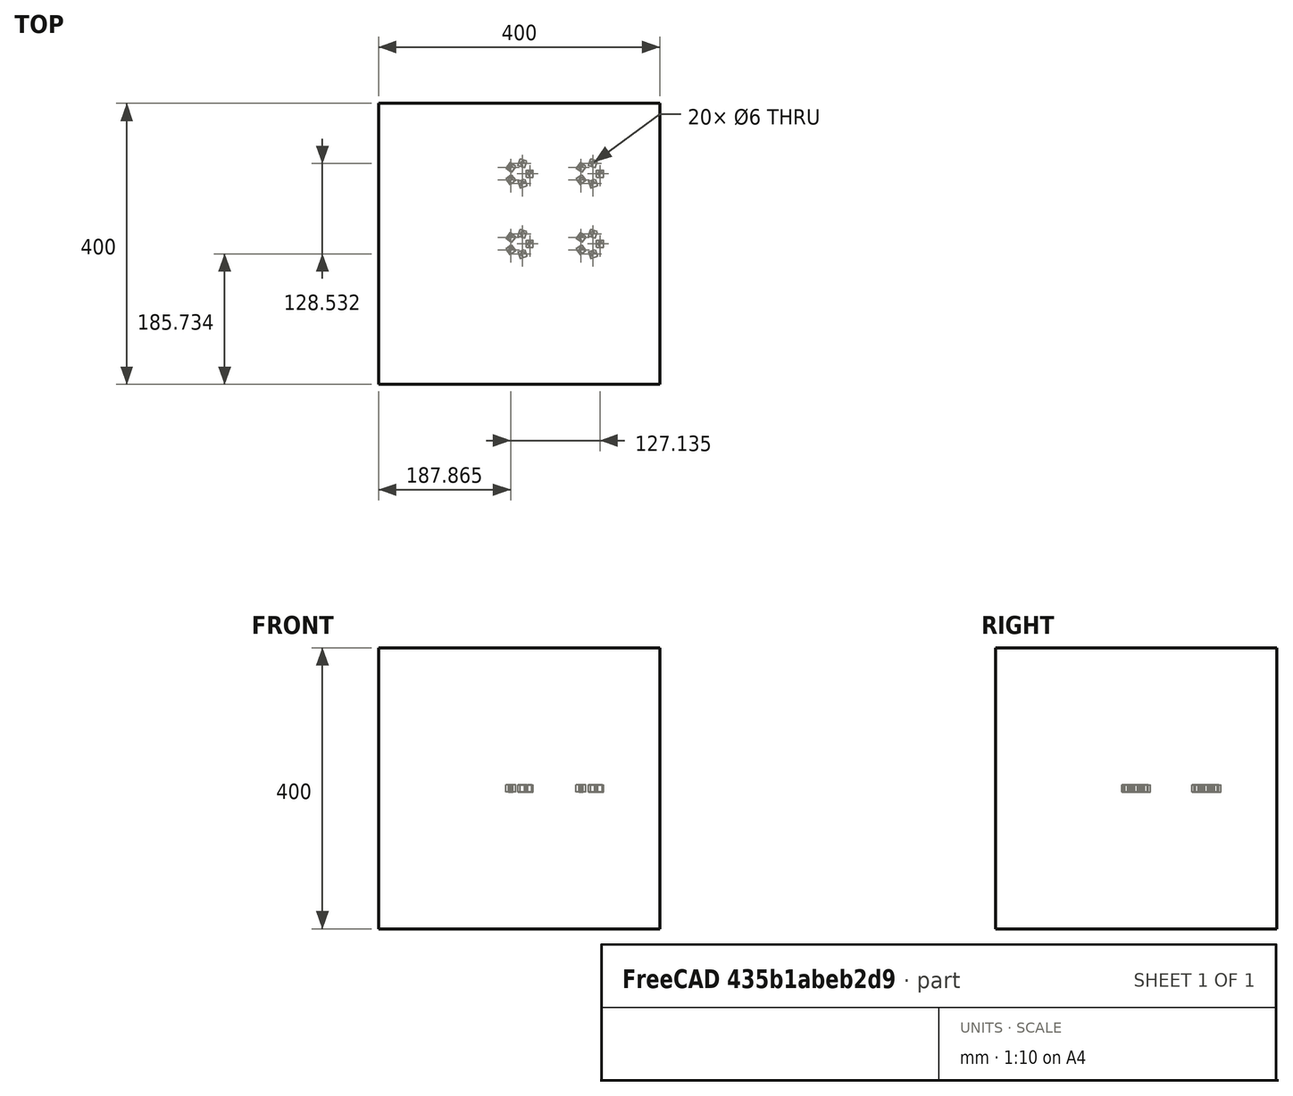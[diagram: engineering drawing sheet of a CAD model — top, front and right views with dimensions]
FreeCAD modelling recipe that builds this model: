
FCSTD DOCUMENT  (FreeCAD 1.0R39109 (Git))
Label: arrayTest-2
License: All rights reserved
LicenseURL: http://en.wikipedia.org/wiki/All_rights_reserved
objects: App::DocumentObjectGroupPython×1248, Part::FeaturePython×5, App::Part×2, Part::Cut×1
note: 6 computed .brp shape members not serialized (recipe doc carries the construction recipe); baked Part::Feature solids carry a one-line shape summary decoded from their .brp

FEATURE [App::DocumentObjectGroupPython] HALFPI  # scripted group (container) (typed FeaturePython)
  name = HALFPI
  value = pi/2.
FEATURE [App::DocumentObjectGroupPython] PI  # scripted group (container) (typed FeaturePython)
  name = PI
  value = 1.*pi
FEATURE [App::DocumentObjectGroupPython] TWOPI  # scripted group (container) (typed FeaturePython)
  name = TWOPI
  value = 2.*pi
FEATURE [App::DocumentObjectGroupPython] Constants  # scripted group (container) (typed FeaturePython)
  Group = -> [HALFPI,PI,TWOPI]
FEATURE [App::DocumentObjectGroupPython] Variables  # scripted group (container) (typed FeaturePython)
FEATURE [App::DocumentObjectGroupPython] Quantities  # scripted group (container) (typed FeaturePython)
FEATURE [App::DocumentObjectGroupPython] Isotopes  # scripted group (container) (typed FeaturePython)
FEATURE [App::DocumentObjectGroupPython] Elements  # scripted group (container) (typed FeaturePython)
FEATURE [App::DocumentObjectGroupPython] G4Isotopes  # scripted group (container) (typed FeaturePython)
FEATURE [App::DocumentObjectGroupPython] H_element  # scripted group (container) (typed FeaturePython)
  Z = 1
  atom_value = 1.008
  formula = H
  name = H_element
FEATURE [App::DocumentObjectGroupPython] He_element  # scripted group (container) (typed FeaturePython)
  Z = 2
  atom_value = 4.0026
  formula = He
  name = He_element
FEATURE [App::DocumentObjectGroupPython] Li_element  # scripted group (container) (typed FeaturePython)
  Z = 3
  atom_value = 6.94
  formula = Li
  name = Li_element
FEATURE [App::DocumentObjectGroupPython] Be_element  # scripted group (container) (typed FeaturePython)
  Z = 4
  atom_value = 9.01218
  formula = Be
  name = Be_element
FEATURE [App::DocumentObjectGroupPython] B_element  # scripted group (container) (typed FeaturePython)
  Z = 5
  atom_value = 10.81
  formula = B
  name = B_element
FEATURE [App::DocumentObjectGroupPython] C_element  # scripted group (container) (typed FeaturePython)
  Z = 6
  atom_value = 12.011
  formula = C
  name = C_element
FEATURE [App::DocumentObjectGroupPython] N_element  # scripted group (container) (typed FeaturePython)
  Z = 7
  atom_value = 14.007
  formula = N
  name = N_element
FEATURE [App::DocumentObjectGroupPython] O_element  # scripted group (container) (typed FeaturePython)
  Z = 8
  atom_value = 15.999
  formula = O
  name = O_element
FEATURE [App::DocumentObjectGroupPython] F_element  # scripted group (container) (typed FeaturePython)
  Z = 9
  atom_value = 18.9984
  formula = F
  name = F_element
FEATURE [App::DocumentObjectGroupPython] Ne_element  # scripted group (container) (typed FeaturePython)
  Z = 10
  atom_value = 20.1797
  formula = Ne
  name = Ne_element
FEATURE [App::DocumentObjectGroupPython] Na_element  # scripted group (container) (typed FeaturePython)
  Z = 11
  atom_value = 22.9898
  formula = Na
  name = Na_element
FEATURE [App::DocumentObjectGroupPython] Mg_element  # scripted group (container) (typed FeaturePython)
  Z = 12
  atom_value = 24.305
  formula = Mg
  name = Mg_element
FEATURE [App::DocumentObjectGroupPython] Al_element  # scripted group (container) (typed FeaturePython)
  Z = 13
  atom_value = 26.9815
  formula = Al
  name = Al_element
FEATURE [App::DocumentObjectGroupPython] Si_element  # scripted group (container) (typed FeaturePython)
  Z = 14
  atom_value = 28.085
  formula = Si
  name = Si_element
FEATURE [App::DocumentObjectGroupPython] P_element  # scripted group (container) (typed FeaturePython)
  Z = 15
  atom_value = 30.9738
  formula = P
  name = P_element
FEATURE [App::DocumentObjectGroupPython] S_element  # scripted group (container) (typed FeaturePython)
  Z = 16
  atom_value = 32.06
  formula = S
  name = S_element
FEATURE [App::DocumentObjectGroupPython] Cl_element  # scripted group (container) (typed FeaturePython)
  Z = 17
  atom_value = 35.45
  formula = Cl
  name = Cl_element
FEATURE [App::DocumentObjectGroupPython] Ar_element  # scripted group (container) (typed FeaturePython)
  Z = 18
  atom_value = 39.95
  formula = Ar
  name = Ar_element
FEATURE [App::DocumentObjectGroupPython] K_element  # scripted group (container) (typed FeaturePython)
  Z = 19
  atom_value = 39.0983
  formula = K
  name = K_element
FEATURE [App::DocumentObjectGroupPython] Ca_element  # scripted group (container) (typed FeaturePython)
  Z = 20
  atom_value = 40.078
  formula = Ca
  name = Ca_element
FEATURE [App::DocumentObjectGroupPython] Sc_element  # scripted group (container) (typed FeaturePython)
  Z = 21
  atom_value = 44.9559
  formula = Sc
  name = Sc_element
FEATURE [App::DocumentObjectGroupPython] Ti_element  # scripted group (container) (typed FeaturePython)
  Z = 22
  atom_value = 47.867
  formula = Ti
  name = Ti_element
FEATURE [App::DocumentObjectGroupPython] V_element  # scripted group (container) (typed FeaturePython)
  Z = 23
  atom_value = 50.9415
  formula = V
  name = V_element
FEATURE [App::DocumentObjectGroupPython] Cr_element  # scripted group (container) (typed FeaturePython)
  Z = 24
  atom_value = 51.9961
  formula = Cr
  name = Cr_element
FEATURE [App::DocumentObjectGroupPython] Mn_element  # scripted group (container) (typed FeaturePython)
  Z = 25
  atom_value = 54.938
  formula = Mn
  name = Mn_element
FEATURE [App::DocumentObjectGroupPython] Fe_element  # scripted group (container) (typed FeaturePython)
  Z = 26
  atom_value = 55.845
  formula = Fe
  name = Fe_element
FEATURE [App::DocumentObjectGroupPython] Co_element  # scripted group (container) (typed FeaturePython)
  Z = 27
  atom_value = 58.9332
  formula = Co
  name = Co_element
FEATURE [App::DocumentObjectGroupPython] Ni_element  # scripted group (container) (typed FeaturePython)
  Z = 28
  atom_value = 58.6934
  formula = Ni
  name = Ni_element
FEATURE [App::DocumentObjectGroupPython] Cu_element  # scripted group (container) (typed FeaturePython)
  Z = 29
  atom_value = 63.546
  formula = Cu
  name = Cu_element
FEATURE [App::DocumentObjectGroupPython] Zn_element  # scripted group (container) (typed FeaturePython)
  Z = 30
  atom_value = 65.38
  formula = Zn
  name = Zn_element
FEATURE [App::DocumentObjectGroupPython] Ga_element  # scripted group (container) (typed FeaturePython)
  Z = 31
  atom_value = 69.723
  formula = Ga
  name = Ga_element
FEATURE [App::DocumentObjectGroupPython] Ge_element  # scripted group (container) (typed FeaturePython)
  Z = 32
  atom_value = 72.63
  formula = Ge
  name = Ge_element
FEATURE [App::DocumentObjectGroupPython] As_element  # scripted group (container) (typed FeaturePython)
  Z = 33
  atom_value = 74.9216
  formula = As
  name = As_element
FEATURE [App::DocumentObjectGroupPython] Se_element  # scripted group (container) (typed FeaturePython)
  Z = 34
  atom_value = 78.971
  formula = Se
  name = Se_element
FEATURE [App::DocumentObjectGroupPython] Br_element  # scripted group (container) (typed FeaturePython)
  Z = 35
  atom_value = 79.904
  formula = Br
  name = Br_element
FEATURE [App::DocumentObjectGroupPython] Kr_element  # scripted group (container) (typed FeaturePython)
  Z = 36
  atom_value = 83.798
  formula = Kr
  name = Kr_element
FEATURE [App::DocumentObjectGroupPython] Rb_element  # scripted group (container) (typed FeaturePython)
  Z = 37
  atom_value = 85.4678
  formula = Rb
  name = Rb_element
FEATURE [App::DocumentObjectGroupPython] Sr_element  # scripted group (container) (typed FeaturePython)
  Z = 38
  atom_value = 87.62
  formula = Sr
  name = Sr_element
FEATURE [App::DocumentObjectGroupPython] Y_element  # scripted group (container) (typed FeaturePython)
  Z = 39
  atom_value = 88.9058
  formula = Y
  name = Y_element
FEATURE [App::DocumentObjectGroupPython] Zr_element  # scripted group (container) (typed FeaturePython)
  Z = 40
  atom_value = 91.224
  formula = Zr
  name = Zr_element
FEATURE [App::DocumentObjectGroupPython] Nb_element  # scripted group (container) (typed FeaturePython)
  Z = 41
  atom_value = 92.9064
  formula = Nb
  name = Nb_element
FEATURE [App::DocumentObjectGroupPython] Mo_element  # scripted group (container) (typed FeaturePython)
  Z = 42
  atom_value = 95.95
  formula = Mo
  name = Mo_element
FEATURE [App::DocumentObjectGroupPython] Tc_element  # scripted group (container) (typed FeaturePython)
  Z = 43
  atom_value = 97
  formula = Tc
  name = Tc_element
FEATURE [App::DocumentObjectGroupPython] Ru_element  # scripted group (container) (typed FeaturePython)
  Z = 44
  atom_value = 101.07
  formula = Ru
  name = Ru_element
FEATURE [App::DocumentObjectGroupPython] Rh_element  # scripted group (container) (typed FeaturePython)
  Z = 45
  atom_value = 102.905
  formula = Rh
  name = Rh_element
FEATURE [App::DocumentObjectGroupPython] Pd_element  # scripted group (container) (typed FeaturePython)
  Z = 46
  atom_value = 106.42
  formula = Pd
  name = Pd_element
FEATURE [App::DocumentObjectGroupPython] Ag_element  # scripted group (container) (typed FeaturePython)
  Z = 47
  atom_value = 107.868
  formula = Ag
  name = Ag_element
FEATURE [App::DocumentObjectGroupPython] Cd_element  # scripted group (container) (typed FeaturePython)
  Z = 48
  atom_value = 112.414
  formula = Cd
  name = Cd_element
FEATURE [App::DocumentObjectGroupPython] In_element  # scripted group (container) (typed FeaturePython)
  Z = 49
  atom_value = 114.818
  formula = In
  name = In_element
FEATURE [App::DocumentObjectGroupPython] Sn_element  # scripted group (container) (typed FeaturePython)
  Z = 50
  atom_value = 118.71
  formula = Sn
  name = Sn_element
FEATURE [App::DocumentObjectGroupPython] Sb_element  # scripted group (container) (typed FeaturePython)
  Z = 51
  atom_value = 121.76
  formula = Sb
  name = Sb_element
FEATURE [App::DocumentObjectGroupPython] Te_element  # scripted group (container) (typed FeaturePython)
  Z = 52
  atom_value = 127.6
  formula = Te
  name = Te_element
FEATURE [App::DocumentObjectGroupPython] I_element  # scripted group (container) (typed FeaturePython)
  Z = 53
  atom_value = 126.904
  formula = I
  name = I_element
FEATURE [App::DocumentObjectGroupPython] Xe_element  # scripted group (container) (typed FeaturePython)
  Z = 54
  atom_value = 131.293
  formula = Xe
  name = Xe_element
FEATURE [App::DocumentObjectGroupPython] Cs_element  # scripted group (container) (typed FeaturePython)
  Z = 55
  atom_value = 132.905
  formula = Cs
  name = Cs_element
FEATURE [App::DocumentObjectGroupPython] Ba_element  # scripted group (container) (typed FeaturePython)
  Z = 56
  atom_value = 137.327
  formula = Ba
  name = Ba_element
FEATURE [App::DocumentObjectGroupPython] La_element  # scripted group (container) (typed FeaturePython)
  Z = 57
  atom_value = 138.905
  formula = La
  name = La_element
FEATURE [App::DocumentObjectGroupPython] Ce_element  # scripted group (container) (typed FeaturePython)
  Z = 58
  atom_value = 140.116
  formula = Ce
  name = Ce_element
FEATURE [App::DocumentObjectGroupPython] Pr_element  # scripted group (container) (typed FeaturePython)
  Z = 59
  atom_value = 140.908
  formula = Pr
  name = Pr_element
FEATURE [App::DocumentObjectGroupPython] Nd_element  # scripted group (container) (typed FeaturePython)
  Z = 60
  atom_value = 144.242
  formula = Nd
  name = Nd_element
FEATURE [App::DocumentObjectGroupPython] Pm_element  # scripted group (container) (typed FeaturePython)
  Z = 61
  atom_value = 145
  formula = Pm
  name = Pm_element
FEATURE [App::DocumentObjectGroupPython] Sm_element  # scripted group (container) (typed FeaturePython)
  Z = 62
  atom_value = 150.36
  formula = Sm
  name = Sm_element
FEATURE [App::DocumentObjectGroupPython] Eu_element  # scripted group (container) (typed FeaturePython)
  Z = 63
  atom_value = 151.964
  formula = Eu
  name = Eu_element
FEATURE [App::DocumentObjectGroupPython] Gd_element  # scripted group (container) (typed FeaturePython)
  Z = 64
  atom_value = 157.25
  formula = Gd
  name = Gd_element
FEATURE [App::DocumentObjectGroupPython] Tb_element  # scripted group (container) (typed FeaturePython)
  Z = 65
  atom_value = 158.925
  formula = Tb
  name = Tb_element
FEATURE [App::DocumentObjectGroupPython] Dy_element  # scripted group (container) (typed FeaturePython)
  Z = 66
  atom_value = 162.5
  formula = Dy
  name = Dy_element
FEATURE [App::DocumentObjectGroupPython] Ho_element  # scripted group (container) (typed FeaturePython)
  Z = 67
  atom_value = 164.93
  formula = Ho
  name = Ho_element
FEATURE [App::DocumentObjectGroupPython] Er_element  # scripted group (container) (typed FeaturePython)
  Z = 68
  atom_value = 167.259
  formula = Er
  name = Er_element
FEATURE [App::DocumentObjectGroupPython] Tm_element  # scripted group (container) (typed FeaturePython)
  Z = 69
  atom_value = 168.934
  formula = Tm
  name = Tm_element
FEATURE [App::DocumentObjectGroupPython] Yb_element  # scripted group (container) (typed FeaturePython)
  Z = 70
  atom_value = 173.045
  formula = Yb
  name = Yb_element
FEATURE [App::DocumentObjectGroupPython] Lu_element  # scripted group (container) (typed FeaturePython)
  Z = 71
  atom_value = 174.967
  formula = Lu
  name = Lu_element
FEATURE [App::DocumentObjectGroupPython] Hf_element  # scripted group (container) (typed FeaturePython)
  Z = 72
  atom_value = 178.49
  formula = Hf
  name = Hf_element
FEATURE [App::DocumentObjectGroupPython] Ta_element  # scripted group (container) (typed FeaturePython)
  Z = 73
  atom_value = 180.948
  formula = Ta
  name = Ta_element
FEATURE [App::DocumentObjectGroupPython] W_element  # scripted group (container) (typed FeaturePython)
  Z = 74
  atom_value = 183.84
  formula = W
  name = W_element
FEATURE [App::DocumentObjectGroupPython] Re_element  # scripted group (container) (typed FeaturePython)
  Z = 75
  atom_value = 186.207
  formula = Re
  name = Re_element
FEATURE [App::DocumentObjectGroupPython] Os_element  # scripted group (container) (typed FeaturePython)
  Z = 76
  atom_value = 190.23
  formula = Os
  name = Os_element
FEATURE [App::DocumentObjectGroupPython] Ir_element  # scripted group (container) (typed FeaturePython)
  Z = 77
  atom_value = 192.217
  formula = Ir
  name = Ir_element
FEATURE [App::DocumentObjectGroupPython] Pt_element  # scripted group (container) (typed FeaturePython)
  Z = 78
  atom_value = 195.084
  formula = Pt
  name = Pt_element
FEATURE [App::DocumentObjectGroupPython] Au_element  # scripted group (container) (typed FeaturePython)
  Z = 79
  atom_value = 196.967
  formula = Au
  name = Au_element
FEATURE [App::DocumentObjectGroupPython] Hg_element  # scripted group (container) (typed FeaturePython)
  Z = 80
  atom_value = 200.592
  formula = Hg
  name = Hg_element
FEATURE [App::DocumentObjectGroupPython] Tl_element  # scripted group (container) (typed FeaturePython)
  Z = 81
  atom_value = 204.38
  formula = Tl
  name = Tl_element
FEATURE [App::DocumentObjectGroupPython] Pb_element  # scripted group (container) (typed FeaturePython)
  Z = 82
  atom_value = 207.2
  formula = Pb
  name = Pb_element
FEATURE [App::DocumentObjectGroupPython] Bi_element  # scripted group (container) (typed FeaturePython)
  Z = 83
  atom_value = 208.98
  formula = Bi
  name = Bi_element
FEATURE [App::DocumentObjectGroupPython] Po_element  # scripted group (container) (typed FeaturePython)
  Z = 84
  atom_value = 209
  formula = Po
  name = Po_element
FEATURE [App::DocumentObjectGroupPython] At_element  # scripted group (container) (typed FeaturePython)
  Z = 85
  atom_value = 210
  formula = At
  name = At_element
FEATURE [App::DocumentObjectGroupPython] Rn_element  # scripted group (container) (typed FeaturePython)
  Z = 86
  atom_value = 222
  formula = Rn
  name = Rn_element
FEATURE [App::DocumentObjectGroupPython] Fr_element  # scripted group (container) (typed FeaturePython)
  Z = 87
  atom_value = 223
  formula = Fr
  name = Fr_element
FEATURE [App::DocumentObjectGroupPython] Ra_element  # scripted group (container) (typed FeaturePython)
  Z = 88
  atom_value = 226
  formula = Ra
  name = Ra_element
FEATURE [App::DocumentObjectGroupPython] Ac_element  # scripted group (container) (typed FeaturePython)
  Z = 89
  atom_value = 227
  formula = Ac
  name = Ac_element
FEATURE [App::DocumentObjectGroupPython] Th_element  # scripted group (container) (typed FeaturePython)
  Z = 90
  atom_value = 232.038
  formula = Th
  name = Th_element
FEATURE [App::DocumentObjectGroupPython] Pa_element  # scripted group (container) (typed FeaturePython)
  Z = 91
  atom_value = 231.036
  formula = Pa
  name = Pa_element
FEATURE [App::DocumentObjectGroupPython] U_element  # scripted group (container) (typed FeaturePython)
  Z = 92
  atom_value = 238.029
  formula = U
  name = U_element
FEATURE [App::DocumentObjectGroupPython] Np_element  # scripted group (container) (typed FeaturePython)
  Z = 93
  atom_value = 237
  formula = Np
  name = Np_element
FEATURE [App::DocumentObjectGroupPython] Pu_element  # scripted group (container) (typed FeaturePython)
  Z = 94
  atom_value = 244
  formula = Pu
  name = Pu_element
FEATURE [App::DocumentObjectGroupPython] Am_element  # scripted group (container) (typed FeaturePython)
  Z = 95
  atom_value = 243
  formula = Am
  name = Am_element
FEATURE [App::DocumentObjectGroupPython] Cm_element  # scripted group (container) (typed FeaturePython)
  Z = 96
  atom_value = 247
  formula = Cm
  name = Cm_element
FEATURE [App::DocumentObjectGroupPython] Bk_element  # scripted group (container) (typed FeaturePython)
  Z = 97
  atom_value = 247
  formula = Bk
  name = Bk_element
FEATURE [App::DocumentObjectGroupPython] Cf_element  # scripted group (container) (typed FeaturePython)
  Z = 98
  atom_value = 251
  formula = Cf
  name = Cf_element
FEATURE [App::DocumentObjectGroupPython] G4Elements  # scripted group (container) (typed FeaturePython)
  Group = -> [H_element,He_element,Li_element,Be_element,B_element,C_element,N_element,O_element,F_element,Ne_element,Na_element,Mg_element,Al_element,Si_element,P_element,S_element,Cl_element,Ar_element,K_element,Ca_element,Sc_element,Ti_element,V_element,Cr_element,Mn_element,Fe_element,Co_element,Ni_element,Cu_element,Zn_element,Ga_element,Ge_element,As_element,Se_element,Br_element,Kr_element,Rb_element,+61 more]
FEATURE [App::DocumentObjectGroupPython] H_element001  label="H_element : 0.101"  # scripted group (container) (typed FeaturePython)
  n = 0.101327
FEATURE [App::DocumentObjectGroupPython] C_element001  label="C_element : 0.775"  # scripted group (container) (typed FeaturePython)
  n = 0.7755
FEATURE [App::DocumentObjectGroupPython] N_element001  label="N_element : 0.035"  # scripted group (container) (typed FeaturePython)
  n = 0.035057
FEATURE [App::DocumentObjectGroupPython] O_element001  label="O_element : 0.052"  # scripted group (container) (typed FeaturePython)
  n = 0.0523159
FEATURE [App::DocumentObjectGroupPython] F_element001  label="F_element : 0.017"  # scripted group (container) (typed FeaturePython)
  n = 0.017422
FEATURE [App::DocumentObjectGroupPython] Ca_element001  label="Ca_element : 0.018"  # scripted group (container) (typed FeaturePython)
  n = 0.018378
FEATURE [App::DocumentObjectGroupPython] G4_A_150_TISSUE  label="G4_A-150_TISSUE"  # scripted group (container) (typed FeaturePython)
  Dunit = g/cm3
  Dvalue = 1.127
  Group = -> [H_element001,C_element001,N_element001,O_element001,F_element001,Ca_element001]
  conduct = 2
  density = 1
  expand = 3
  formula = G4_A-150_TISSUE
  name = G4_A-150_TISSUE
  specific = 4
FEATURE [App::DocumentObjectGroupPython] C_element002  label="C_element : 3"  # scripted group (container) (typed FeaturePython)
  n = 3
  ref = C_element
FEATURE [App::DocumentObjectGroupPython] H_element002  label="H_element : 6"  # scripted group (container) (typed FeaturePython)
  n = 6
  ref = H_element
FEATURE [App::DocumentObjectGroupPython] O_element002  label="O_element : 1"  # scripted group (container) (typed FeaturePython)
  n = 1
  ref = O_element
FEATURE [App::DocumentObjectGroupPython] G4_ACETONE  # scripted group (container) (typed FeaturePython)
  Dunit = g/cm3
  Dvalue = 0.7899
  Group = -> [C_element002,H_element002,O_element002]
  conduct = 2
  density = 1
  expand = 3
  formula = G4_ACETONE
  name = G4_ACETONE
  specific = 4
FEATURE [App::DocumentObjectGroupPython] C_element003  label="C_element : 2"  # scripted group (container) (typed FeaturePython)
  n = 2
  ref = C_element
FEATURE [App::DocumentObjectGroupPython] H_element003  label="H_element : 2"  # scripted group (container) (typed FeaturePython)
  n = 2
  ref = H_element
FEATURE [App::DocumentObjectGroupPython] G4_ACETYLENE  # scripted group (container) (typed FeaturePython)
  Dunit = g/cm3
  Dvalue = 0.0010967
  Group = -> [C_element003,H_element003]
  conduct = 2
  density = 1
  expand = 3
  formula = G4_ACETYLENE
  name = G4_ACETYLENE
  specific = 4
FEATURE [App::DocumentObjectGroupPython] C_element004  label="C_element : 5"  # scripted group (container) (typed FeaturePython)
  n = 5
  ref = C_element
FEATURE [App::DocumentObjectGroupPython] H_element004  label="H_element : 5"  # scripted group (container) (typed FeaturePython)
  n = 5
  ref = H_element
FEATURE [App::DocumentObjectGroupPython] N_element002  label="N_element : 5"  # scripted group (container) (typed FeaturePython)
  n = 5
  ref = N_element
FEATURE [App::DocumentObjectGroupPython] G4_ADENINE  # scripted group (container) (typed FeaturePython)
  Dunit = g/cm3
  Dvalue = 1.6
  Group = -> [C_element004,H_element004,N_element002]
  conduct = 2
  density = 1
  expand = 3
  formula = G4_ADENINE
  name = G4_ADENINE
  specific = 4
FEATURE [App::DocumentObjectGroupPython] H_element005  label="H_element : 0.114"  # scripted group (container) (typed FeaturePython)
  n = 0.114
FEATURE [App::DocumentObjectGroupPython] C_element005  label="C_element : 0.598"  # scripted group (container) (typed FeaturePython)
  n = 0.598
FEATURE [App::DocumentObjectGroupPython] N_element003  label="N_element : 0.007"  # scripted group (container) (typed FeaturePython)
  n = 0.007
FEATURE [App::DocumentObjectGroupPython] O_element003  label="O_element : 0.278"  # scripted group (container) (typed FeaturePython)
  n = 0.278
FEATURE [App::DocumentObjectGroupPython] Na_element001  label="Na_element : 0.001"  # scripted group (container) (typed FeaturePython)
  n = 0.001
FEATURE [App::DocumentObjectGroupPython] S_element001  label="S_element : 0.001"  # scripted group (container) (typed FeaturePython)
  n = 0.001
FEATURE [App::DocumentObjectGroupPython] Cl_element001  label="Cl_element : 0.001"  # scripted group (container) (typed FeaturePython)
  n = 0.001
FEATURE [App::DocumentObjectGroupPython] G4_ADIPOSE_TISSUE_ICRP  # scripted group (container) (typed FeaturePython)
  Dunit = g/cm3
  Dvalue = 0.95
  Group = -> [H_element005,C_element005,N_element003,O_element003,Na_element001,S_element001,Cl_element001]
  conduct = 2
  density = 1
  expand = 3
  formula = G4_ADIPOSE_TISSUE_ICRP
  name = G4_ADIPOSE_TISSUE_ICRP
  specific = 4
FEATURE [App::DocumentObjectGroupPython] C_element006  label="C_element : 0.000"  # scripted group (container) (typed FeaturePython)
  n = 0.000124
FEATURE [App::DocumentObjectGroupPython] N_element004  label="N_element : 0.755"  # scripted group (container) (typed FeaturePython)
  n = 0.755268
FEATURE [App::DocumentObjectGroupPython] O_element004  label="O_element : 0.232"  # scripted group (container) (typed FeaturePython)
  n = 0.231781
FEATURE [App::DocumentObjectGroupPython] Ar_element001  label="Ar_element : 0.013"  # scripted group (container) (typed FeaturePython)
  n = 0.012827
FEATURE [App::DocumentObjectGroupPython] G4_AIR  # scripted group (container) (typed FeaturePython)
  Dunit = g/cm3
  Dvalue = 0.00120479
  Group = -> [C_element006,N_element004,O_element004,Ar_element001]
  conduct = 2
  density = 1
  expand = 3
  formula = G4_AIR
  name = G4_AIR
  specific = 4
FEATURE [App::DocumentObjectGroupPython] C_element007  label="C_element : 006"  # scripted group (container) (typed FeaturePython)
  n = 3
  ref = C_element
FEATURE [App::DocumentObjectGroupPython] H_element006  label="H_element : 7"  # scripted group (container) (typed FeaturePython)
  n = 7
  ref = H_element
FEATURE [App::DocumentObjectGroupPython] N_element005  label="N_element : 1"  # scripted group (container) (typed FeaturePython)
  n = 1
  ref = N_element
FEATURE [App::DocumentObjectGroupPython] O_element005  label="O_element : 2"  # scripted group (container) (typed FeaturePython)
  n = 2
  ref = O_element
FEATURE [App::DocumentObjectGroupPython] G4_ALANINE  # scripted group (container) (typed FeaturePython)
  Dunit = g/cm3
  Dvalue = 1.42
  Group = -> [C_element007,H_element006,N_element005,O_element005]
  conduct = 2
  density = 1
  expand = 3
  formula = G4_ALANINE
  name = G4_ALANINE
  specific = 4
FEATURE [App::DocumentObjectGroupPython] Al_element001  label="Al_element : 2"  # scripted group (container) (typed FeaturePython)
  n = 2
  ref = Al_element
FEATURE [App::DocumentObjectGroupPython] O_element006  label="O_element : 3"  # scripted group (container) (typed FeaturePython)
  n = 3
  ref = O_element
FEATURE [App::DocumentObjectGroupPython] G4_ALUMINUM_OXIDE  # scripted group (container) (typed FeaturePython)
  Dunit = g/cm3
  Dvalue = 3.97
  Group = -> [Al_element001,O_element006]
  conduct = 2
  density = 1
  expand = 3
  formula = G4_ALUMINUM_OXIDE
  name = G4_ALUMINUM_OXIDE
  specific = 4
FEATURE [App::DocumentObjectGroupPython] H_element007  label="H_element : 0.106"  # scripted group (container) (typed FeaturePython)
  n = 0.10593
FEATURE [App::DocumentObjectGroupPython] C_element008  label="C_element : 0.789"  # scripted group (container) (typed FeaturePython)
  n = 0.788974
FEATURE [App::DocumentObjectGroupPython] O_element007  label="O_element : 0.105"  # scripted group (container) (typed FeaturePython)
  n = 0.105096
FEATURE [App::DocumentObjectGroupPython] G4_AMBER  # scripted group (container) (typed FeaturePython)
  Dunit = g/cm3
  Dvalue = 1.1
  Group = -> [H_element007,C_element008,O_element007]
  conduct = 2
  density = 1
  expand = 3
  formula = G4_AMBER
  name = G4_AMBER
  specific = 4
FEATURE [App::DocumentObjectGroupPython] N_element006  label="N_element : 006"  # scripted group (container) (typed FeaturePython)
  n = 1
  ref = N_element
FEATURE [App::DocumentObjectGroupPython] H_element008  label="H_element : 3"  # scripted group (container) (typed FeaturePython)
  n = 3
  ref = H_element
FEATURE [App::DocumentObjectGroupPython] G4_AMMONIA  # scripted group (container) (typed FeaturePython)
  Dunit = g/cm3
  Dvalue = 0.000826019
  Group = -> [N_element006,H_element008]
  conduct = 2
  density = 1
  expand = 3
  formula = G4_AMMONIA
  name = G4_AMMONIA
  specific = 4
FEATURE [App::DocumentObjectGroupPython] C_element009  label="C_element : 6"  # scripted group (container) (typed FeaturePython)
  n = 6
  ref = C_element
FEATURE [App::DocumentObjectGroupPython] H_element009  label="H_element : 008"  # scripted group (container) (typed FeaturePython)
  n = 7
  ref = H_element
FEATURE [App::DocumentObjectGroupPython] N_element007  label="N_element : 007"  # scripted group (container) (typed FeaturePython)
  n = 1
  ref = N_element
FEATURE [App::DocumentObjectGroupPython] G4_ANILINE  # scripted group (container) (typed FeaturePython)
  Dunit = g/cm3
  Dvalue = 1.0235
  Group = -> [C_element009,H_element009,N_element007]
  conduct = 2
  density = 1
  expand = 3
  formula = G4_ANILINE
  name = G4_ANILINE
  specific = 4
FEATURE [App::DocumentObjectGroupPython] C_element010  label="C_element : 14"  # scripted group (container) (typed FeaturePython)
  n = 14
  ref = C_element
FEATURE [App::DocumentObjectGroupPython] H_element010  label="H_element : 10"  # scripted group (container) (typed FeaturePython)
  n = 10
  ref = H_element
FEATURE [App::DocumentObjectGroupPython] G4_ANTHRACENE  # scripted group (container) (typed FeaturePython)
  Dunit = g/cm3
  Dvalue = 1.283
  Group = -> [C_element010,H_element010]
  conduct = 2
  density = 1
  expand = 3
  formula = G4_ANTHRACENE
  name = G4_ANTHRACENE
  specific = 4
FEATURE [App::DocumentObjectGroupPython] H_element011  label="H_element : 0.065"  # scripted group (container) (typed FeaturePython)
  n = 0.0654709
FEATURE [App::DocumentObjectGroupPython] C_element011  label="C_element : 0.537"  # scripted group (container) (typed FeaturePython)
  n = 0.536944
FEATURE [App::DocumentObjectGroupPython] N_element008  label="N_element : 0.021"  # scripted group (container) (typed FeaturePython)
  n = 0.0215
FEATURE [App::DocumentObjectGroupPython] O_element008  label="O_element : 0.032"  # scripted group (container) (typed FeaturePython)
  n = 0.032085
FEATURE [App::DocumentObjectGroupPython] F_element002  label="F_element : 0.167"  # scripted group (container) (typed FeaturePython)
  n = 0.167411
FEATURE [App::DocumentObjectGroupPython] Ca_element002  label="Ca_element : 0.177"  # scripted group (container) (typed FeaturePython)
  n = 0.176589
FEATURE [App::DocumentObjectGroupPython] G4_B_100_BONE  label="G4_B-100_BONE"  # scripted group (container) (typed FeaturePython)
  Dunit = g/cm3
  Dvalue = 1.45
  Group = -> [H_element011,C_element011,N_element008,O_element008,F_element002,Ca_element002]
  conduct = 2
  density = 1
  expand = 3
  formula = G4_B-100_BONE
  name = G4_B-100_BONE
  specific = 4
FEATURE [App::DocumentObjectGroupPython] H_element012  label="H_element : 0.057"  # scripted group (container) (typed FeaturePython)
  n = 0.057441
FEATURE [App::DocumentObjectGroupPython] C_element012  label="C_element : 0.790"  # scripted group (container) (typed FeaturePython)
  n = 0.774591
FEATURE [App::DocumentObjectGroupPython] O_element009  label="O_element : 0.168"  # scripted group (container) (typed FeaturePython)
  n = 0.167968
FEATURE [App::DocumentObjectGroupPython] G4_BAKELITE  # scripted group (container) (typed FeaturePython)
  Dunit = g/cm3
  Dvalue = 1.25
  Group = -> [H_element012,C_element012,O_element009]
  conduct = 2
  density = 1
  expand = 3
  formula = G4_BAKELITE
  name = G4_BAKELITE
  specific = 4
FEATURE [App::DocumentObjectGroupPython] Ba_element001  label="Ba_element : 1"  # scripted group (container) (typed FeaturePython)
  n = 1
  ref = Ba_element
FEATURE [App::DocumentObjectGroupPython] F_element003  label="F_element : 2"  # scripted group (container) (typed FeaturePython)
  n = 2
  ref = F_element
FEATURE [App::DocumentObjectGroupPython] G4_BARIUM_FLUORIDE  # scripted group (container) (typed FeaturePython)
  Dunit = g/cm3
  Dvalue = 4.89
  Group = -> [Ba_element001,F_element003]
  conduct = 2
  density = 1
  expand = 3
  formula = G4_BARIUM_FLUORIDE
  name = G4_BARIUM_FLUORIDE
  specific = 4
FEATURE [App::DocumentObjectGroupPython] Ba_element002  label="Ba_element : 002"  # scripted group (container) (typed FeaturePython)
  n = 1
  ref = Ba_element
FEATURE [App::DocumentObjectGroupPython] S_element002  label="S_element : 1"  # scripted group (container) (typed FeaturePython)
  n = 1
  ref = S_element
FEATURE [App::DocumentObjectGroupPython] O_element010  label="O_element : 4"  # scripted group (container) (typed FeaturePython)
  n = 4
  ref = O_element
FEATURE [App::DocumentObjectGroupPython] G4_BARIUM_SULFATE  # scripted group (container) (typed FeaturePython)
  Dunit = g/cm3
  Dvalue = 4.5
  Group = -> [Ba_element002,S_element002,O_element010]
  conduct = 2
  density = 1
  expand = 3
  formula = G4_BARIUM_SULFATE
  name = G4_BARIUM_SULFATE
  specific = 4
FEATURE [App::DocumentObjectGroupPython] C_element013  label="C_element : 007"  # scripted group (container) (typed FeaturePython)
  n = 6
  ref = C_element
FEATURE [App::DocumentObjectGroupPython] H_element013  label="H_element : 009"  # scripted group (container) (typed FeaturePython)
  n = 6
  ref = H_element
FEATURE [App::DocumentObjectGroupPython] G4_BENZENE  # scripted group (container) (typed FeaturePython)
  Dunit = g/cm3
  Dvalue = 0.87865
  Group = -> [C_element013,H_element013]
  conduct = 2
  density = 1
  expand = 3
  formula = G4_BENZENE
  name = G4_BENZENE
  specific = 4
FEATURE [App::DocumentObjectGroupPython] Be_element001  label="Be_element : 1"  # scripted group (container) (typed FeaturePython)
  n = 1
  ref = Be_element
FEATURE [App::DocumentObjectGroupPython] O_element011  label="O_element : 005"  # scripted group (container) (typed FeaturePython)
  n = 1
  ref = O_element
FEATURE [App::DocumentObjectGroupPython] G4_BERYLLIUM_OXIDE  # scripted group (container) (typed FeaturePython)
  Dunit = g/cm3
  Dvalue = 3.01
  Group = -> [Be_element001,O_element011]
  conduct = 2
  density = 1
  expand = 3
  formula = G4_BERYLLIUM_OXIDE
  name = G4_BERYLLIUM_OXIDE
  specific = 4
FEATURE [App::DocumentObjectGroupPython] Bi_element001  label="Bi_element : 4"  # scripted group (container) (typed FeaturePython)
  n = 4
  ref = Bi_element
FEATURE [App::DocumentObjectGroupPython] Ge_element001  label="Ge_element : 3"  # scripted group (container) (typed FeaturePython)
  n = 3
  ref = Ge_element
FEATURE [App::DocumentObjectGroupPython] O_element012  label="O_element : 12"  # scripted group (container) (typed FeaturePython)
  n = 12
  ref = O_element
FEATURE [App::DocumentObjectGroupPython] G4_BGO  # scripted group (container) (typed FeaturePython)
  Dunit = g/cm3
  Dvalue = 7.13
  Group = -> [Bi_element001,Ge_element001,O_element012]
  conduct = 2
  density = 1
  expand = 3
  formula = G4_BGO
  name = G4_BGO
  specific = 4
FEATURE [App::DocumentObjectGroupPython] H_element014  label="H_element : 0.102"  # scripted group (container) (typed FeaturePython)
  n = 0.102
FEATURE [App::DocumentObjectGroupPython] C_element014  label="C_element : 0.110"  # scripted group (container) (typed FeaturePython)
  n = 0.11
FEATURE [App::DocumentObjectGroupPython] N_element009  label="N_element : 0.033"  # scripted group (container) (typed FeaturePython)
  n = 0.033
FEATURE [App::DocumentObjectGroupPython] O_element013  label="O_element : 0.745"  # scripted group (container) (typed FeaturePython)
  n = 0.745
FEATURE [App::DocumentObjectGroupPython] Na_element002  label="Na_element : 0.002"  # scripted group (container) (typed FeaturePython)
  n = 0.001
FEATURE [App::DocumentObjectGroupPython] P_element001  label="P_element : 0.001"  # scripted group (container) (typed FeaturePython)
  n = 0.001
FEATURE [App::DocumentObjectGroupPython] S_element003  label="S_element : 0.002"  # scripted group (container) (typed FeaturePython)
  n = 0.002
FEATURE [App::DocumentObjectGroupPython] Cl_element002  label="Cl_element : 0.003"  # scripted group (container) (typed FeaturePython)
  n = 0.003
FEATURE [App::DocumentObjectGroupPython] K_element001  label="K_element : 0.002"  # scripted group (container) (typed FeaturePython)
  n = 0.002
FEATURE [App::DocumentObjectGroupPython] Fe_element001  label="Fe_element : 0.001"  # scripted group (container) (typed FeaturePython)
  n = 0.001
FEATURE [App::DocumentObjectGroupPython] G4_BLOOD_ICRP  # scripted group (container) (typed FeaturePython)
  Dunit = g/cm3
  Dvalue = 1.06
  Group = -> [H_element014,C_element014,N_element009,O_element013,Na_element002,P_element001,S_element003,Cl_element002,K_element001,Fe_element001]
  conduct = 2
  density = 1
  expand = 3
  formula = G4_BLOOD_ICRP
  name = G4_BLOOD_ICRP
  specific = 4
FEATURE [App::DocumentObjectGroupPython] H_element015  label="H_element : 0.064"  # scripted group (container) (typed FeaturePython)
  n = 0.064
FEATURE [App::DocumentObjectGroupPython] C_element015  label="C_element : 0.278"  # scripted group (container) (typed FeaturePython)
  n = 0.278
FEATURE [App::DocumentObjectGroupPython] N_element010  label="N_element : 0.027"  # scripted group (container) (typed FeaturePython)
  n = 0.027
FEATURE [App::DocumentObjectGroupPython] O_element014  label="O_element : 0.410"  # scripted group (container) (typed FeaturePython)
  n = 0.41
FEATURE [App::DocumentObjectGroupPython] Mg_element001  label="Mg_element : 0.002"  # scripted group (container) (typed FeaturePython)
  n = 0.002
FEATURE [App::DocumentObjectGroupPython] P_element002  label="P_element : 0.070"  # scripted group (container) (typed FeaturePython)
  n = 0.07
FEATURE [App::DocumentObjectGroupPython] S_element004  label="S_element : 0.003"  # scripted group (container) (typed FeaturePython)
  n = 0.002
FEATURE [App::DocumentObjectGroupPython] Ca_element003  label="Ca_element : 0.147"  # scripted group (container) (typed FeaturePython)
  n = 0.147
FEATURE [App::DocumentObjectGroupPython] G4_BONE_COMPACT_ICRU  # scripted group (container) (typed FeaturePython)
  Dunit = g/cm3
  Dvalue = 1.85
  Group = -> [H_element015,C_element015,N_element010,O_element014,Mg_element001,P_element002,S_element004,Ca_element003]
  conduct = 2
  density = 1
  expand = 3
  formula = G4_BONE_COMPACT_ICRU
  name = G4_BONE_COMPACT_ICRU
  specific = 4
FEATURE [App::DocumentObjectGroupPython] H_element016  label="H_element : 0.034"  # scripted group (container) (typed FeaturePython)
  n = 0.034
FEATURE [App::DocumentObjectGroupPython] C_element016  label="C_element : 0.155"  # scripted group (container) (typed FeaturePython)
  n = 0.155
FEATURE [App::DocumentObjectGroupPython] N_element011  label="N_element : 0.042"  # scripted group (container) (typed FeaturePython)
  n = 0.042
FEATURE [App::DocumentObjectGroupPython] O_element015  label="O_element : 0.435"  # scripted group (container) (typed FeaturePython)
  n = 0.435
FEATURE [App::DocumentObjectGroupPython] Na_element003  label="Na_element : 0.003"  # scripted group (container) (typed FeaturePython)
  n = 0.001
FEATURE [App::DocumentObjectGroupPython] Mg_element002  label="Mg_element : 0.003"  # scripted group (container) (typed FeaturePython)
  n = 0.002
FEATURE [App::DocumentObjectGroupPython] P_element003  label="P_element : 0.103"  # scripted group (container) (typed FeaturePython)
  n = 0.103
FEATURE [App::DocumentObjectGroupPython] S_element005  label="S_element : 0.004"  # scripted group (container) (typed FeaturePython)
  n = 0.003
FEATURE [App::DocumentObjectGroupPython] Ca_element004  label="Ca_element : 0.225"  # scripted group (container) (typed FeaturePython)
  n = 0.225
FEATURE [App::DocumentObjectGroupPython] G4_BONE_CORTICAL_ICRP  # scripted group (container) (typed FeaturePython)
  Dunit = g/cm3
  Dvalue = 1.92
  Group = -> [H_element016,C_element016,N_element011,O_element015,Na_element003,Mg_element002,P_element003,S_element005,Ca_element004]
  conduct = 2
  density = 1
  expand = 3
  formula = G4_BONE_CORTICAL_ICRP
  name = G4_BONE_CORTICAL_ICRP
  specific = 4
FEATURE [App::DocumentObjectGroupPython] B_element001  label="B_element : 4"  # scripted group (container) (typed FeaturePython)
  n = 4
  ref = B_element
FEATURE [App::DocumentObjectGroupPython] C_element017  label="C_element : 1"  # scripted group (container) (typed FeaturePython)
  n = 1
  ref = C_element
FEATURE [App::DocumentObjectGroupPython] G4_BORON_CARBIDE  # scripted group (container) (typed FeaturePython)
  Dunit = g/cm3
  Dvalue = 2.52
  Group = -> [B_element001,C_element017]
  conduct = 2
  density = 1
  expand = 3
  formula = G4_BORON_CARBIDE
  name = G4_BORON_CARBIDE
  specific = 4
FEATURE [App::DocumentObjectGroupPython] B_element002  label="B_element : 2"  # scripted group (container) (typed FeaturePython)
  n = 2
  ref = B_element
FEATURE [App::DocumentObjectGroupPython] O_element016  label="O_element : 006"  # scripted group (container) (typed FeaturePython)
  n = 3
  ref = O_element
FEATURE [App::DocumentObjectGroupPython] G4_BORON_OXIDE  # scripted group (container) (typed FeaturePython)
  Dunit = g/cm3
  Dvalue = 1.812
  Group = -> [B_element002,O_element016]
  conduct = 2
  density = 1
  expand = 3
  formula = G4_BORON_OXIDE
  name = G4_BORON_OXIDE
  specific = 4
FEATURE [App::DocumentObjectGroupPython] H_element017  label="H_element : 0.107"  # scripted group (container) (typed FeaturePython)
  n = 0.107
FEATURE [App::DocumentObjectGroupPython] C_element018  label="C_element : 0.145"  # scripted group (container) (typed FeaturePython)
  n = 0.145
FEATURE [App::DocumentObjectGroupPython] N_element012  label="N_element : 0.022"  # scripted group (container) (typed FeaturePython)
  n = 0.022
FEATURE [App::DocumentObjectGroupPython] O_element017  label="O_element : 0.712"  # scripted group (container) (typed FeaturePython)
  n = 0.712
FEATURE [App::DocumentObjectGroupPython] Na_element004  label="Na_element : 0.004"  # scripted group (container) (typed FeaturePython)
  n = 0.002
FEATURE [App::DocumentObjectGroupPython] P_element004  label="P_element : 0.004"  # scripted group (container) (typed FeaturePython)
  n = 0.004
FEATURE [App::DocumentObjectGroupPython] S_element006  label="S_element : 0.005"  # scripted group (container) (typed FeaturePython)
  n = 0.002
FEATURE [App::DocumentObjectGroupPython] Cl_element003  label="Cl_element : 0.004"  # scripted group (container) (typed FeaturePython)
  n = 0.003
FEATURE [App::DocumentObjectGroupPython] K_element002  label="K_element : 0.003"  # scripted group (container) (typed FeaturePython)
  n = 0.003
FEATURE [App::DocumentObjectGroupPython] G4_BRAIN_ICRP  # scripted group (container) (typed FeaturePython)
  Dunit = g/cm3
  Dvalue = 1.04
  Group = -> [H_element017,C_element018,N_element012,O_element017,Na_element004,P_element004,S_element006,Cl_element003,K_element002]
  conduct = 2
  density = 1
  expand = 3
  formula = G4_BRAIN_ICRP
  name = G4_BRAIN_ICRP
  specific = 4
FEATURE [App::DocumentObjectGroupPython] C_element019  label="C_element : 4"  # scripted group (container) (typed FeaturePython)
  n = 4
  ref = C_element
FEATURE [App::DocumentObjectGroupPython] H_element018  label="H_element : 010"  # scripted group (container) (typed FeaturePython)
  n = 10
  ref = H_element
FEATURE [App::DocumentObjectGroupPython] G4_BUTANE  # scripted group (container) (typed FeaturePython)
  Dunit = g/cm3
  Dvalue = 0.00249343
  Group = -> [C_element019,H_element018]
  conduct = 2
  density = 1
  expand = 3
  formula = G4_BUTANE
  name = G4_BUTANE
  specific = 4
FEATURE [App::DocumentObjectGroupPython] C_element020  label="C_element : 008"  # scripted group (container) (typed FeaturePython)
  n = 4
  ref = C_element
FEATURE [App::DocumentObjectGroupPython] H_element019  label="H_element : 011"  # scripted group (container) (typed FeaturePython)
  n = 10
  ref = H_element
FEATURE [App::DocumentObjectGroupPython] O_element018  label="O_element : 007"  # scripted group (container) (typed FeaturePython)
  n = 1
  ref = O_element
FEATURE [App::DocumentObjectGroupPython] G4_N_BUTYL_ALCOHOL  label="G4_N-BUTYL_ALCOHOL"  # scripted group (container) (typed FeaturePython)
  Dunit = g/cm3
  Dvalue = 0.8098
  Group = -> [C_element020,H_element019,O_element018]
  conduct = 2
  density = 1
  expand = 3
  formula = G4_N-BUTYL_ALCOHOL
  name = G4_N-BUTYL_ALCOHOL
  specific = 4
FEATURE [App::DocumentObjectGroupPython] H_element020  label="H_element : 0.025"  # scripted group (container) (typed FeaturePython)
  n = 0.02468
FEATURE [App::DocumentObjectGroupPython] C_element021  label="C_element : 0.502"  # scripted group (container) (typed FeaturePython)
  n = 0.501611
FEATURE [App::DocumentObjectGroupPython] O_element019  label="O_element : 0.005"  # scripted group (container) (typed FeaturePython)
  n = 0.004527
FEATURE [App::DocumentObjectGroupPython] F_element004  label="F_element : 0.465"  # scripted group (container) (typed FeaturePython)
  n = 0.465209
FEATURE [App::DocumentObjectGroupPython] Si_element001  label="Si_element : 0.004"  # scripted group (container) (typed FeaturePython)
  n = 0.003973
FEATURE [App::DocumentObjectGroupPython] G4_C_552  label="G4_C-552"  # scripted group (container) (typed FeaturePython)
  Dunit = g/cm3
  Dvalue = 1.76
  Group = -> [H_element020,C_element021,O_element019,F_element004,Si_element001]
  conduct = 2
  density = 1
  expand = 3
  formula = G4_C-552
  name = G4_C-552
  specific = 4
FEATURE [App::DocumentObjectGroupPython] Cd_element001  label="Cd_element : 1"  # scripted group (container) (typed FeaturePython)
  n = 1
  ref = Cd_element
FEATURE [App::DocumentObjectGroupPython] Te_element001  label="Te_element : 1"  # scripted group (container) (typed FeaturePython)
  n = 1
  ref = Te_element
FEATURE [App::DocumentObjectGroupPython] G4_CADMIUM_TELLURIDE  # scripted group (container) (typed FeaturePython)
  Dunit = g/cm3
  Dvalue = 6.2
  Group = -> [Cd_element001,Te_element001]
  conduct = 2
  density = 1
  expand = 3
  formula = G4_CADMIUM_TELLURIDE
  name = G4_CADMIUM_TELLURIDE
  specific = 4
FEATURE [App::DocumentObjectGroupPython] Cd_element002  label="Cd_element : 002"  # scripted group (container) (typed FeaturePython)
  n = 1
  ref = Cd_element
FEATURE [App::DocumentObjectGroupPython] W_element001  label="W_element : 1"  # scripted group (container) (typed FeaturePython)
  n = 1
  ref = W_element
FEATURE [App::DocumentObjectGroupPython] O_element020  label="O_element : 008"  # scripted group (container) (typed FeaturePython)
  n = 4
  ref = O_element
FEATURE [App::DocumentObjectGroupPython] G4_CADMIUM_TUNGSTATE  # scripted group (container) (typed FeaturePython)
  Dunit = g/cm3
  Dvalue = 7.9
  Group = -> [Cd_element002,W_element001,O_element020]
  conduct = 2
  density = 1
  expand = 3
  formula = G4_CADMIUM_TUNGSTATE
  name = G4_CADMIUM_TUNGSTATE
  specific = 4
FEATURE [App::DocumentObjectGroupPython] Ca_element005  label="Ca_element : 1"  # scripted group (container) (typed FeaturePython)
  n = 1
  ref = Ca_element
FEATURE [App::DocumentObjectGroupPython] C_element022  label="C_element : 009"  # scripted group (container) (typed FeaturePython)
  n = 1
  ref = C_element
FEATURE [App::DocumentObjectGroupPython] O_element021  label="O_element : 009"  # scripted group (container) (typed FeaturePython)
  n = 3
  ref = O_element
FEATURE [App::DocumentObjectGroupPython] G4_CALCIUM_CARBONATE  # scripted group (container) (typed FeaturePython)
  Dunit = g/cm3
  Dvalue = 2.8
  Group = -> [Ca_element005,C_element022,O_element021]
  conduct = 2
  density = 1
  expand = 3
  formula = G4_CALCIUM_CARBONATE
  name = G4_CALCIUM_CARBONATE
  specific = 4
FEATURE [App::DocumentObjectGroupPython] Ca_element006  label="Ca_element : 002"  # scripted group (container) (typed FeaturePython)
  n = 1
  ref = Ca_element
FEATURE [App::DocumentObjectGroupPython] F_element005  label="F_element : 003"  # scripted group (container) (typed FeaturePython)
  n = 2
  ref = F_element
FEATURE [App::DocumentObjectGroupPython] G4_CALCIUM_FLUORIDE  # scripted group (container) (typed FeaturePython)
  Dunit = g/cm3
  Dvalue = 3.18
  Group = -> [Ca_element006,F_element005]
  conduct = 2
  density = 1
  expand = 3
  formula = G4_CALCIUM_FLUORIDE
  name = G4_CALCIUM_FLUORIDE
  specific = 4
FEATURE [App::DocumentObjectGroupPython] Ca_element007  label="Ca_element : 003"  # scripted group (container) (typed FeaturePython)
  n = 1
  ref = Ca_element
FEATURE [App::DocumentObjectGroupPython] O_element022  label="O_element : 010"  # scripted group (container) (typed FeaturePython)
  n = 1
  ref = O_element
FEATURE [App::DocumentObjectGroupPython] G4_CALCIUM_OXIDE  # scripted group (container) (typed FeaturePython)
  Dunit = g/cm3
  Dvalue = 3.3
  Group = -> [Ca_element007,O_element022]
  conduct = 2
  density = 1
  expand = 3
  formula = G4_CALCIUM_OXIDE
  name = G4_CALCIUM_OXIDE
  specific = 4
FEATURE [App::DocumentObjectGroupPython] Ca_element008  label="Ca_element : 004"  # scripted group (container) (typed FeaturePython)
  n = 1
  ref = Ca_element
FEATURE [App::DocumentObjectGroupPython] S_element007  label="S_element : 002"  # scripted group (container) (typed FeaturePython)
  n = 1
  ref = S_element
FEATURE [App::DocumentObjectGroupPython] O_element023  label="O_element : 011"  # scripted group (container) (typed FeaturePython)
  n = 4
  ref = O_element
FEATURE [App::DocumentObjectGroupPython] G4_CALCIUM_SULFATE  # scripted group (container) (typed FeaturePython)
  Dunit = g/cm3
  Dvalue = 2.96
  Group = -> [Ca_element008,S_element007,O_element023]
  conduct = 2
  density = 1
  expand = 3
  formula = G4_CALCIUM_SULFATE
  name = G4_CALCIUM_SULFATE
  specific = 4
FEATURE [App::DocumentObjectGroupPython] Ca_element009  label="Ca_element : 005"  # scripted group (container) (typed FeaturePython)
  n = 1
  ref = Ca_element
FEATURE [App::DocumentObjectGroupPython] W_element002  label="W_element : 002"  # scripted group (container) (typed FeaturePython)
  n = 1
  ref = W_element
FEATURE [App::DocumentObjectGroupPython] O_element024  label="O_element : 012"  # scripted group (container) (typed FeaturePython)
  n = 4
  ref = O_element
FEATURE [App::DocumentObjectGroupPython] G4_CALCIUM_TUNGSTATE  # scripted group (container) (typed FeaturePython)
  Dunit = g/cm3
  Dvalue = 6.062
  Group = -> [Ca_element009,W_element002,O_element024]
  conduct = 2
  density = 1
  expand = 3
  formula = G4_CALCIUM_TUNGSTATE
  name = G4_CALCIUM_TUNGSTATE
  specific = 4
FEATURE [App::DocumentObjectGroupPython] C_element023  label="C_element : 010"  # scripted group (container) (typed FeaturePython)
  n = 1
  ref = C_element
FEATURE [App::DocumentObjectGroupPython] O_element025  label="O_element : 013"  # scripted group (container) (typed FeaturePython)
  n = 2
  ref = O_element
FEATURE [App::DocumentObjectGroupPython] G4_CARBON_DIOXIDE  # scripted group (container) (typed FeaturePython)
  Dunit = g/cm3
  Dvalue = 0.00184212
  Group = -> [C_element023,O_element025]
  conduct = 2
  density = 1
  expand = 3
  formula = G4_CARBON_DIOXIDE
  name = G4_CARBON_DIOXIDE
  specific = 4
FEATURE [App::DocumentObjectGroupPython] C_element024  label="C_element : 011"  # scripted group (container) (typed FeaturePython)
  n = 1
  ref = C_element
FEATURE [App::DocumentObjectGroupPython] Cl_element004  label="Cl_element : 4"  # scripted group (container) (typed FeaturePython)
  n = 4
  ref = Cl_element
FEATURE [App::DocumentObjectGroupPython] G4_CARBON_TETRACHLORIDE  # scripted group (container) (typed FeaturePython)
  Dunit = g/cm3
  Dvalue = 1.594
  Group = -> [C_element024,Cl_element004]
  conduct = 2
  density = 1
  expand = 3
  formula = G4_CARBON_TETRACHLORIDE
  name = G4_CARBON_TETRACHLORIDE
  specific = 4
FEATURE [App::DocumentObjectGroupPython] C_element025  label="C_element : 012"  # scripted group (container) (typed FeaturePython)
  n = 6
  ref = C_element
FEATURE [App::DocumentObjectGroupPython] H_element021  label="H_element : 012"  # scripted group (container) (typed FeaturePython)
  n = 10
  ref = H_element
FEATURE [App::DocumentObjectGroupPython] O_element026  label="O_element : 5"  # scripted group (container) (typed FeaturePython)
  n = 5
  ref = O_element
FEATURE [App::DocumentObjectGroupPython] G4_CELLULOSE_CELLOPHANE  # scripted group (container) (typed FeaturePython)
  Dunit = g/cm3
  Dvalue = 1.42
  Group = -> [C_element025,H_element021,O_element026]
  conduct = 2
  density = 1
  expand = 3
  formula = G4_CELLULOSE_CELLOPHANE
  name = G4_CELLULOSE_CELLOPHANE
  specific = 4
FEATURE [App::DocumentObjectGroupPython] H_element022  label="H_element : 0.067"  # scripted group (container) (typed FeaturePython)
  n = 0.067125
FEATURE [App::DocumentObjectGroupPython] C_element026  label="C_element : 0.545"  # scripted group (container) (typed FeaturePython)
  n = 0.545403
FEATURE [App::DocumentObjectGroupPython] O_element027  label="O_element : 0.387"  # scripted group (container) (typed FeaturePython)
  n = 0.387472
FEATURE [App::DocumentObjectGroupPython] G4_CELLULOSE_BUTYRATE  # scripted group (container) (typed FeaturePython)
  Dunit = g/cm3
  Dvalue = 1.2
  Group = -> [H_element022,C_element026,O_element027]
  conduct = 2
  density = 1
  expand = 3
  formula = G4_CELLULOSE_BUTYRATE
  name = G4_CELLULOSE_BUTYRATE
  specific = 4
FEATURE [App::DocumentObjectGroupPython] H_element023  label="H_element : 0.029"  # scripted group (container) (typed FeaturePython)
  n = 0.029216
FEATURE [App::DocumentObjectGroupPython] C_element027  label="C_element : 0.271"  # scripted group (container) (typed FeaturePython)
  n = 0.271296
FEATURE [App::DocumentObjectGroupPython] N_element013  label="N_element : 0.121"  # scripted group (container) (typed FeaturePython)
  n = 0.121276
FEATURE [App::DocumentObjectGroupPython] O_element028  label="O_element : 0.578"  # scripted group (container) (typed FeaturePython)
  n = 0.578212
FEATURE [App::DocumentObjectGroupPython] G4_CELLULOSE_NITRATE  # scripted group (container) (typed FeaturePython)
  Dunit = g/cm3
  Dvalue = 1.49
  Group = -> [H_element023,C_element027,N_element013,O_element028]
  conduct = 2
  density = 1
  expand = 3
  formula = G4_CELLULOSE_NITRATE
  name = G4_CELLULOSE_NITRATE
  specific = 4
FEATURE [App::DocumentObjectGroupPython] H_element024  label="H_element : 0.108"  # scripted group (container) (typed FeaturePython)
  n = 0.107596
FEATURE [App::DocumentObjectGroupPython] N_element014  label="N_element : 0.001"  # scripted group (container) (typed FeaturePython)
  n = 0.0008
FEATURE [App::DocumentObjectGroupPython] O_element029  label="O_element : 0.875"  # scripted group (container) (typed FeaturePython)
  n = 0.874976
FEATURE [App::DocumentObjectGroupPython] S_element008  label="S_element : 0.015"  # scripted group (container) (typed FeaturePython)
  n = 0.014627
FEATURE [App::DocumentObjectGroupPython] Ce_element001  label="Ce_element : 0.002"  # scripted group (container) (typed FeaturePython)
  n = 0.002001
FEATURE [App::DocumentObjectGroupPython] G4_CERIC_SULFATE  # scripted group (container) (typed FeaturePython)
  Dunit = g/cm3
  Dvalue = 1.03
  Group = -> [H_element024,N_element014,O_element029,S_element008,Ce_element001]
  conduct = 2
  density = 1
  expand = 3
  formula = G4_CERIC_SULFATE
  name = G4_CERIC_SULFATE
  specific = 4
FEATURE [App::DocumentObjectGroupPython] Cs_element001  label="Cs_element : 1"  # scripted group (container) (typed FeaturePython)
  n = 1
  ref = Cs_element
FEATURE [App::DocumentObjectGroupPython] F_element006  label="F_element : 1"  # scripted group (container) (typed FeaturePython)
  n = 1
  ref = F_element
FEATURE [App::DocumentObjectGroupPython] G4_CESIUM_FLUORIDE  # scripted group (container) (typed FeaturePython)
  Dunit = g/cm3
  Dvalue = 4.115
  Group = -> [Cs_element001,F_element006]
  conduct = 2
  density = 1
  expand = 3
  formula = G4_CESIUM_FLUORIDE
  name = G4_CESIUM_FLUORIDE
  specific = 4
FEATURE [App::DocumentObjectGroupPython] Cs_element002  label="Cs_element : 002"  # scripted group (container) (typed FeaturePython)
  n = 1
  ref = Cs_element
FEATURE [App::DocumentObjectGroupPython] I_element001  label="I_element : 1"  # scripted group (container) (typed FeaturePython)
  n = 1
  ref = I_element
FEATURE [App::DocumentObjectGroupPython] G4_CESIUM_IODIDE  # scripted group (container) (typed FeaturePython)
  Dunit = g/cm3
  Dvalue = 4.51
  Group = -> [Cs_element002,I_element001]
  conduct = 2
  density = 1
  expand = 3
  formula = G4_CESIUM_IODIDE
  name = G4_CESIUM_IODIDE
  specific = 4
FEATURE [App::DocumentObjectGroupPython] C_element028  label="C_element : 013"  # scripted group (container) (typed FeaturePython)
  n = 6
  ref = C_element
FEATURE [App::DocumentObjectGroupPython] H_element025  label="H_element : 013"  # scripted group (container) (typed FeaturePython)
  n = 5
  ref = H_element
FEATURE [App::DocumentObjectGroupPython] Cl_element005  label="Cl_element : 1"  # scripted group (container) (typed FeaturePython)
  n = 1
  ref = Cl_element
FEATURE [App::DocumentObjectGroupPython] G4_CHLOROBENZENE  # scripted group (container) (typed FeaturePython)
  Dunit = g/cm3
  Dvalue = 1.1058
  Group = -> [C_element028,H_element025,Cl_element005]
  conduct = 2
  density = 1
  expand = 3
  formula = G4_CHLOROBENZENE
  name = G4_CHLOROBENZENE
  specific = 4
FEATURE [App::DocumentObjectGroupPython] C_element029  label="C_element : 014"  # scripted group (container) (typed FeaturePython)
  n = 1
  ref = C_element
FEATURE [App::DocumentObjectGroupPython] H_element026  label="H_element : 1"  # scripted group (container) (typed FeaturePython)
  n = 1
  ref = H_element
FEATURE [App::DocumentObjectGroupPython] Cl_element006  label="Cl_element : 3"  # scripted group (container) (typed FeaturePython)
  n = 3
  ref = Cl_element
FEATURE [App::DocumentObjectGroupPython] G4_CHLOROFORM  # scripted group (container) (typed FeaturePython)
  Dunit = g/cm3
  Dvalue = 1.4832
  Group = -> [C_element029,H_element026,Cl_element006]
  conduct = 2
  density = 1
  expand = 3
  formula = G4_CHLOROFORM
  name = G4_CHLOROFORM
  specific = 4
FEATURE [App::DocumentObjectGroupPython] H_element027  label="H_element : 0.010"  # scripted group (container) (typed FeaturePython)
  n = 0.01
FEATURE [App::DocumentObjectGroupPython] C_element030  label="C_element : 0.001"  # scripted group (container) (typed FeaturePython)
  n = 0.001
FEATURE [App::DocumentObjectGroupPython] O_element030  label="O_element : 0.529"  # scripted group (container) (typed FeaturePython)
  n = 0.529107
FEATURE [App::DocumentObjectGroupPython] Na_element005  label="Na_element : 0.016"  # scripted group (container) (typed FeaturePython)
  n = 0.016
FEATURE [App::DocumentObjectGroupPython] Mg_element003  label="Mg_element : 0.004"  # scripted group (container) (typed FeaturePython)
  n = 0.002
FEATURE [App::DocumentObjectGroupPython] Al_element002  label="Al_element : 0.034"  # scripted group (container) (typed FeaturePython)
  n = 0.033872
FEATURE [App::DocumentObjectGroupPython] Si_element002  label="Si_element : 0.337"  # scripted group (container) (typed FeaturePython)
  n = 0.337021
FEATURE [App::DocumentObjectGroupPython] K_element003  label="K_element : 0.013"  # scripted group (container) (typed FeaturePython)
  n = 0.013
FEATURE [App::DocumentObjectGroupPython] Ca_element010  label="Ca_element : 0.044"  # scripted group (container) (typed FeaturePython)
  n = 0.044
FEATURE [App::DocumentObjectGroupPython] Fe_element002  label="Fe_element : 0.014"  # scripted group (container) (typed FeaturePython)
  n = 0.014
FEATURE [App::DocumentObjectGroupPython] G4_CONCRETE  # scripted group (container) (typed FeaturePython)
  Dunit = g/cm3
  Dvalue = 2.3
  Group = -> [H_element027,C_element030,O_element030,Na_element005,Mg_element003,Al_element002,Si_element002,K_element003,Ca_element010,Fe_element002]
  conduct = 2
  density = 1
  expand = 3
  formula = G4_CONCRETE
  name = G4_CONCRETE
  specific = 4
FEATURE [App::DocumentObjectGroupPython] C_element031  label="C_element : 015"  # scripted group (container) (typed FeaturePython)
  n = 6
  ref = C_element
FEATURE [App::DocumentObjectGroupPython] H_element028  label="H_element : 12"  # scripted group (container) (typed FeaturePython)
  n = 12
  ref = H_element
FEATURE [App::DocumentObjectGroupPython] G4_CYCLOHEXANE  # scripted group (container) (typed FeaturePython)
  Dunit = g/cm3
  Dvalue = 0.779
  Group = -> [C_element031,H_element028]
  conduct = 2
  density = 1
  expand = 3
  formula = G4_CYCLOHEXANE
  name = G4_CYCLOHEXANE
  specific = 4
FEATURE [App::DocumentObjectGroupPython] C_element032  label="C_element : 016"  # scripted group (container) (typed FeaturePython)
  n = 6
  ref = C_element
FEATURE [App::DocumentObjectGroupPython] H_element029  label="H_element : 4"  # scripted group (container) (typed FeaturePython)
  n = 4
  ref = H_element
FEATURE [App::DocumentObjectGroupPython] Cl_element007  label="Cl_element : 2"  # scripted group (container) (typed FeaturePython)
  n = 2
  ref = Cl_element
FEATURE [App::DocumentObjectGroupPython] G4_1_2_DICHLOROBENZENE  label="G4_1.2-DICHLOROBENZENE"  # scripted group (container) (typed FeaturePython)
  Dunit = g/cm3
  Dvalue = 1.3048
  Group = -> [C_element032,H_element029,Cl_element007]
  conduct = 2
  density = 1
  expand = 3
  formula = G4_1.2-DICHLOROBENZENE
  name = G4_1.2-DICHLOROBENZENE
  specific = 4
FEATURE [App::DocumentObjectGroupPython] C_element033  label="C_element : 017"  # scripted group (container) (typed FeaturePython)
  n = 4
  ref = C_element
FEATURE [App::DocumentObjectGroupPython] H_element030  label="H_element : 8"  # scripted group (container) (typed FeaturePython)
  n = 8
  ref = H_element
FEATURE [App::DocumentObjectGroupPython] O_element031  label="O_element : 014"  # scripted group (container) (typed FeaturePython)
  n = 1
  ref = O_element
FEATURE [App::DocumentObjectGroupPython] Cl_element008  label="Cl_element : 005"  # scripted group (container) (typed FeaturePython)
  n = 2
  ref = Cl_element
FEATURE [App::DocumentObjectGroupPython] G4_DICHLORODIETHYL_ETHER  # scripted group (container) (typed FeaturePython)
  Dunit = g/cm3
  Dvalue = 1.2199
  Group = -> [C_element033,H_element030,O_element031,Cl_element008]
  conduct = 2
  density = 1
  expand = 3
  formula = G4_DICHLORODIETHYL_ETHER
  name = G4_DICHLORODIETHYL_ETHER
  specific = 4
FEATURE [App::DocumentObjectGroupPython] C_element034  label="C_element : 018"  # scripted group (container) (typed FeaturePython)
  n = 2
  ref = C_element
FEATURE [App::DocumentObjectGroupPython] H_element031  label="H_element : 014"  # scripted group (container) (typed FeaturePython)
  n = 4
  ref = H_element
FEATURE [App::DocumentObjectGroupPython] Cl_element009  label="Cl_element : 006"  # scripted group (container) (typed FeaturePython)
  n = 2
  ref = Cl_element
FEATURE [App::DocumentObjectGroupPython] G4_1_2_DICHLOROETHANE  label="G4_1.2-DICHLOROETHANE"  # scripted group (container) (typed FeaturePython)
  Dunit = g/cm3
  Dvalue = 1.2351
  Group = -> [C_element034,H_element031,Cl_element009]
  conduct = 2
  density = 1
  expand = 3
  formula = G4_1.2-DICHLOROETHANE
  name = G4_1.2-DICHLOROETHANE
  specific = 4
FEATURE [App::DocumentObjectGroupPython] C_element035  label="C_element : 019"  # scripted group (container) (typed FeaturePython)
  n = 4
  ref = C_element
FEATURE [App::DocumentObjectGroupPython] H_element032  label="H_element : 015"  # scripted group (container) (typed FeaturePython)
  n = 10
  ref = H_element
FEATURE [App::DocumentObjectGroupPython] O_element032  label="O_element : 015"  # scripted group (container) (typed FeaturePython)
  n = 1
  ref = O_element
FEATURE [App::DocumentObjectGroupPython] G4_DIETHYL_ETHER  # scripted group (container) (typed FeaturePython)
  Dunit = g/cm3
  Dvalue = 0.71378
  Group = -> [C_element035,H_element032,O_element032]
  conduct = 2
  density = 1
  expand = 3
  formula = G4_DIETHYL_ETHER
  name = G4_DIETHYL_ETHER
  specific = 4
FEATURE [App::DocumentObjectGroupPython] C_element036  label="C_element : 020"  # scripted group (container) (typed FeaturePython)
  n = 3
  ref = C_element
FEATURE [App::DocumentObjectGroupPython] H_element033  label="H_element : 016"  # scripted group (container) (typed FeaturePython)
  n = 7
  ref = H_element
FEATURE [App::DocumentObjectGroupPython] N_element015  label="N_element : 008"  # scripted group (container) (typed FeaturePython)
  n = 1
  ref = N_element
FEATURE [App::DocumentObjectGroupPython] O_element033  label="O_element : 016"  # scripted group (container) (typed FeaturePython)
  n = 1
  ref = O_element
FEATURE [App::DocumentObjectGroupPython] G4_N_N_DIMETHYL_FORMAMIDE  label="G4_N.N-DIMETHYL_FORMAMIDE"  # scripted group (container) (typed FeaturePython)
  Dunit = g/cm3
  Dvalue = 0.9487
  Group = -> [C_element036,H_element033,N_element015,O_element033]
  conduct = 2
  density = 1
  expand = 3
  formula = G4_N.N-DIMETHYL_FORMAMIDE
  name = G4_N.N-DIMETHYL_FORMAMIDE
  specific = 4
FEATURE [App::DocumentObjectGroupPython] C_element037  label="C_element : 021"  # scripted group (container) (typed FeaturePython)
  n = 2
  ref = C_element
FEATURE [App::DocumentObjectGroupPython] H_element034  label="H_element : 017"  # scripted group (container) (typed FeaturePython)
  n = 6
  ref = H_element
FEATURE [App::DocumentObjectGroupPython] O_element034  label="O_element : 017"  # scripted group (container) (typed FeaturePython)
  n = 1
  ref = O_element
FEATURE [App::DocumentObjectGroupPython] S_element009  label="S_element : 003"  # scripted group (container) (typed FeaturePython)
  n = 1
  ref = S_element
FEATURE [App::DocumentObjectGroupPython] G4_DIMETHYL_SULFOXIDE  # scripted group (container) (typed FeaturePython)
  Dunit = g/cm3
  Dvalue = 1.1014
  Group = -> [C_element037,H_element034,O_element034,S_element009]
  conduct = 2
  density = 1
  expand = 3
  formula = G4_DIMETHYL_SULFOXIDE
  name = G4_DIMETHYL_SULFOXIDE
  specific = 4
FEATURE [App::DocumentObjectGroupPython] C_element038  label="C_element : 022"  # scripted group (container) (typed FeaturePython)
  n = 2
  ref = C_element
FEATURE [App::DocumentObjectGroupPython] H_element035  label="H_element : 018"  # scripted group (container) (typed FeaturePython)
  n = 6
  ref = H_element
FEATURE [App::DocumentObjectGroupPython] G4_ETHANE  # scripted group (container) (typed FeaturePython)
  Dunit = g/cm3
  Dvalue = 0.00125324
  Group = -> [C_element038,H_element035]
  conduct = 2
  density = 1
  expand = 3
  formula = G4_ETHANE
  name = G4_ETHANE
  specific = 4
FEATURE [App::DocumentObjectGroupPython] C_element039  label="C_element : 023"  # scripted group (container) (typed FeaturePython)
  n = 2
  ref = C_element
FEATURE [App::DocumentObjectGroupPython] H_element036  label="H_element : 019"  # scripted group (container) (typed FeaturePython)
  n = 6
  ref = H_element
FEATURE [App::DocumentObjectGroupPython] O_element035  label="O_element : 018"  # scripted group (container) (typed FeaturePython)
  n = 1
  ref = O_element
FEATURE [App::DocumentObjectGroupPython] G4_ETHYL_ALCOHOL  # scripted group (container) (typed FeaturePython)
  Dunit = g/cm3
  Dvalue = 0.7893
  Group = -> [C_element039,H_element036,O_element035]
  conduct = 2
  density = 1
  expand = 3
  formula = G4_ETHYL_ALCOHOL
  name = G4_ETHYL_ALCOHOL
  specific = 4
FEATURE [App::DocumentObjectGroupPython] H_element037  label="H_element : 0.090"  # scripted group (container) (typed FeaturePython)
  n = 0.090027
FEATURE [App::DocumentObjectGroupPython] C_element040  label="C_element : 0.585"  # scripted group (container) (typed FeaturePython)
  n = 0.585182
FEATURE [App::DocumentObjectGroupPython] O_element036  label="O_element : 0.325"  # scripted group (container) (typed FeaturePython)
  n = 0.324791
FEATURE [App::DocumentObjectGroupPython] G4_ETHYL_CELLULOSE  # scripted group (container) (typed FeaturePython)
  Dunit = g/cm3
  Dvalue = 1.13
  Group = -> [H_element037,C_element040,O_element036]
  conduct = 2
  density = 1
  expand = 3
  formula = G4_ETHYL_CELLULOSE
  name = G4_ETHYL_CELLULOSE
  specific = 4
FEATURE [App::DocumentObjectGroupPython] C_element041  label="C_element : 024"  # scripted group (container) (typed FeaturePython)
  n = 2
  ref = C_element
FEATURE [App::DocumentObjectGroupPython] H_element038  label="H_element : 020"  # scripted group (container) (typed FeaturePython)
  n = 4
  ref = H_element
FEATURE [App::DocumentObjectGroupPython] G4_ETHYLENE  # scripted group (container) (typed FeaturePython)
  Dunit = g/cm3
  Dvalue = 0.00117497
  Group = -> [C_element041,H_element038]
  conduct = 2
  density = 1
  expand = 3
  formula = G4_ETHYLENE
  name = G4_ETHYLENE
  specific = 4
FEATURE [App::DocumentObjectGroupPython] H_element039  label="H_element : 0.096"  # scripted group (container) (typed FeaturePython)
  n = 0.096
FEATURE [App::DocumentObjectGroupPython] C_element042  label="C_element : 0.195"  # scripted group (container) (typed FeaturePython)
  n = 0.195
FEATURE [App::DocumentObjectGroupPython] N_element016  label="N_element : 0.057"  # scripted group (container) (typed FeaturePython)
  n = 0.057
FEATURE [App::DocumentObjectGroupPython] O_element037  label="O_element : 0.646"  # scripted group (container) (typed FeaturePython)
  n = 0.646
FEATURE [App::DocumentObjectGroupPython] Na_element006  label="Na_element : 0.017"  # scripted group (container) (typed FeaturePython)
  n = 0.001
FEATURE [App::DocumentObjectGroupPython] P_element005  label="P_element : 0.104"  # scripted group (container) (typed FeaturePython)
  n = 0.001
FEATURE [App::DocumentObjectGroupPython] S_element010  label="S_element : 0.016"  # scripted group (container) (typed FeaturePython)
  n = 0.003
FEATURE [App::DocumentObjectGroupPython] Cl_element010  label="Cl_element : 0.005"  # scripted group (container) (typed FeaturePython)
  n = 0.001
FEATURE [App::DocumentObjectGroupPython] G4_EYE_LENS_ICRP  # scripted group (container) (typed FeaturePython)
  Dunit = g/cm3
  Dvalue = 1.07
  Group = -> [H_element039,C_element042,N_element016,O_element037,Na_element006,P_element005,S_element010,Cl_element010]
  conduct = 2
  density = 1
  expand = 3
  formula = G4_EYE_LENS_ICRP
  name = G4_EYE_LENS_ICRP
  specific = 4
FEATURE [App::DocumentObjectGroupPython] Fe_element003  label="Fe_element : 2"  # scripted group (container) (typed FeaturePython)
  n = 2
  ref = Fe_element
FEATURE [App::DocumentObjectGroupPython] O_element038  label="O_element : 019"  # scripted group (container) (typed FeaturePython)
  n = 3
  ref = O_element
FEATURE [App::DocumentObjectGroupPython] G4_FERRIC_OXIDE  # scripted group (container) (typed FeaturePython)
  Dunit = g/cm3
  Dvalue = 5.2
  Group = -> [Fe_element003,O_element038]
  conduct = 2
  density = 1
  expand = 3
  formula = G4_FERRIC_OXIDE
  name = G4_FERRIC_OXIDE
  specific = 4
FEATURE [App::DocumentObjectGroupPython] Fe_element004  label="Fe_element : 1"  # scripted group (container) (typed FeaturePython)
  n = 1
  ref = Fe_element
FEATURE [App::DocumentObjectGroupPython] B_element003  label="B_element : 1"  # scripted group (container) (typed FeaturePython)
  n = 1
  ref = B_element
FEATURE [App::DocumentObjectGroupPython] G4_FERROBORIDE  # scripted group (container) (typed FeaturePython)
  Dunit = g/cm3
  Dvalue = 7.15
  Group = -> [Fe_element004,B_element003]
  conduct = 2
  density = 1
  expand = 3
  formula = G4_FERROBORIDE
  name = G4_FERROBORIDE
  specific = 4
FEATURE [App::DocumentObjectGroupPython] Fe_element005  label="Fe_element : 003"  # scripted group (container) (typed FeaturePython)
  n = 1
  ref = Fe_element
FEATURE [App::DocumentObjectGroupPython] O_element039  label="O_element : 020"  # scripted group (container) (typed FeaturePython)
  n = 1
  ref = O_element
FEATURE [App::DocumentObjectGroupPython] G4_FERROUS_OXIDE  # scripted group (container) (typed FeaturePython)
  Dunit = g/cm3
  Dvalue = 5.7
  Group = -> [Fe_element005,O_element039]
  conduct = 2
  density = 1
  expand = 3
  formula = G4_FERROUS_OXIDE
  name = G4_FERROUS_OXIDE
  specific = 4
FEATURE [App::DocumentObjectGroupPython] H_element040  label="H_element : 0.115"  # scripted group (container) (typed FeaturePython)
  n = 0.108259
FEATURE [App::DocumentObjectGroupPython] N_element017  label="N_element : 0.000"  # scripted group (container) (typed FeaturePython)
  n = 2.7e-05
FEATURE [App::DocumentObjectGroupPython] O_element040  label="O_element : 0.879"  # scripted group (container) (typed FeaturePython)
  n = 0.878636
FEATURE [App::DocumentObjectGroupPython] Na_element007  label="Na_element : 0.000"  # scripted group (container) (typed FeaturePython)
  n = 2.2e-05
FEATURE [App::DocumentObjectGroupPython] S_element011  label="S_element : 0.013"  # scripted group (container) (typed FeaturePython)
  n = 0.012968
FEATURE [App::DocumentObjectGroupPython] Cl_element011  label="Cl_element : 0.000"  # scripted group (container) (typed FeaturePython)
  n = 3.4e-05
FEATURE [App::DocumentObjectGroupPython] Fe_element006  label="Fe_element : 0.000"  # scripted group (container) (typed FeaturePython)
  n = 5.4e-05
FEATURE [App::DocumentObjectGroupPython] G4_FERROUS_SULFATE  # scripted group (container) (typed FeaturePython)
  Dunit = g/cm3
  Dvalue = 1.024
  Group = -> [H_element040,N_element017,O_element040,Na_element007,S_element011,Cl_element011,Fe_element006]
  conduct = 2
  density = 1
  expand = 3
  formula = G4_FERROUS_SULFATE
  name = G4_FERROUS_SULFATE
  specific = 4
FEATURE [App::DocumentObjectGroupPython] C_element043  label="C_element : 0.099"  # scripted group (container) (typed FeaturePython)
  n = 0.099335
FEATURE [App::DocumentObjectGroupPython] F_element007  label="F_element : 0.314"  # scripted group (container) (typed FeaturePython)
  n = 0.314247
FEATURE [App::DocumentObjectGroupPython] Cl_element012  label="Cl_element : 0.586"  # scripted group (container) (typed FeaturePython)
  n = 0.586418
FEATURE [App::DocumentObjectGroupPython] G4_FREON_12  label="G4_FREON-12"  # scripted group (container) (typed FeaturePython)
  Dunit = g/cm3
  Dvalue = 1.12
  Group = -> [C_element043,F_element007,Cl_element012]
  conduct = 2
  density = 1
  expand = 3
  formula = G4_FREON-12
  name = G4_FREON-12
  specific = 4
FEATURE [App::DocumentObjectGroupPython] C_element044  label="C_element : 0.057"  # scripted group (container) (typed FeaturePython)
  n = 0.057245
FEATURE [App::DocumentObjectGroupPython] F_element008  label="F_element : 0.181"  # scripted group (container) (typed FeaturePython)
  n = 0.181096
FEATURE [App::DocumentObjectGroupPython] Br_element001  label="Br_element : 0.762"  # scripted group (container) (typed FeaturePython)
  n = 0.761659
FEATURE [App::DocumentObjectGroupPython] G4_FREON_12B2  label="G4_FREON-12B2"  # scripted group (container) (typed FeaturePython)
  Dunit = g/cm3
  Dvalue = 1.8
  Group = -> [C_element044,F_element008,Br_element001]
  conduct = 2
  density = 1
  expand = 3
  formula = G4_FREON-12B2
  name = G4_FREON-12B2
  specific = 4
FEATURE [App::DocumentObjectGroupPython] C_element045  label="C_element : 0.115"  # scripted group (container) (typed FeaturePython)
  n = 0.114983
FEATURE [App::DocumentObjectGroupPython] F_element009  label="F_element : 0.546"  # scripted group (container) (typed FeaturePython)
  n = 0.545621
FEATURE [App::DocumentObjectGroupPython] Cl_element013  label="Cl_element : 0.339"  # scripted group (container) (typed FeaturePython)
  n = 0.339396
FEATURE [App::DocumentObjectGroupPython] G4_FREON_13  label="G4_FREON-13"  # scripted group (container) (typed FeaturePython)
  Dunit = g/cm3
  Dvalue = 0.95
  Group = -> [C_element045,F_element009,Cl_element013]
  conduct = 2
  density = 1
  expand = 3
  formula = G4_FREON-13
  name = G4_FREON-13
  specific = 4
FEATURE [App::DocumentObjectGroupPython] C_element046  label="C_element : 025"  # scripted group (container) (typed FeaturePython)
  n = 1
  ref = C_element
FEATURE [App::DocumentObjectGroupPython] F_element010  label="F_element : 3"  # scripted group (container) (typed FeaturePython)
  n = 3
  ref = F_element
FEATURE [App::DocumentObjectGroupPython] Br_element002  label="Br_element : 1"  # scripted group (container) (typed FeaturePython)
  n = 1
  ref = Br_element
FEATURE [App::DocumentObjectGroupPython] G4_FREON_13B1  label="G4_FREON-13B1"  # scripted group (container) (typed FeaturePython)
  Dunit = g/cm3
  Dvalue = 1.5
  Group = -> [C_element046,F_element010,Br_element002]
  conduct = 2
  density = 1
  expand = 3
  formula = G4_FREON-13B1
  name = G4_FREON-13B1
  specific = 4
FEATURE [App::DocumentObjectGroupPython] C_element047  label="C_element : 0.061"  # scripted group (container) (typed FeaturePython)
  n = 0.061309
FEATURE [App::DocumentObjectGroupPython] F_element011  label="F_element : 0.291"  # scripted group (container) (typed FeaturePython)
  n = 0.290924
FEATURE [App::DocumentObjectGroupPython] I_element002  label="I_element : 0.648"  # scripted group (container) (typed FeaturePython)
  n = 0.647767
FEATURE [App::DocumentObjectGroupPython] G4_FREON_13I1  label="G4_FREON-13I1"  # scripted group (container) (typed FeaturePython)
  Dunit = g/cm3
  Dvalue = 1.8
  Group = -> [C_element047,F_element011,I_element002]
  conduct = 2
  density = 1
  expand = 3
  formula = G4_FREON-13I1
  name = G4_FREON-13I1
  specific = 4
FEATURE [App::DocumentObjectGroupPython] Gd_element001  label="Gd_element : 2"  # scripted group (container) (typed FeaturePython)
  n = 2
  ref = Gd_element
FEATURE [App::DocumentObjectGroupPython] O_element041  label="O_element : 021"  # scripted group (container) (typed FeaturePython)
  n = 2
  ref = O_element
FEATURE [App::DocumentObjectGroupPython] S_element012  label="S_element : 004"  # scripted group (container) (typed FeaturePython)
  n = 1
  ref = S_element
FEATURE [App::DocumentObjectGroupPython] G4_GADOLINIUM_OXYSULFIDE  # scripted group (container) (typed FeaturePython)
  Dunit = g/cm3
  Dvalue = 7.44
  Group = -> [Gd_element001,O_element041,S_element012]
  conduct = 2
  density = 1
  expand = 3
  formula = G4_GADOLINIUM_OXYSULFIDE
  name = G4_GADOLINIUM_OXYSULFIDE
  specific = 4
FEATURE [App::DocumentObjectGroupPython] Ga_element001  label="Ga_element : 1"  # scripted group (container) (typed FeaturePython)
  n = 1
  ref = Ga_element
FEATURE [App::DocumentObjectGroupPython] As_element001  label="As_element : 1"  # scripted group (container) (typed FeaturePython)
  n = 1
  ref = As_element
FEATURE [App::DocumentObjectGroupPython] G4_GALLIUM_ARSENIDE  # scripted group (container) (typed FeaturePython)
  Dunit = g/cm3
  Dvalue = 5.31
  Group = -> [Ga_element001,As_element001]
  conduct = 2
  density = 1
  expand = 3
  formula = G4_GALLIUM_ARSENIDE
  name = G4_GALLIUM_ARSENIDE
  specific = 4
FEATURE [App::DocumentObjectGroupPython] H_element041  label="H_element : 0.081"  # scripted group (container) (typed FeaturePython)
  n = 0.08118
FEATURE [App::DocumentObjectGroupPython] C_element048  label="C_element : 0.416"  # scripted group (container) (typed FeaturePython)
  n = 0.41606
FEATURE [App::DocumentObjectGroupPython] N_element018  label="N_element : 0.111"  # scripted group (container) (typed FeaturePython)
  n = 0.11124
FEATURE [App::DocumentObjectGroupPython] O_element042  label="O_element : 0.381"  # scripted group (container) (typed FeaturePython)
  n = 0.38064
FEATURE [App::DocumentObjectGroupPython] S_element013  label="S_element : 0.011"  # scripted group (container) (typed FeaturePython)
  n = 0.01088
FEATURE [App::DocumentObjectGroupPython] G4_GEL_PHOTO_EMULSION  # scripted group (container) (typed FeaturePython)
  Dunit = g/cm3
  Dvalue = 1.2914
  Group = -> [H_element041,C_element048,N_element018,O_element042,S_element013]
  conduct = 2
  density = 1
  expand = 3
  formula = G4_GEL_PHOTO_EMULSION
  name = G4_GEL_PHOTO_EMULSION
  specific = 4
FEATURE [App::DocumentObjectGroupPython] B_element004  label="B_element : 0.040"  # scripted group (container) (typed FeaturePython)
  n = 0.0400639
FEATURE [App::DocumentObjectGroupPython] O_element043  label="O_element : 0.540"  # scripted group (container) (typed FeaturePython)
  n = 0.539561
FEATURE [App::DocumentObjectGroupPython] Na_element008  label="Na_element : 0.028"  # scripted group (container) (typed FeaturePython)
  n = 0.0281909
FEATURE [App::DocumentObjectGroupPython] Al_element003  label="Al_element : 0.012"  # scripted group (container) (typed FeaturePython)
  n = 0.011644
FEATURE [App::DocumentObjectGroupPython] Si_element003  label="Si_element : 0.377"  # scripted group (container) (typed FeaturePython)
  n = 0.377219
FEATURE [App::DocumentObjectGroupPython] K_element004  label="K_element : 0.014"  # scripted group (container) (typed FeaturePython)
  n = 0.00332099
FEATURE [App::DocumentObjectGroupPython] G4_Pyrex_Glass  # scripted group (container) (typed FeaturePython)
  Dunit = g/cm3
  Dvalue = 2.23
  Group = -> [B_element004,O_element043,Na_element008,Al_element003,Si_element003,K_element004]
  conduct = 2
  density = 1
  expand = 3
  formula = G4_Pyrex_Glass
  name = G4_Pyrex_Glass
  specific = 4
FEATURE [App::DocumentObjectGroupPython] O_element044  label="O_element : 0.156"  # scripted group (container) (typed FeaturePython)
  n = 0.156453
FEATURE [App::DocumentObjectGroupPython] Si_element004  label="Si_element : 0.081"  # scripted group (container) (typed FeaturePython)
  n = 0.080866
FEATURE [App::DocumentObjectGroupPython] Ti_element001  label="Ti_element : 0.008"  # scripted group (container) (typed FeaturePython)
  n = 0.008092
FEATURE [App::DocumentObjectGroupPython] As_element002  label="As_element : 0.003"  # scripted group (container) (typed FeaturePython)
  n = 0.002651
FEATURE [App::DocumentObjectGroupPython] Pb_element001  label="Pb_element : 0.752"  # scripted group (container) (typed FeaturePython)
  n = 0.751938
FEATURE [App::DocumentObjectGroupPython] G4_GLASS_LEAD  # scripted group (container) (typed FeaturePython)
  Dunit = g/cm3
  Dvalue = 6.22
  Group = -> [O_element044,Si_element004,Ti_element001,As_element002,Pb_element001]
  conduct = 2
  density = 1
  expand = 3
  formula = G4_GLASS_LEAD
  name = G4_GLASS_LEAD
  specific = 4
FEATURE [App::DocumentObjectGroupPython] O_element045  label="O_element : 0.460"  # scripted group (container) (typed FeaturePython)
  n = 0.4598
FEATURE [App::DocumentObjectGroupPython] Na_element009  label="Na_element : 0.096"  # scripted group (container) (typed FeaturePython)
  n = 0.0964411
FEATURE [App::DocumentObjectGroupPython] Si_element005  label="Si_element : 0.378"  # scripted group (container) (typed FeaturePython)
  n = 0.336553
FEATURE [App::DocumentObjectGroupPython] Ca_element011  label="Ca_element : 0.107"  # scripted group (container) (typed FeaturePython)
  n = 0.107205
FEATURE [App::DocumentObjectGroupPython] G4_GLASS_PLATE  # scripted group (container) (typed FeaturePython)
  Dunit = g/cm3
  Dvalue = 2.4
  Group = -> [O_element045,Na_element009,Si_element005,Ca_element011]
  conduct = 2
  density = 1
  expand = 3
  formula = G4_GLASS_PLATE
  name = G4_GLASS_PLATE
  specific = 4
FEATURE [App::DocumentObjectGroupPython] C_element049  label="C_element : 026"  # scripted group (container) (typed FeaturePython)
  n = 5
  ref = C_element
FEATURE [App::DocumentObjectGroupPython] H_element042  label="H_element : 021"  # scripted group (container) (typed FeaturePython)
  n = 10
  ref = H_element
FEATURE [App::DocumentObjectGroupPython] N_element019  label="N_element : 2"  # scripted group (container) (typed FeaturePython)
  n = 2
  ref = N_element
FEATURE [App::DocumentObjectGroupPython] O_element046  label="O_element : 022"  # scripted group (container) (typed FeaturePython)
  n = 3
  ref = O_element
FEATURE [App::DocumentObjectGroupPython] G4_GLUTAMINE  # scripted group (container) (typed FeaturePython)
  Dunit = g/cm3
  Dvalue = 1.46
  Group = -> [C_element049,H_element042,N_element019,O_element046]
  conduct = 2
  density = 1
  expand = 3
  formula = G4_GLUTAMINE
  name = G4_GLUTAMINE
  specific = 4
FEATURE [App::DocumentObjectGroupPython] C_element050  label="C_element : 027"  # scripted group (container) (typed FeaturePython)
  n = 3
  ref = C_element
FEATURE [App::DocumentObjectGroupPython] H_element043  label="H_element : 022"  # scripted group (container) (typed FeaturePython)
  n = 8
  ref = H_element
FEATURE [App::DocumentObjectGroupPython] O_element047  label="O_element : 023"  # scripted group (container) (typed FeaturePython)
  n = 3
  ref = O_element
FEATURE [App::DocumentObjectGroupPython] G4_GLYCEROL  # scripted group (container) (typed FeaturePython)
  Dunit = g/cm3
  Dvalue = 1.2613
  Group = -> [C_element050,H_element043,O_element047]
  conduct = 2
  density = 1
  expand = 3
  formula = G4_GLYCEROL
  name = G4_GLYCEROL
  specific = 4
FEATURE [App::DocumentObjectGroupPython] C_element051  label="C_element : 028"  # scripted group (container) (typed FeaturePython)
  n = 5
  ref = C_element
FEATURE [App::DocumentObjectGroupPython] H_element044  label="H_element : 023"  # scripted group (container) (typed FeaturePython)
  n = 5
  ref = H_element
FEATURE [App::DocumentObjectGroupPython] N_element020  label="N_element : 009"  # scripted group (container) (typed FeaturePython)
  n = 5
  ref = N_element
FEATURE [App::DocumentObjectGroupPython] O_element048  label="O_element : 024"  # scripted group (container) (typed FeaturePython)
  n = 1
  ref = O_element
FEATURE [App::DocumentObjectGroupPython] G4_GUANINE  # scripted group (container) (typed FeaturePython)
  Dunit = g/cm3
  Dvalue = 2.2
  Group = -> [C_element051,H_element044,N_element020,O_element048]
  conduct = 2
  density = 1
  expand = 3
  formula = G4_GUANINE
  name = G4_GUANINE
  specific = 4
FEATURE [App::DocumentObjectGroupPython] Ca_element012  label="Ca_element : 006"  # scripted group (container) (typed FeaturePython)
  n = 1
  ref = Ca_element
FEATURE [App::DocumentObjectGroupPython] S_element014  label="S_element : 005"  # scripted group (container) (typed FeaturePython)
  n = 1
  ref = S_element
FEATURE [App::DocumentObjectGroupPython] O_element049  label="O_element : 6"  # scripted group (container) (typed FeaturePython)
  n = 6
  ref = O_element
FEATURE [App::DocumentObjectGroupPython] H_element045  label="H_element : 024"  # scripted group (container) (typed FeaturePython)
  n = 4
  ref = H_element
FEATURE [App::DocumentObjectGroupPython] G4_GYPSUM  # scripted group (container) (typed FeaturePython)
  Dunit = g/cm3
  Dvalue = 2.32
  Group = -> [Ca_element012,S_element014,O_element049,H_element045]
  conduct = 2
  density = 1
  expand = 3
  formula = G4_GYPSUM
  name = G4_GYPSUM
  specific = 4
FEATURE [App::DocumentObjectGroupPython] C_element052  label="C_element : 7"  # scripted group (container) (typed FeaturePython)
  n = 7
  ref = C_element
FEATURE [App::DocumentObjectGroupPython] H_element046  label="H_element : 16"  # scripted group (container) (typed FeaturePython)
  n = 16
  ref = H_element
FEATURE [App::DocumentObjectGroupPython] G4_N_HEPTANE  label="G4_N-HEPTANE"  # scripted group (container) (typed FeaturePython)
  Dunit = g/cm3
  Dvalue = 0.68376
  Group = -> [C_element052,H_element046]
  conduct = 2
  density = 1
  expand = 3
  formula = G4_N-HEPTANE
  name = G4_N-HEPTANE
  specific = 4
FEATURE [App::DocumentObjectGroupPython] C_element053  label="C_element : 029"  # scripted group (container) (typed FeaturePython)
  n = 6
  ref = C_element
FEATURE [App::DocumentObjectGroupPython] H_element047  label="H_element : 14"  # scripted group (container) (typed FeaturePython)
  n = 14
  ref = H_element
FEATURE [App::DocumentObjectGroupPython] G4_N_HEXANE  label="G4_N-HEXANE"  # scripted group (container) (typed FeaturePython)
  Dunit = g/cm3
  Dvalue = 0.6603
  Group = -> [C_element053,H_element047]
  conduct = 2
  density = 1
  expand = 3
  formula = G4_N-HEXANE
  name = G4_N-HEXANE
  specific = 4
FEATURE [App::DocumentObjectGroupPython] C_element054  label="C_element : 22"  # scripted group (container) (typed FeaturePython)
  n = 22
  ref = C_element
FEATURE [App::DocumentObjectGroupPython] H_element048  label="H_element : 025"  # scripted group (container) (typed FeaturePython)
  n = 10
  ref = H_element
FEATURE [App::DocumentObjectGroupPython] N_element021  label="N_element : 010"  # scripted group (container) (typed FeaturePython)
  n = 2
  ref = N_element
FEATURE [App::DocumentObjectGroupPython] O_element050  label="O_element : 025"  # scripted group (container) (typed FeaturePython)
  n = 5
  ref = O_element
FEATURE [App::DocumentObjectGroupPython] G4_KAPTON  # scripted group (container) (typed FeaturePython)
  Dunit = g/cm3
  Dvalue = 1.42
  Group = -> [C_element054,H_element048,N_element021,O_element050]
  conduct = 2
  density = 1
  expand = 3
  formula = G4_KAPTON
  name = G4_KAPTON
  specific = 4
FEATURE [App::DocumentObjectGroupPython] La_element001  label="La_element : 1"  # scripted group (container) (typed FeaturePython)
  n = 1
  ref = La_element
FEATURE [App::DocumentObjectGroupPython] Br_element003  label="Br_element : 002"  # scripted group (container) (typed FeaturePython)
  n = 1
  ref = Br_element
FEATURE [App::DocumentObjectGroupPython] O_element051  label="O_element : 026"  # scripted group (container) (typed FeaturePython)
  n = 1
  ref = O_element
FEATURE [App::DocumentObjectGroupPython] G4_LANTHANUM_OXYBROMIDE  # scripted group (container) (typed FeaturePython)
  Dunit = g/cm3
  Dvalue = 6.28
  Group = -> [La_element001,Br_element003,O_element051]
  conduct = 2
  density = 1
  expand = 3
  formula = G4_LANTHANUM_OXYBROMIDE
  name = G4_LANTHANUM_OXYBROMIDE
  specific = 4
FEATURE [App::DocumentObjectGroupPython] La_element002  label="La_element : 2"  # scripted group (container) (typed FeaturePython)
  n = 2
  ref = La_element
FEATURE [App::DocumentObjectGroupPython] O_element052  label="O_element : 027"  # scripted group (container) (typed FeaturePython)
  n = 2
  ref = O_element
FEATURE [App::DocumentObjectGroupPython] S_element015  label="S_element : 006"  # scripted group (container) (typed FeaturePython)
  n = 1
  ref = S_element
FEATURE [App::DocumentObjectGroupPython] G4_LANTHANUM_OXYSULFIDE  # scripted group (container) (typed FeaturePython)
  Dunit = g/cm3
  Dvalue = 5.86
  Group = -> [La_element002,O_element052,S_element015]
  conduct = 2
  density = 1
  expand = 3
  formula = G4_LANTHANUM_OXYSULFIDE
  name = G4_LANTHANUM_OXYSULFIDE
  specific = 4
FEATURE [App::DocumentObjectGroupPython] O_element053  label="O_element : 0.072"  # scripted group (container) (typed FeaturePython)
  n = 0.071682
FEATURE [App::DocumentObjectGroupPython] Pb_element002  label="Pb_element : 0.928"  # scripted group (container) (typed FeaturePython)
  n = 0.928318
FEATURE [App::DocumentObjectGroupPython] G4_LEAD_OXIDE  # scripted group (container) (typed FeaturePython)
  Dunit = g/cm3
  Dvalue = 9.53
  Group = -> [O_element053,Pb_element002]
  conduct = 2
  density = 1
  expand = 3
  formula = G4_LEAD_OXIDE
  name = G4_LEAD_OXIDE
  specific = 4
FEATURE [App::DocumentObjectGroupPython] Li_element001  label="Li_element : 1"  # scripted group (container) (typed FeaturePython)
  n = 1
  ref = Li_element
FEATURE [App::DocumentObjectGroupPython] N_element022  label="N_element : 011"  # scripted group (container) (typed FeaturePython)
  n = 1
  ref = N_element
FEATURE [App::DocumentObjectGroupPython] H_element049  label="H_element : 026"  # scripted group (container) (typed FeaturePython)
  n = 2
  ref = H_element
FEATURE [App::DocumentObjectGroupPython] G4_LITHIUM_AMIDE  # scripted group (container) (typed FeaturePython)
  Dunit = g/cm3
  Dvalue = 1.178
  Group = -> [Li_element001,N_element022,H_element049]
  conduct = 2
  density = 1
  expand = 3
  formula = G4_LITHIUM_AMIDE
  name = G4_LITHIUM_AMIDE
  specific = 4
FEATURE [App::DocumentObjectGroupPython] Li_element002  label="Li_element : 2"  # scripted group (container) (typed FeaturePython)
  n = 2
  ref = Li_element
FEATURE [App::DocumentObjectGroupPython] C_element055  label="C_element : 030"  # scripted group (container) (typed FeaturePython)
  n = 1
  ref = C_element
FEATURE [App::DocumentObjectGroupPython] O_element054  label="O_element : 028"  # scripted group (container) (typed FeaturePython)
  n = 3
  ref = O_element
FEATURE [App::DocumentObjectGroupPython] G4_LITHIUM_CARBONATE  # scripted group (container) (typed FeaturePython)
  Dunit = g/cm3
  Dvalue = 2.11
  Group = -> [Li_element002,C_element055,O_element054]
  conduct = 2
  density = 1
  expand = 3
  formula = G4_LITHIUM_CARBONATE
  name = G4_LITHIUM_CARBONATE
  specific = 4
FEATURE [App::DocumentObjectGroupPython] Li_element003  label="Li_element : 003"  # scripted group (container) (typed FeaturePython)
  n = 1
  ref = Li_element
FEATURE [App::DocumentObjectGroupPython] F_element012  label="F_element : 004"  # scripted group (container) (typed FeaturePython)
  n = 1
  ref = F_element
FEATURE [App::DocumentObjectGroupPython] G4_LITHIUM_FLUORIDE  # scripted group (container) (typed FeaturePython)
  Dunit = g/cm3
  Dvalue = 2.635
  Group = -> [Li_element003,F_element012]
  conduct = 2
  density = 1
  expand = 3
  formula = G4_LITHIUM_FLUORIDE
  name = G4_LITHIUM_FLUORIDE
  specific = 4
FEATURE [App::DocumentObjectGroupPython] Li_element004  label="Li_element : 004"  # scripted group (container) (typed FeaturePython)
  n = 1
  ref = Li_element
FEATURE [App::DocumentObjectGroupPython] H_element050  label="H_element : 027"  # scripted group (container) (typed FeaturePython)
  n = 1
  ref = H_element
FEATURE [App::DocumentObjectGroupPython] G4_LITHIUM_HYDRIDE  # scripted group (container) (typed FeaturePython)
  Dunit = g/cm3
  Dvalue = 0.82
  Group = -> [Li_element004,H_element050]
  conduct = 2
  density = 1
  expand = 3
  formula = G4_LITHIUM_HYDRIDE
  name = G4_LITHIUM_HYDRIDE
  specific = 4
FEATURE [App::DocumentObjectGroupPython] Li_element005  label="Li_element : 005"  # scripted group (container) (typed FeaturePython)
  n = 1
  ref = Li_element
FEATURE [App::DocumentObjectGroupPython] I_element003  label="I_element : 002"  # scripted group (container) (typed FeaturePython)
  n = 1
  ref = I_element
FEATURE [App::DocumentObjectGroupPython] G4_LITHIUM_IODIDE  # scripted group (container) (typed FeaturePython)
  Dunit = g/cm3
  Dvalue = 3.494
  Group = -> [Li_element005,I_element003]
  conduct = 2
  density = 1
  expand = 3
  formula = G4_LITHIUM_IODIDE
  name = G4_LITHIUM_IODIDE
  specific = 4
FEATURE [App::DocumentObjectGroupPython] Li_element006  label="Li_element : 006"  # scripted group (container) (typed FeaturePython)
  n = 2
  ref = Li_element
FEATURE [App::DocumentObjectGroupPython] O_element055  label="O_element : 029"  # scripted group (container) (typed FeaturePython)
  n = 1
  ref = O_element
FEATURE [App::DocumentObjectGroupPython] G4_LITHIUM_OXIDE  # scripted group (container) (typed FeaturePython)
  Dunit = g/cm3
  Dvalue = 2.013
  Group = -> [Li_element006,O_element055]
  conduct = 2
  density = 1
  expand = 3
  formula = G4_LITHIUM_OXIDE
  name = G4_LITHIUM_OXIDE
  specific = 4
FEATURE [App::DocumentObjectGroupPython] Li_element007  label="Li_element : 007"  # scripted group (container) (typed FeaturePython)
  n = 2
  ref = Li_element
FEATURE [App::DocumentObjectGroupPython] B_element005  label="B_element : 005"  # scripted group (container) (typed FeaturePython)
  n = 4
  ref = B_element
FEATURE [App::DocumentObjectGroupPython] O_element056  label="O_element : 7"  # scripted group (container) (typed FeaturePython)
  n = 7
  ref = O_element
FEATURE [App::DocumentObjectGroupPython] G4_LITHIUM_TETRABORATE  # scripted group (container) (typed FeaturePython)
  Dunit = g/cm3
  Dvalue = 2.44
  Group = -> [Li_element007,B_element005,O_element056]
  conduct = 2
  density = 1
  expand = 3
  formula = G4_LITHIUM_TETRABORATE
  name = G4_LITHIUM_TETRABORATE
  specific = 4
FEATURE [App::DocumentObjectGroupPython] H_element051  label="H_element : 0.105"  # scripted group (container) (typed FeaturePython)
  n = 0.105
FEATURE [App::DocumentObjectGroupPython] C_element056  label="C_element : 0.083"  # scripted group (container) (typed FeaturePython)
  n = 0.083
FEATURE [App::DocumentObjectGroupPython] N_element023  label="N_element : 0.023"  # scripted group (container) (typed FeaturePython)
  n = 0.023
FEATURE [App::DocumentObjectGroupPython] O_element057  label="O_element : 0.779"  # scripted group (container) (typed FeaturePython)
  n = 0.779
FEATURE [App::DocumentObjectGroupPython] Na_element010  label="Na_element : 0.097"  # scripted group (container) (typed FeaturePython)
  n = 0.002
FEATURE [App::DocumentObjectGroupPython] P_element006  label="P_element : 0.105"  # scripted group (container) (typed FeaturePython)
  n = 0.001
FEATURE [App::DocumentObjectGroupPython] S_element016  label="S_element : 0.017"  # scripted group (container) (typed FeaturePython)
  n = 0.002
FEATURE [App::DocumentObjectGroupPython] Cl_element014  label="Cl_element : 0.587"  # scripted group (container) (typed FeaturePython)
  n = 0.003
FEATURE [App::DocumentObjectGroupPython] K_element005  label="K_element : 0.015"  # scripted group (container) (typed FeaturePython)
  n = 0.002
FEATURE [App::DocumentObjectGroupPython] G4_LUNG_ICRP  # scripted group (container) (typed FeaturePython)
  Dunit = g/cm3
  Dvalue = 1.04
  Group = -> [H_element051,C_element056,N_element023,O_element057,Na_element010,P_element006,S_element016,Cl_element014,K_element005]
  conduct = 2
  density = 1
  expand = 3
  formula = G4_LUNG_ICRP
  name = G4_LUNG_ICRP
  specific = 4
FEATURE [App::DocumentObjectGroupPython] H_element052  label="H_element : 0.116"  # scripted group (container) (typed FeaturePython)
  n = 0.114318
FEATURE [App::DocumentObjectGroupPython] C_element057  label="C_element : 0.656"  # scripted group (container) (typed FeaturePython)
  n = 0.655824
FEATURE [App::DocumentObjectGroupPython] O_element058  label="O_element : 0.092"  # scripted group (container) (typed FeaturePython)
  n = 0.0921831
FEATURE [App::DocumentObjectGroupPython] Mg_element004  label="Mg_element : 0.135"  # scripted group (container) (typed FeaturePython)
  n = 0.134792
FEATURE [App::DocumentObjectGroupPython] Ca_element013  label="Ca_element : 0.003"  # scripted group (container) (typed FeaturePython)
  n = 0.002883
FEATURE [App::DocumentObjectGroupPython] G4_M3_WAX  # scripted group (container) (typed FeaturePython)
  Dunit = g/cm3
  Dvalue = 1.05
  Group = -> [H_element052,C_element057,O_element058,Mg_element004,Ca_element013]
  conduct = 2
  density = 1
  expand = 3
  formula = G4_M3_WAX
  name = G4_M3_WAX
  specific = 4
FEATURE [App::DocumentObjectGroupPython] Mg_element005  label="Mg_element : 1"  # scripted group (container) (typed FeaturePython)
  n = 1
  ref = Mg_element
FEATURE [App::DocumentObjectGroupPython] C_element058  label="C_element : 031"  # scripted group (container) (typed FeaturePython)
  n = 1
  ref = C_element
FEATURE [App::DocumentObjectGroupPython] O_element059  label="O_element : 030"  # scripted group (container) (typed FeaturePython)
  n = 3
  ref = O_element
FEATURE [App::DocumentObjectGroupPython] G4_MAGNESIUM_CARBONATE  # scripted group (container) (typed FeaturePython)
  Dunit = g/cm3
  Dvalue = 2.958
  Group = -> [Mg_element005,C_element058,O_element059]
  conduct = 2
  density = 1
  expand = 3
  formula = G4_MAGNESIUM_CARBONATE
  name = G4_MAGNESIUM_CARBONATE
  specific = 4
FEATURE [App::DocumentObjectGroupPython] Mg_element006  label="Mg_element : 002"  # scripted group (container) (typed FeaturePython)
  n = 1
  ref = Mg_element
FEATURE [App::DocumentObjectGroupPython] F_element013  label="F_element : 005"  # scripted group (container) (typed FeaturePython)
  n = 2
  ref = F_element
FEATURE [App::DocumentObjectGroupPython] G4_MAGNESIUM_FLUORIDE  # scripted group (container) (typed FeaturePython)
  Dunit = g/cm3
  Dvalue = 3
  Group = -> [Mg_element006,F_element013]
  conduct = 2
  density = 1
  expand = 3
  formula = G4_MAGNESIUM_FLUORIDE
  name = G4_MAGNESIUM_FLUORIDE
  specific = 4
FEATURE [App::DocumentObjectGroupPython] Mg_element007  label="Mg_element : 003"  # scripted group (container) (typed FeaturePython)
  n = 1
  ref = Mg_element
FEATURE [App::DocumentObjectGroupPython] O_element060  label="O_element : 031"  # scripted group (container) (typed FeaturePython)
  n = 1
  ref = O_element
FEATURE [App::DocumentObjectGroupPython] G4_MAGNESIUM_OXIDE  # scripted group (container) (typed FeaturePython)
  Dunit = g/cm3
  Dvalue = 3.58
  Group = -> [Mg_element007,O_element060]
  conduct = 2
  density = 1
  expand = 3
  formula = G4_MAGNESIUM_OXIDE
  name = G4_MAGNESIUM_OXIDE
  specific = 4
FEATURE [App::DocumentObjectGroupPython] Mg_element008  label="Mg_element : 004"  # scripted group (container) (typed FeaturePython)
  n = 1
  ref = Mg_element
FEATURE [App::DocumentObjectGroupPython] B_element006  label="B_element : 006"  # scripted group (container) (typed FeaturePython)
  n = 4
  ref = B_element
FEATURE [App::DocumentObjectGroupPython] O_element061  label="O_element : 032"  # scripted group (container) (typed FeaturePython)
  n = 7
  ref = O_element
FEATURE [App::DocumentObjectGroupPython] G4_MAGNESIUM_TETRABORATE  # scripted group (container) (typed FeaturePython)
  Dunit = g/cm3
  Dvalue = 2.53
  Group = -> [Mg_element008,B_element006,O_element061]
  conduct = 2
  density = 1
  expand = 3
  formula = G4_MAGNESIUM_TETRABORATE
  name = G4_MAGNESIUM_TETRABORATE
  specific = 4
FEATURE [App::DocumentObjectGroupPython] Hg_element001  label="Hg_element : 1"  # scripted group (container) (typed FeaturePython)
  n = 1
  ref = Hg_element
FEATURE [App::DocumentObjectGroupPython] I_element004  label="I_element : 2"  # scripted group (container) (typed FeaturePython)
  n = 2
  ref = I_element
FEATURE [App::DocumentObjectGroupPython] G4_MERCURIC_IODIDE  # scripted group (container) (typed FeaturePython)
  Dunit = g/cm3
  Dvalue = 6.36
  Group = -> [Hg_element001,I_element004]
  conduct = 2
  density = 1
  expand = 3
  formula = G4_MERCURIC_IODIDE
  name = G4_MERCURIC_IODIDE
  specific = 4
FEATURE [App::DocumentObjectGroupPython] C_element059  label="C_element : 032"  # scripted group (container) (typed FeaturePython)
  n = 1
  ref = C_element
FEATURE [App::DocumentObjectGroupPython] H_element053  label="H_element : 028"  # scripted group (container) (typed FeaturePython)
  n = 4
  ref = H_element
FEATURE [App::DocumentObjectGroupPython] G4_METHANE  # scripted group (container) (typed FeaturePython)
  Dunit = g/cm3
  Dvalue = 0.000667151
  Group = -> [C_element059,H_element053]
  conduct = 2
  density = 1
  expand = 3
  formula = G4_METHANE
  name = G4_METHANE
  specific = 4
FEATURE [App::DocumentObjectGroupPython] C_element060  label="C_element : 033"  # scripted group (container) (typed FeaturePython)
  n = 1
  ref = C_element
FEATURE [App::DocumentObjectGroupPython] H_element054  label="H_element : 029"  # scripted group (container) (typed FeaturePython)
  n = 4
  ref = H_element
FEATURE [App::DocumentObjectGroupPython] O_element062  label="O_element : 033"  # scripted group (container) (typed FeaturePython)
  n = 1
  ref = O_element
FEATURE [App::DocumentObjectGroupPython] G4_METHANOL  # scripted group (container) (typed FeaturePython)
  Dunit = g/cm3
  Dvalue = 0.7914
  Group = -> [C_element060,H_element054,O_element062]
  conduct = 2
  density = 1
  expand = 3
  formula = G4_METHANOL
  name = G4_METHANOL
  specific = 4
FEATURE [App::DocumentObjectGroupPython] H_element055  label="H_element : 0.134"  # scripted group (container) (typed FeaturePython)
  n = 0.13404
FEATURE [App::DocumentObjectGroupPython] C_element061  label="C_element : 0.778"  # scripted group (container) (typed FeaturePython)
  n = 0.77796
FEATURE [App::DocumentObjectGroupPython] O_element063  label="O_element : 0.035"  # scripted group (container) (typed FeaturePython)
  n = 0.03502
FEATURE [App::DocumentObjectGroupPython] Mg_element009  label="Mg_element : 0.039"  # scripted group (container) (typed FeaturePython)
  n = 0.038594
FEATURE [App::DocumentObjectGroupPython] Ti_element002  label="Ti_element : 0.014"  # scripted group (container) (typed FeaturePython)
  n = 0.014386
FEATURE [App::DocumentObjectGroupPython] G4_MIX_D_WAX  # scripted group (container) (typed FeaturePython)
  Dunit = g/cm3
  Dvalue = 0.99
  Group = -> [H_element055,C_element061,O_element063,Mg_element009,Ti_element002]
  conduct = 2
  density = 1
  expand = 3
  formula = G4_MIX_D_WAX
  name = G4_MIX_D_WAX
  specific = 4
FEATURE [App::DocumentObjectGroupPython] H_element056  label="H_element : 0.135"  # scripted group (container) (typed FeaturePython)
  n = 0.081192
FEATURE [App::DocumentObjectGroupPython] C_element062  label="C_element : 0.583"  # scripted group (container) (typed FeaturePython)
  n = 0.583442
FEATURE [App::DocumentObjectGroupPython] N_element024  label="N_element : 0.018"  # scripted group (container) (typed FeaturePython)
  n = 0.017798
FEATURE [App::DocumentObjectGroupPython] O_element064  label="O_element : 0.186"  # scripted group (container) (typed FeaturePython)
  n = 0.186381
FEATURE [App::DocumentObjectGroupPython] Mg_element010  label="Mg_element : 0.130"  # scripted group (container) (typed FeaturePython)
  n = 0.130287
FEATURE [App::DocumentObjectGroupPython] Cl_element015  label="Cl_element : 0.588"  # scripted group (container) (typed FeaturePython)
  n = 0.0009
FEATURE [App::DocumentObjectGroupPython] G4_MS20_TISSUE  # scripted group (container) (typed FeaturePython)
  Dunit = g/cm3
  Dvalue = 1
  Group = -> [H_element056,C_element062,N_element024,O_element064,Mg_element010,Cl_element015]
  conduct = 2
  density = 1
  expand = 3
  formula = G4_MS20_TISSUE
  name = G4_MS20_TISSUE
  specific = 4
FEATURE [App::DocumentObjectGroupPython] H_element057  label="H_element : 0.136"  # scripted group (container) (typed FeaturePython)
  n = 0.102
FEATURE [App::DocumentObjectGroupPython] C_element063  label="C_element : 0.143"  # scripted group (container) (typed FeaturePython)
  n = 0.143
FEATURE [App::DocumentObjectGroupPython] N_element025  label="N_element : 0.034"  # scripted group (container) (typed FeaturePython)
  n = 0.034
FEATURE [App::DocumentObjectGroupPython] O_element065  label="O_element : 0.710"  # scripted group (container) (typed FeaturePython)
  n = 0.71
FEATURE [App::DocumentObjectGroupPython] Na_element011  label="Na_element : 0.098"  # scripted group (container) (typed FeaturePython)
  n = 0.001
FEATURE [App::DocumentObjectGroupPython] P_element007  label="P_element : 0.002"  # scripted group (container) (typed FeaturePython)
  n = 0.002
FEATURE [App::DocumentObjectGroupPython] S_element017  label="S_element : 0.018"  # scripted group (container) (typed FeaturePython)
  n = 0.003
FEATURE [App::DocumentObjectGroupPython] Cl_element016  label="Cl_element : 0.589"  # scripted group (container) (typed FeaturePython)
  n = 0.001
FEATURE [App::DocumentObjectGroupPython] K_element006  label="K_element : 0.004"  # scripted group (container) (typed FeaturePython)
  n = 0.004
FEATURE [App::DocumentObjectGroupPython] G4_MUSCLE_SKELETAL_ICRP  # scripted group (container) (typed FeaturePython)
  Dunit = g/cm3
  Dvalue = 1.05
  Group = -> [H_element057,C_element063,N_element025,O_element065,Na_element011,P_element007,S_element017,Cl_element016,K_element006]
  conduct = 2
  density = 1
  expand = 3
  formula = G4_MUSCLE_SKELETAL_ICRP
  name = G4_MUSCLE_SKELETAL_ICRP
  specific = 4
FEATURE [App::DocumentObjectGroupPython] H_element058  label="H_element : 0.137"  # scripted group (container) (typed FeaturePython)
  n = 0.102102
FEATURE [App::DocumentObjectGroupPython] C_element064  label="C_element : 0.123"  # scripted group (container) (typed FeaturePython)
  n = 0.123123
FEATURE [App::DocumentObjectGroupPython] N_element026  label="N_element : 0.756"  # scripted group (container) (typed FeaturePython)
  n = 0.035035
FEATURE [App::DocumentObjectGroupPython] O_element066  label="O_element : 0.730"  # scripted group (container) (typed FeaturePython)
  n = 0.72973
FEATURE [App::DocumentObjectGroupPython] Na_element012  label="Na_element : 0.099"  # scripted group (container) (typed FeaturePython)
  n = 0.001001
FEATURE [App::DocumentObjectGroupPython] P_element008  label="P_element : 0.106"  # scripted group (container) (typed FeaturePython)
  n = 0.002002
FEATURE [App::DocumentObjectGroupPython] S_element018  label="S_element : 0.019"  # scripted group (container) (typed FeaturePython)
  n = 0.004004
FEATURE [App::DocumentObjectGroupPython] K_element007  label="K_element : 0.016"  # scripted group (container) (typed FeaturePython)
  n = 0.003003
FEATURE [App::DocumentObjectGroupPython] G4_MUSCLE_STRIATED_ICRU  # scripted group (container) (typed FeaturePython)
  Dunit = g/cm3
  Dvalue = 1.04
  Group = -> [H_element058,C_element064,N_element026,O_element066,Na_element012,P_element008,S_element018,K_element007]
  conduct = 2
  density = 1
  expand = 3
  formula = G4_MUSCLE_STRIATED_ICRU
  name = G4_MUSCLE_STRIATED_ICRU
  specific = 4
FEATURE [App::DocumentObjectGroupPython] H_element059  label="H_element : 0.098"  # scripted group (container) (typed FeaturePython)
  n = 0.0982341
FEATURE [App::DocumentObjectGroupPython] C_element065  label="C_element : 0.156"  # scripted group (container) (typed FeaturePython)
  n = 0.156214
FEATURE [App::DocumentObjectGroupPython] N_element027  label="N_element : 0.757"  # scripted group (container) (typed FeaturePython)
  n = 0.035451
FEATURE [App::DocumentObjectGroupPython] O_element067  label="O_element : 0.880"  # scripted group (container) (typed FeaturePython)
  n = 0.710101
FEATURE [App::DocumentObjectGroupPython] G4_MUSCLE_WITH_SUCROSE  # scripted group (container) (typed FeaturePython)
  Dunit = g/cm3
  Dvalue = 1.11
  Group = -> [H_element059,C_element065,N_element027,O_element067]
  conduct = 2
  density = 1
  expand = 3
  formula = G4_MUSCLE_WITH_SUCROSE
  name = G4_MUSCLE_WITH_SUCROSE
  specific = 4
FEATURE [App::DocumentObjectGroupPython] H_element060  label="H_element : 0.138"  # scripted group (container) (typed FeaturePython)
  n = 0.101969
FEATURE [App::DocumentObjectGroupPython] C_element066  label="C_element : 0.120"  # scripted group (container) (typed FeaturePython)
  n = 0.120058
FEATURE [App::DocumentObjectGroupPython] N_element028  label="N_element : 0.758"  # scripted group (container) (typed FeaturePython)
  n = 0.035451
FEATURE [App::DocumentObjectGroupPython] O_element068  label="O_element : 0.743"  # scripted group (container) (typed FeaturePython)
  n = 0.742522
FEATURE [App::DocumentObjectGroupPython] G4_MUSCLE_WITHOUT_SUCROSE  # scripted group (container) (typed FeaturePython)
  Dunit = g/cm3
  Dvalue = 1.07
  Group = -> [H_element060,C_element066,N_element028,O_element068]
  conduct = 2
  density = 1
  expand = 3
  formula = G4_MUSCLE_WITHOUT_SUCROSE
  name = G4_MUSCLE_WITHOUT_SUCROSE
  specific = 4
FEATURE [App::DocumentObjectGroupPython] C_element067  label="C_element : 10"  # scripted group (container) (typed FeaturePython)
  n = 10
  ref = C_element
FEATURE [App::DocumentObjectGroupPython] H_element061  label="H_element : 030"  # scripted group (container) (typed FeaturePython)
  n = 8
  ref = H_element
FEATURE [App::DocumentObjectGroupPython] G4_NAPHTHALENE  # scripted group (container) (typed FeaturePython)
  Dunit = g/cm3
  Dvalue = 1.145
  Group = -> [C_element067,H_element061]
  conduct = 2
  density = 1
  expand = 3
  formula = G4_NAPHTHALENE
  name = G4_NAPHTHALENE
  specific = 4
FEATURE [App::DocumentObjectGroupPython] C_element068  label="C_element : 034"  # scripted group (container) (typed FeaturePython)
  n = 6
  ref = C_element
FEATURE [App::DocumentObjectGroupPython] H_element062  label="H_element : 031"  # scripted group (container) (typed FeaturePython)
  n = 5
  ref = H_element
FEATURE [App::DocumentObjectGroupPython] N_element029  label="N_element : 012"  # scripted group (container) (typed FeaturePython)
  n = 1
  ref = N_element
FEATURE [App::DocumentObjectGroupPython] O_element069  label="O_element : 034"  # scripted group (container) (typed FeaturePython)
  n = 2
  ref = O_element
FEATURE [App::DocumentObjectGroupPython] G4_NITROBENZENE  # scripted group (container) (typed FeaturePython)
  Dunit = g/cm3
  Dvalue = 1.19867
  Group = -> [C_element068,H_element062,N_element029,O_element069]
  conduct = 2
  density = 1
  expand = 3
  formula = G4_NITROBENZENE
  name = G4_NITROBENZENE
  specific = 4
FEATURE [App::DocumentObjectGroupPython] N_element030  label="N_element : 013"  # scripted group (container) (typed FeaturePython)
  n = 2
  ref = N_element
FEATURE [App::DocumentObjectGroupPython] O_element070  label="O_element : 035"  # scripted group (container) (typed FeaturePython)
  n = 1
  ref = O_element
FEATURE [App::DocumentObjectGroupPython] G4_NITROUS_OXIDE  # scripted group (container) (typed FeaturePython)
  Dunit = g/cm3
  Dvalue = 0.00183094
  Group = -> [N_element030,O_element070]
  conduct = 2
  density = 1
  expand = 3
  formula = G4_NITROUS_OXIDE
  name = G4_NITROUS_OXIDE
  specific = 4
FEATURE [App::DocumentObjectGroupPython] H_element063  label="H_element : 0.104"  # scripted group (container) (typed FeaturePython)
  n = 0.103509
FEATURE [App::DocumentObjectGroupPython] C_element069  label="C_element : 0.648"  # scripted group (container) (typed FeaturePython)
  n = 0.648416
FEATURE [App::DocumentObjectGroupPython] N_element031  label="N_element : 0.100"  # scripted group (container) (typed FeaturePython)
  n = 0.0995361
FEATURE [App::DocumentObjectGroupPython] O_element071  label="O_element : 0.149"  # scripted group (container) (typed FeaturePython)
  n = 0.148539
FEATURE [App::DocumentObjectGroupPython] G4_NYLON_8062  label="G4_NYLON-8062"  # scripted group (container) (typed FeaturePython)
  Dunit = g/cm3
  Dvalue = 1.08
  Group = -> [H_element063,C_element069,N_element031,O_element071]
  conduct = 2
  density = 1
  expand = 3
  formula = G4_NYLON-8062
  name = G4_NYLON-8062
  specific = 4
FEATURE [App::DocumentObjectGroupPython] C_element070  label="C_element : 035"  # scripted group (container) (typed FeaturePython)
  n = 6
  ref = C_element
FEATURE [App::DocumentObjectGroupPython] H_element064  label="H_element : 11"  # scripted group (container) (typed FeaturePython)
  n = 11
  ref = H_element
FEATURE [App::DocumentObjectGroupPython] N_element032  label="N_element : 014"  # scripted group (container) (typed FeaturePython)
  n = 1
  ref = N_element
FEATURE [App::DocumentObjectGroupPython] O_element072  label="O_element : 036"  # scripted group (container) (typed FeaturePython)
  n = 1
  ref = O_element
FEATURE [App::DocumentObjectGroupPython] G4_NYLON_6_6  label="G4_NYLON-6-6"  # scripted group (container) (typed FeaturePython)
  Dunit = g/cm3
  Dvalue = 1.14
  Group = -> [C_element070,H_element064,N_element032,O_element072]
  conduct = 2
  density = 1
  expand = 3
  formula = G4_NYLON-6-6
  name = G4_NYLON-6-6
  specific = 4
FEATURE [App::DocumentObjectGroupPython] H_element065  label="H_element : 0.139"  # scripted group (container) (typed FeaturePython)
  n = 0.107062
FEATURE [App::DocumentObjectGroupPython] C_element071  label="C_element : 0.680"  # scripted group (container) (typed FeaturePython)
  n = 0.680449
FEATURE [App::DocumentObjectGroupPython] N_element033  label="N_element : 0.099"  # scripted group (container) (typed FeaturePython)
  n = 0.099189
FEATURE [App::DocumentObjectGroupPython] O_element073  label="O_element : 0.113"  # scripted group (container) (typed FeaturePython)
  n = 0.1133
FEATURE [App::DocumentObjectGroupPython] G4_NYLON_6_10  label="G4_NYLON-6-10"  # scripted group (container) (typed FeaturePython)
  Dunit = g/cm3
  Dvalue = 1.14
  Group = -> [H_element065,C_element071,N_element033,O_element073]
  conduct = 2
  density = 1
  expand = 3
  formula = G4_NYLON-6-10
  name = G4_NYLON-6-10
  specific = 4
FEATURE [App::DocumentObjectGroupPython] H_element066  label="H_element : 0.140"  # scripted group (container) (typed FeaturePython)
  n = 0.115476
FEATURE [App::DocumentObjectGroupPython] C_element072  label="C_element : 0.721"  # scripted group (container) (typed FeaturePython)
  n = 0.720818
FEATURE [App::DocumentObjectGroupPython] N_element034  label="N_element : 0.076"  # scripted group (container) (typed FeaturePython)
  n = 0.0764169
FEATURE [App::DocumentObjectGroupPython] O_element074  label="O_element : 0.087"  # scripted group (container) (typed FeaturePython)
  n = 0.0872889
FEATURE [App::DocumentObjectGroupPython] G4_NYLON_11_RILSAN  label="G4_NYLON-11_RILSAN"  # scripted group (container) (typed FeaturePython)
  Dunit = g/cm3
  Dvalue = 1.425
  Group = -> [H_element066,C_element072,N_element034,O_element074]
  conduct = 2
  density = 1
  expand = 3
  formula = G4_NYLON-11_RILSAN
  name = G4_NYLON-11_RILSAN
  specific = 4
FEATURE [App::DocumentObjectGroupPython] C_element073  label="C_element : 8"  # scripted group (container) (typed FeaturePython)
  n = 8
  ref = C_element
FEATURE [App::DocumentObjectGroupPython] H_element067  label="H_element : 18"  # scripted group (container) (typed FeaturePython)
  n = 18
  ref = H_element
FEATURE [App::DocumentObjectGroupPython] G4_OCTANE  # scripted group (container) (typed FeaturePython)
  Dunit = g/cm3
  Dvalue = 0.7026
  Group = -> [C_element073,H_element067]
  conduct = 2
  density = 1
  expand = 3
  formula = G4_OCTANE
  name = G4_OCTANE
  specific = 4
FEATURE [App::DocumentObjectGroupPython] C_element074  label="C_element : 25"  # scripted group (container) (typed FeaturePython)
  n = 25
  ref = C_element
FEATURE [App::DocumentObjectGroupPython] H_element068  label="H_element : 52"  # scripted group (container) (typed FeaturePython)
  n = 52
  ref = H_element
FEATURE [App::DocumentObjectGroupPython] G4_PARAFFIN  # scripted group (container) (typed FeaturePython)
  Dunit = g/cm3
  Dvalue = 0.93
  Group = -> [C_element074,H_element068]
  conduct = 2
  density = 1
  expand = 3
  formula = G4_PARAFFIN
  name = G4_PARAFFIN
  specific = 4
FEATURE [App::DocumentObjectGroupPython] C_element075  label="C_element : 036"  # scripted group (container) (typed FeaturePython)
  n = 5
  ref = C_element
FEATURE [App::DocumentObjectGroupPython] H_element069  label="H_element : 032"  # scripted group (container) (typed FeaturePython)
  n = 12
  ref = H_element
FEATURE [App::DocumentObjectGroupPython] G4_N_PENTANE  label="G4_N-PENTANE"  # scripted group (container) (typed FeaturePython)
  Dunit = g/cm3
  Dvalue = 0.6262
  Group = -> [C_element075,H_element069]
  conduct = 2
  density = 1
  expand = 3
  formula = G4_N-PENTANE
  name = G4_N-PENTANE
  specific = 4
FEATURE [App::DocumentObjectGroupPython] H_element070  label="H_element : 0.014"  # scripted group (container) (typed FeaturePython)
  n = 0.0141
FEATURE [App::DocumentObjectGroupPython] C_element076  label="C_element : 0.072"  # scripted group (container) (typed FeaturePython)
  n = 0.072261
FEATURE [App::DocumentObjectGroupPython] N_element035  label="N_element : 0.019"  # scripted group (container) (typed FeaturePython)
  n = 0.01932
FEATURE [App::DocumentObjectGroupPython] O_element075  label="O_element : 0.066"  # scripted group (container) (typed FeaturePython)
  n = 0.066101
FEATURE [App::DocumentObjectGroupPython] S_element019  label="S_element : 0.020"  # scripted group (container) (typed FeaturePython)
  n = 0.00189
FEATURE [App::DocumentObjectGroupPython] Br_element004  label="Br_element : 0.349"  # scripted group (container) (typed FeaturePython)
  n = 0.349103
FEATURE [App::DocumentObjectGroupPython] Ag_element001  label="Ag_element : 0.474"  # scripted group (container) (typed FeaturePython)
  n = 0.474105
FEATURE [App::DocumentObjectGroupPython] I_element005  label="I_element : 0.003"  # scripted group (container) (typed FeaturePython)
  n = 0.00312
FEATURE [App::DocumentObjectGroupPython] G4_PHOTO_EMULSION  # scripted group (container) (typed FeaturePython)
  Dunit = g/cm3
  Dvalue = 3.815
  Group = -> [H_element070,C_element076,N_element035,O_element075,S_element019,Br_element004,Ag_element001,I_element005]
  conduct = 2
  density = 1
  expand = 3
  formula = G4_PHOTO_EMULSION
  name = G4_PHOTO_EMULSION
  specific = 4
FEATURE [App::DocumentObjectGroupPython] C_element077  label="C_element : 9"  # scripted group (container) (typed FeaturePython)
  n = 9
  ref = C_element
FEATURE [App::DocumentObjectGroupPython] H_element071  label="H_element : 033"  # scripted group (container) (typed FeaturePython)
  n = 10
  ref = H_element
FEATURE [App::DocumentObjectGroupPython] G4_PLASTIC_SC_VINYLTOLUENE  # scripted group (container) (typed FeaturePython)
  Dunit = g/cm3
  Dvalue = 1.032
  Group = -> [C_element077,H_element071]
  conduct = 2
  density = 1
  expand = 3
  formula = G4_PLASTIC_SC_VINYLTOLUENE
  name = G4_PLASTIC_SC_VINYLTOLUENE
  specific = 4
FEATURE [App::DocumentObjectGroupPython] Pu_element001  label="Pu_element : 1"  # scripted group (container) (typed FeaturePython)
  n = 1
  ref = Pu_element
FEATURE [App::DocumentObjectGroupPython] O_element076  label="O_element : 037"  # scripted group (container) (typed FeaturePython)
  n = 2
  ref = O_element
FEATURE [App::DocumentObjectGroupPython] G4_PLUTONIUM_DIOXIDE  # scripted group (container) (typed FeaturePython)
  Dunit = g/cm3
  Dvalue = 11.46
  Group = -> [Pu_element001,O_element076]
  conduct = 2
  density = 1
  expand = 3
  formula = G4_PLUTONIUM_DIOXIDE
  name = G4_PLUTONIUM_DIOXIDE
  specific = 4
FEATURE [App::DocumentObjectGroupPython] C_element078  label="C_element : 037"  # scripted group (container) (typed FeaturePython)
  n = 3
  ref = C_element
FEATURE [App::DocumentObjectGroupPython] H_element072  label="H_element : 034"  # scripted group (container) (typed FeaturePython)
  n = 3
  ref = H_element
FEATURE [App::DocumentObjectGroupPython] N_element036  label="N_element : 015"  # scripted group (container) (typed FeaturePython)
  n = 1
  ref = N_element
FEATURE [App::DocumentObjectGroupPython] G4_POLYACRYLONITRILE  # scripted group (container) (typed FeaturePython)
  Dunit = g/cm3
  Dvalue = 1.17
  Group = -> [C_element078,H_element072,N_element036]
  conduct = 2
  density = 1
  expand = 3
  formula = G4_POLYACRYLONITRILE
  name = G4_POLYACRYLONITRILE
  specific = 4
FEATURE [App::DocumentObjectGroupPython] C_element079  label="C_element : 16"  # scripted group (container) (typed FeaturePython)
  n = 16
  ref = C_element
FEATURE [App::DocumentObjectGroupPython] H_element073  label="H_element : 035"  # scripted group (container) (typed FeaturePython)
  n = 14
  ref = H_element
FEATURE [App::DocumentObjectGroupPython] O_element077  label="O_element : 038"  # scripted group (container) (typed FeaturePython)
  n = 3
  ref = O_element
FEATURE [App::DocumentObjectGroupPython] G4_POLYCARBONATE  # scripted group (container) (typed FeaturePython)
  Dunit = g/cm3
  Dvalue = 1.2
  Group = -> [C_element079,H_element073,O_element077]
  conduct = 2
  density = 1
  expand = 3
  formula = G4_POLYCARBONATE
  name = G4_POLYCARBONATE
  specific = 4
FEATURE [App::DocumentObjectGroupPython] C_element080  label="C_element : 038"  # scripted group (container) (typed FeaturePython)
  n = 8
  ref = C_element
FEATURE [App::DocumentObjectGroupPython] H_element074  label="H_element : 036"  # scripted group (container) (typed FeaturePython)
  n = 7
  ref = H_element
FEATURE [App::DocumentObjectGroupPython] Cl_element017  label="Cl_element : 007"  # scripted group (container) (typed FeaturePython)
  n = 1
  ref = Cl_element
FEATURE [App::DocumentObjectGroupPython] G4_POLYCHLOROSTYRENE  # scripted group (container) (typed FeaturePython)
  Dunit = g/cm3
  Dvalue = 1.3
  Group = -> [C_element080,H_element074,Cl_element017]
  conduct = 2
  density = 1
  expand = 3
  formula = G4_POLYCHLOROSTYRENE
  name = G4_POLYCHLOROSTYRENE
  specific = 4
FEATURE [App::DocumentObjectGroupPython] C_element081  label="C_element : 039"  # scripted group (container) (typed FeaturePython)
  n = 1
  ref = C_element
FEATURE [App::DocumentObjectGroupPython] H_element075  label="H_element : 037"  # scripted group (container) (typed FeaturePython)
  n = 2
  ref = H_element
FEATURE [App::DocumentObjectGroupPython] G4_POLYETHYLENE  # scripted group (container) (typed FeaturePython)
  Dunit = g/cm3
  Dvalue = 0.94
  Group = -> [C_element081,H_element075]
  conduct = 2
  density = 1
  expand = 3
  formula = G4_POLYETHYLENE
  name = G4_POLYETHYLENE
  specific = 4
FEATURE [App::DocumentObjectGroupPython] C_element082  label="C_element : 040"  # scripted group (container) (typed FeaturePython)
  n = 10
  ref = C_element
FEATURE [App::DocumentObjectGroupPython] H_element076  label="H_element : 038"  # scripted group (container) (typed FeaturePython)
  n = 8
  ref = H_element
FEATURE [App::DocumentObjectGroupPython] O_element078  label="O_element : 039"  # scripted group (container) (typed FeaturePython)
  n = 4
  ref = O_element
FEATURE [App::DocumentObjectGroupPython] G4_MYLAR  # scripted group (container) (typed FeaturePython)
  Dunit = g/cm3
  Dvalue = 1.4
  Group = -> [C_element082,H_element076,O_element078]
  conduct = 2
  density = 1
  expand = 3
  formula = G4_MYLAR
  name = G4_MYLAR
  specific = 4
FEATURE [App::DocumentObjectGroupPython] C_element083  label="C_element : 041"  # scripted group (container) (typed FeaturePython)
  n = 5
  ref = C_element
FEATURE [App::DocumentObjectGroupPython] H_element077  label="H_element : 039"  # scripted group (container) (typed FeaturePython)
  n = 8
  ref = H_element
FEATURE [App::DocumentObjectGroupPython] O_element079  label="O_element : 040"  # scripted group (container) (typed FeaturePython)
  n = 2
  ref = O_element
FEATURE [App::DocumentObjectGroupPython] G4_PLEXIGLASS  # scripted group (container) (typed FeaturePython)
  Dunit = g/cm3
  Dvalue = 1.19
  Group = -> [C_element083,H_element077,O_element079]
  conduct = 2
  density = 1
  expand = 3
  formula = G4_PLEXIGLASS
  name = G4_PLEXIGLASS
  specific = 4
FEATURE [App::DocumentObjectGroupPython] C_element084  label="C_element : 042"  # scripted group (container) (typed FeaturePython)
  n = 1
  ref = C_element
FEATURE [App::DocumentObjectGroupPython] H_element078  label="H_element : 040"  # scripted group (container) (typed FeaturePython)
  n = 2
  ref = H_element
FEATURE [App::DocumentObjectGroupPython] O_element080  label="O_element : 041"  # scripted group (container) (typed FeaturePython)
  n = 1
  ref = O_element
FEATURE [App::DocumentObjectGroupPython] G4_POLYOXYMETHYLENE  # scripted group (container) (typed FeaturePython)
  Dunit = g/cm3
  Dvalue = 1.425
  Group = -> [C_element084,H_element078,O_element080]
  conduct = 2
  density = 1
  expand = 3
  formula = G4_POLYOXYMETHYLENE
  name = G4_POLYOXYMETHYLENE
  specific = 4
FEATURE [App::DocumentObjectGroupPython] C_element085  label="C_element : 043"  # scripted group (container) (typed FeaturePython)
  n = 2
  ref = C_element
FEATURE [App::DocumentObjectGroupPython] H_element079  label="H_element : 041"  # scripted group (container) (typed FeaturePython)
  n = 4
  ref = H_element
FEATURE [App::DocumentObjectGroupPython] G4_POLYPROPYLENE  # scripted group (container) (typed FeaturePython)
  Dunit = g/cm3
  Dvalue = 0.9
  Group = -> [C_element085,H_element079]
  conduct = 2
  density = 1
  expand = 3
  formula = G4_POLYPROPYLENE
  name = G4_POLYPROPYLENE
  specific = 4
FEATURE [App::DocumentObjectGroupPython] C_element086  label="C_element : 044"  # scripted group (container) (typed FeaturePython)
  n = 8
  ref = C_element
FEATURE [App::DocumentObjectGroupPython] H_element080  label="H_element : 042"  # scripted group (container) (typed FeaturePython)
  n = 8
  ref = H_element
FEATURE [App::DocumentObjectGroupPython] G4_POLYSTYRENE  # scripted group (container) (typed FeaturePython)
  Dunit = g/cm3
  Dvalue = 1.06
  Group = -> [C_element086,H_element080]
  conduct = 2
  density = 1
  expand = 3
  formula = G4_POLYSTYRENE
  name = G4_POLYSTYRENE
  specific = 4
FEATURE [App::DocumentObjectGroupPython] C_element087  label="C_element : 045"  # scripted group (container) (typed FeaturePython)
  n = 2
  ref = C_element
FEATURE [App::DocumentObjectGroupPython] F_element014  label="F_element : 4"  # scripted group (container) (typed FeaturePython)
  n = 4
  ref = F_element
FEATURE [App::DocumentObjectGroupPython] G4_TEFLON  # scripted group (container) (typed FeaturePython)
  Dunit = g/cm3
  Dvalue = 2.2
  Group = -> [C_element087,F_element014]
  conduct = 2
  density = 1
  expand = 3
  formula = G4_TEFLON
  name = G4_TEFLON
  specific = 4
FEATURE [App::DocumentObjectGroupPython] C_element088  label="C_element : 046"  # scripted group (container) (typed FeaturePython)
  n = 2
  ref = C_element
FEATURE [App::DocumentObjectGroupPython] F_element015  label="F_element : 006"  # scripted group (container) (typed FeaturePython)
  n = 3
  ref = F_element
FEATURE [App::DocumentObjectGroupPython] Cl_element018  label="Cl_element : 008"  # scripted group (container) (typed FeaturePython)
  n = 1
  ref = Cl_element
FEATURE [App::DocumentObjectGroupPython] G4_POLYTRIFLUOROCHLOROETHYLENE  # scripted group (container) (typed FeaturePython)
  Dunit = g/cm3
  Dvalue = 2.1
  Group = -> [C_element088,F_element015,Cl_element018]
  conduct = 2
  density = 1
  expand = 3
  formula = G4_POLYTRIFLUOROCHLOROETHYLENE
  name = G4_POLYTRIFLUOROCHLOROETHYLENE
  specific = 4
FEATURE [App::DocumentObjectGroupPython] C_element089  label="C_element : 047"  # scripted group (container) (typed FeaturePython)
  n = 4
  ref = C_element
FEATURE [App::DocumentObjectGroupPython] H_element081  label="H_element : 043"  # scripted group (container) (typed FeaturePython)
  n = 6
  ref = H_element
FEATURE [App::DocumentObjectGroupPython] O_element081  label="O_element : 042"  # scripted group (container) (typed FeaturePython)
  n = 2
  ref = O_element
FEATURE [App::DocumentObjectGroupPython] G4_POLYVINYL_ACETATE  # scripted group (container) (typed FeaturePython)
  Dunit = g/cm3
  Dvalue = 1.19
  Group = -> [C_element089,H_element081,O_element081]
  conduct = 2
  density = 1
  expand = 3
  formula = G4_POLYVINYL_ACETATE
  name = G4_POLYVINYL_ACETATE
  specific = 4
FEATURE [App::DocumentObjectGroupPython] C_element090  label="C_element : 048"  # scripted group (container) (typed FeaturePython)
  n = 2
  ref = C_element
FEATURE [App::DocumentObjectGroupPython] H_element082  label="H_element : 044"  # scripted group (container) (typed FeaturePython)
  n = 4
  ref = H_element
FEATURE [App::DocumentObjectGroupPython] O_element082  label="O_element : 043"  # scripted group (container) (typed FeaturePython)
  n = 1
  ref = O_element
FEATURE [App::DocumentObjectGroupPython] G4_POLYVINYL_ALCOHOL  # scripted group (container) (typed FeaturePython)
  Dunit = g/cm3
  Dvalue = 1.3
  Group = -> [C_element090,H_element082,O_element082]
  conduct = 2
  density = 1
  expand = 3
  formula = G4_POLYVINYL_ALCOHOL
  name = G4_POLYVINYL_ALCOHOL
  specific = 4
FEATURE [App::DocumentObjectGroupPython] C_element091  label="C_element : 049"  # scripted group (container) (typed FeaturePython)
  n = 8
  ref = C_element
FEATURE [App::DocumentObjectGroupPython] H_element083  label="H_element : 045"  # scripted group (container) (typed FeaturePython)
  n = 14
  ref = H_element
FEATURE [App::DocumentObjectGroupPython] O_element083  label="O_element : 044"  # scripted group (container) (typed FeaturePython)
  n = 2
  ref = O_element
FEATURE [App::DocumentObjectGroupPython] G4_POLYVINYL_BUTYRAL  # scripted group (container) (typed FeaturePython)
  Dunit = g/cm3
  Dvalue = 1.12
  Group = -> [C_element091,H_element083,O_element083]
  conduct = 2
  density = 1
  expand = 3
  formula = G4_POLYVINYL_BUTYRAL
  name = G4_POLYVINYL_BUTYRAL
  specific = 4
FEATURE [App::DocumentObjectGroupPython] C_element092  label="C_element : 050"  # scripted group (container) (typed FeaturePython)
  n = 2
  ref = C_element
FEATURE [App::DocumentObjectGroupPython] H_element084  label="H_element : 046"  # scripted group (container) (typed FeaturePython)
  n = 3
  ref = H_element
FEATURE [App::DocumentObjectGroupPython] Cl_element019  label="Cl_element : 009"  # scripted group (container) (typed FeaturePython)
  n = 1
  ref = Cl_element
FEATURE [App::DocumentObjectGroupPython] G4_POLYVINYL_CHLORIDE  # scripted group (container) (typed FeaturePython)
  Dunit = g/cm3
  Dvalue = 1.3
  Group = -> [C_element092,H_element084,Cl_element019]
  conduct = 2
  density = 1
  expand = 3
  formula = G4_POLYVINYL_CHLORIDE
  name = G4_POLYVINYL_CHLORIDE
  specific = 4
FEATURE [App::DocumentObjectGroupPython] C_element093  label="C_element : 051"  # scripted group (container) (typed FeaturePython)
  n = 2
  ref = C_element
FEATURE [App::DocumentObjectGroupPython] H_element085  label="H_element : 047"  # scripted group (container) (typed FeaturePython)
  n = 2
  ref = H_element
FEATURE [App::DocumentObjectGroupPython] Cl_element020  label="Cl_element : 010"  # scripted group (container) (typed FeaturePython)
  n = 2
  ref = Cl_element
FEATURE [App::DocumentObjectGroupPython] G4_POLYVINYLIDENE_CHLORIDE  # scripted group (container) (typed FeaturePython)
  Dunit = g/cm3
  Dvalue = 1.7
  Group = -> [C_element093,H_element085,Cl_element020]
  conduct = 2
  density = 1
  expand = 3
  formula = G4_POLYVINYLIDENE_CHLORIDE
  name = G4_POLYVINYLIDENE_CHLORIDE
  specific = 4
FEATURE [App::DocumentObjectGroupPython] C_element094  label="C_element : 052"  # scripted group (container) (typed FeaturePython)
  n = 2
  ref = C_element
FEATURE [App::DocumentObjectGroupPython] H_element086  label="H_element : 048"  # scripted group (container) (typed FeaturePython)
  n = 2
  ref = H_element
FEATURE [App::DocumentObjectGroupPython] F_element016  label="F_element : 007"  # scripted group (container) (typed FeaturePython)
  n = 2
  ref = F_element
FEATURE [App::DocumentObjectGroupPython] G4_POLYVINYLIDENE_FLUORIDE  # scripted group (container) (typed FeaturePython)
  Dunit = g/cm3
  Dvalue = 1.76
  Group = -> [C_element094,H_element086,F_element016]
  conduct = 2
  density = 1
  expand = 3
  formula = G4_POLYVINYLIDENE_FLUORIDE
  name = G4_POLYVINYLIDENE_FLUORIDE
  specific = 4
FEATURE [App::DocumentObjectGroupPython] C_element095  label="C_element : 053"  # scripted group (container) (typed FeaturePython)
  n = 6
  ref = C_element
FEATURE [App::DocumentObjectGroupPython] H_element087  label="H_element : 9"  # scripted group (container) (typed FeaturePython)
  n = 9
  ref = H_element
FEATURE [App::DocumentObjectGroupPython] N_element037  label="N_element : 016"  # scripted group (container) (typed FeaturePython)
  n = 1
  ref = N_element
FEATURE [App::DocumentObjectGroupPython] O_element084  label="O_element : 045"  # scripted group (container) (typed FeaturePython)
  n = 1
  ref = O_element
FEATURE [App::DocumentObjectGroupPython] G4_POLYVINYL_PYRROLIDONE  # scripted group (container) (typed FeaturePython)
  Dunit = g/cm3
  Dvalue = 1.25
  Group = -> [C_element095,H_element087,N_element037,O_element084]
  conduct = 2
  density = 1
  expand = 3
  formula = G4_POLYVINYL_PYRROLIDONE
  name = G4_POLYVINYL_PYRROLIDONE
  specific = 4
FEATURE [App::DocumentObjectGroupPython] K_element008  label="K_element : 1"  # scripted group (container) (typed FeaturePython)
  n = 1
  ref = K_element
FEATURE [App::DocumentObjectGroupPython] I_element006  label="I_element : 003"  # scripted group (container) (typed FeaturePython)
  n = 1
  ref = I_element
FEATURE [App::DocumentObjectGroupPython] G4_POTASSIUM_IODIDE  # scripted group (container) (typed FeaturePython)
  Dunit = g/cm3
  Dvalue = 3.13
  Group = -> [K_element008,I_element006]
  conduct = 2
  density = 1
  expand = 3
  formula = G4_POTASSIUM_IODIDE
  name = G4_POTASSIUM_IODIDE
  specific = 4
FEATURE [App::DocumentObjectGroupPython] K_element009  label="K_element : 2"  # scripted group (container) (typed FeaturePython)
  n = 2
  ref = K_element
FEATURE [App::DocumentObjectGroupPython] O_element085  label="O_element : 046"  # scripted group (container) (typed FeaturePython)
  n = 1
  ref = O_element
FEATURE [App::DocumentObjectGroupPython] G4_POTASSIUM_OXIDE  # scripted group (container) (typed FeaturePython)
  Dunit = g/cm3
  Dvalue = 2.32
  Group = -> [K_element009,O_element085]
  conduct = 2
  density = 1
  expand = 3
  formula = G4_POTASSIUM_OXIDE
  name = G4_POTASSIUM_OXIDE
  specific = 4
FEATURE [App::DocumentObjectGroupPython] C_element096  label="C_element : 054"  # scripted group (container) (typed FeaturePython)
  n = 3
  ref = C_element
FEATURE [App::DocumentObjectGroupPython] H_element088  label="H_element : 049"  # scripted group (container) (typed FeaturePython)
  n = 8
  ref = H_element
FEATURE [App::DocumentObjectGroupPython] G4_PROPANE  # scripted group (container) (typed FeaturePython)
  Dunit = g/cm3
  Dvalue = 0.00187939
  Group = -> [C_element096,H_element088]
  conduct = 2
  density = 1
  expand = 3
  formula = G4_PROPANE
  name = G4_PROPANE
  specific = 4
FEATURE [App::DocumentObjectGroupPython] C_element097  label="C_element : 055"  # scripted group (container) (typed FeaturePython)
  n = 3
  ref = C_element
FEATURE [App::DocumentObjectGroupPython] H_element089  label="H_element : 050"  # scripted group (container) (typed FeaturePython)
  n = 8
  ref = H_element
FEATURE [App::DocumentObjectGroupPython] G4_lPROPANE  # scripted group (container) (typed FeaturePython)
  Dunit = g/cm3
  Dvalue = 0.43
  Group = -> [C_element097,H_element089]
  conduct = 2
  density = 1
  expand = 3
  formula = G4_lPROPANE
  name = G4_lPROPANE
  specific = 4
FEATURE [App::DocumentObjectGroupPython] C_element098  label="C_element : 056"  # scripted group (container) (typed FeaturePython)
  n = 3
  ref = C_element
FEATURE [App::DocumentObjectGroupPython] H_element090  label="H_element : 051"  # scripted group (container) (typed FeaturePython)
  n = 8
  ref = H_element
FEATURE [App::DocumentObjectGroupPython] O_element086  label="O_element : 047"  # scripted group (container) (typed FeaturePython)
  n = 1
  ref = O_element
FEATURE [App::DocumentObjectGroupPython] G4_N_PROPYL_ALCOHOL  label="G4_N-PROPYL_ALCOHOL"  # scripted group (container) (typed FeaturePython)
  Dunit = g/cm3
  Dvalue = 0.8035
  Group = -> [C_element098,H_element090,O_element086]
  conduct = 2
  density = 1
  expand = 3
  formula = G4_N-PROPYL_ALCOHOL
  name = G4_N-PROPYL_ALCOHOL
  specific = 4
FEATURE [App::DocumentObjectGroupPython] C_element099  label="C_element : 057"  # scripted group (container) (typed FeaturePython)
  n = 5
  ref = C_element
FEATURE [App::DocumentObjectGroupPython] H_element091  label="H_element : 052"  # scripted group (container) (typed FeaturePython)
  n = 5
  ref = H_element
FEATURE [App::DocumentObjectGroupPython] N_element038  label="N_element : 017"  # scripted group (container) (typed FeaturePython)
  n = 1
  ref = N_element
FEATURE [App::DocumentObjectGroupPython] G4_PYRIDINE  # scripted group (container) (typed FeaturePython)
  Dunit = g/cm3
  Dvalue = 0.9819
  Group = -> [C_element099,H_element091,N_element038]
  conduct = 2
  density = 1
  expand = 3
  formula = G4_PYRIDINE
  name = G4_PYRIDINE
  specific = 4
FEATURE [App::DocumentObjectGroupPython] H_element092  label="H_element : 0.144"  # scripted group (container) (typed FeaturePython)
  n = 0.143711
FEATURE [App::DocumentObjectGroupPython] C_element100  label="C_element : 0.856"  # scripted group (container) (typed FeaturePython)
  n = 0.856289
FEATURE [App::DocumentObjectGroupPython] G4_RUBBER_BUTYL  # scripted group (container) (typed FeaturePython)
  Dunit = g/cm3
  Dvalue = 0.92
  Group = -> [H_element092,C_element100]
  conduct = 2
  density = 1
  expand = 3
  formula = G4_RUBBER_BUTYL
  name = G4_RUBBER_BUTYL
  specific = 4
FEATURE [App::DocumentObjectGroupPython] H_element093  label="H_element : 0.118"  # scripted group (container) (typed FeaturePython)
  n = 0.118371
FEATURE [App::DocumentObjectGroupPython] C_element101  label="C_element : 0.882"  # scripted group (container) (typed FeaturePython)
  n = 0.881629
FEATURE [App::DocumentObjectGroupPython] G4_RUBBER_NATURAL  # scripted group (container) (typed FeaturePython)
  Dunit = g/cm3
  Dvalue = 0.92
  Group = -> [H_element093,C_element101]
  conduct = 2
  density = 1
  expand = 3
  formula = G4_RUBBER_NATURAL
  name = G4_RUBBER_NATURAL
  specific = 4
FEATURE [App::DocumentObjectGroupPython] H_element094  label="H_element : 0.145"  # scripted group (container) (typed FeaturePython)
  n = 0.05692
FEATURE [App::DocumentObjectGroupPython] C_element102  label="C_element : 0.543"  # scripted group (container) (typed FeaturePython)
  n = 0.542646
FEATURE [App::DocumentObjectGroupPython] Cl_element021  label="Cl_element : 0.400"  # scripted group (container) (typed FeaturePython)
  n = 0.400434
FEATURE [App::DocumentObjectGroupPython] G4_RUBBER_NEOPRENE  # scripted group (container) (typed FeaturePython)
  Dunit = g/cm3
  Dvalue = 1.23
  Group = -> [H_element094,C_element102,Cl_element021]
  conduct = 2
  density = 1
  expand = 3
  formula = G4_RUBBER_NEOPRENE
  name = G4_RUBBER_NEOPRENE
  specific = 4
FEATURE [App::DocumentObjectGroupPython] Si_element006  label="Si_element : 1"  # scripted group (container) (typed FeaturePython)
  n = 1
  ref = Si_element
FEATURE [App::DocumentObjectGroupPython] O_element087  label="O_element : 048"  # scripted group (container) (typed FeaturePython)
  n = 2
  ref = O_element
FEATURE [App::DocumentObjectGroupPython] G4_SILICON_DIOXIDE  # scripted group (container) (typed FeaturePython)
  Dunit = g/cm3
  Dvalue = 2.32
  Group = -> [Si_element006,O_element087]
  conduct = 2
  density = 1
  expand = 3
  formula = G4_SILICON_DIOXIDE
  name = G4_SILICON_DIOXIDE
  specific = 4
FEATURE [App::DocumentObjectGroupPython] Ag_element002  label="Ag_element : 1"  # scripted group (container) (typed FeaturePython)
  n = 1
  ref = Ag_element
FEATURE [App::DocumentObjectGroupPython] Br_element005  label="Br_element : 003"  # scripted group (container) (typed FeaturePython)
  n = 1
  ref = Br_element
FEATURE [App::DocumentObjectGroupPython] G4_SILVER_BROMIDE  # scripted group (container) (typed FeaturePython)
  Dunit = g/cm3
  Dvalue = 6.473
  Group = -> [Ag_element002,Br_element005]
  conduct = 2
  density = 1
  expand = 3
  formula = G4_SILVER_BROMIDE
  name = G4_SILVER_BROMIDE
  specific = 4
FEATURE [App::DocumentObjectGroupPython] Ag_element003  label="Ag_element : 002"  # scripted group (container) (typed FeaturePython)
  n = 1
  ref = Ag_element
FEATURE [App::DocumentObjectGroupPython] Cl_element022  label="Cl_element : 011"  # scripted group (container) (typed FeaturePython)
  n = 1
  ref = Cl_element
FEATURE [App::DocumentObjectGroupPython] G4_SILVER_CHLORIDE  # scripted group (container) (typed FeaturePython)
  Dunit = g/cm3
  Dvalue = 5.56
  Group = -> [Ag_element003,Cl_element022]
  conduct = 2
  density = 1
  expand = 3
  formula = G4_SILVER_CHLORIDE
  name = G4_SILVER_CHLORIDE
  specific = 4
FEATURE [App::DocumentObjectGroupPython] Br_element006  label="Br_element : 0.423"  # scripted group (container) (typed FeaturePython)
  n = 0.422895
FEATURE [App::DocumentObjectGroupPython] Ag_element004  label="Ag_element : 0.574"  # scripted group (container) (typed FeaturePython)
  n = 0.573748
FEATURE [App::DocumentObjectGroupPython] I_element007  label="I_element : 0.649"  # scripted group (container) (typed FeaturePython)
  n = 0.003357
FEATURE [App::DocumentObjectGroupPython] G4_SILVER_HALIDES  # scripted group (container) (typed FeaturePython)
  Dunit = g/cm3
  Dvalue = 6.47
  Group = -> [Br_element006,Ag_element004,I_element007]
  conduct = 2
  density = 1
  expand = 3
  formula = G4_SILVER_HALIDES
  name = G4_SILVER_HALIDES
  specific = 4
FEATURE [App::DocumentObjectGroupPython] Ag_element005  label="Ag_element : 003"  # scripted group (container) (typed FeaturePython)
  n = 1
  ref = Ag_element
FEATURE [App::DocumentObjectGroupPython] I_element008  label="I_element : 004"  # scripted group (container) (typed FeaturePython)
  n = 1
  ref = I_element
FEATURE [App::DocumentObjectGroupPython] G4_SILVER_IODIDE  # scripted group (container) (typed FeaturePython)
  Dunit = g/cm3
  Dvalue = 6.01
  Group = -> [Ag_element005,I_element008]
  conduct = 2
  density = 1
  expand = 3
  formula = G4_SILVER_IODIDE
  name = G4_SILVER_IODIDE
  specific = 4
FEATURE [App::DocumentObjectGroupPython] H_element095  label="H_element : 0.100"  # scripted group (container) (typed FeaturePython)
  n = 0.1
FEATURE [App::DocumentObjectGroupPython] C_element103  label="C_element : 0.204"  # scripted group (container) (typed FeaturePython)
  n = 0.204
FEATURE [App::DocumentObjectGroupPython] N_element039  label="N_element : 0.759"  # scripted group (container) (typed FeaturePython)
  n = 0.042
FEATURE [App::DocumentObjectGroupPython] O_element088  label="O_element : 0.645"  # scripted group (container) (typed FeaturePython)
  n = 0.645
FEATURE [App::DocumentObjectGroupPython] Na_element013  label="Na_element : 0.100"  # scripted group (container) (typed FeaturePython)
  n = 0.002
FEATURE [App::DocumentObjectGroupPython] P_element009  label="P_element : 0.107"  # scripted group (container) (typed FeaturePython)
  n = 0.001
FEATURE [App::DocumentObjectGroupPython] S_element020  label="S_element : 0.021"  # scripted group (container) (typed FeaturePython)
  n = 0.002
FEATURE [App::DocumentObjectGroupPython] Cl_element023  label="Cl_element : 0.590"  # scripted group (container) (typed FeaturePython)
  n = 0.003
FEATURE [App::DocumentObjectGroupPython] K_element010  label="K_element : 0.001"  # scripted group (container) (typed FeaturePython)
  n = 0.001
FEATURE [App::DocumentObjectGroupPython] G4_SKIN_ICRP  # scripted group (container) (typed FeaturePython)
  Dunit = g/cm3
  Dvalue = 1.09
  Group = -> [H_element095,C_element103,N_element039,O_element088,Na_element013,P_element009,S_element020,Cl_element023,K_element010]
  conduct = 2
  density = 1
  expand = 3
  formula = G4_SKIN_ICRP
  name = G4_SKIN_ICRP
  specific = 4
FEATURE [App::DocumentObjectGroupPython] Na_element014  label="Na_element : 2"  # scripted group (container) (typed FeaturePython)
  n = 2
  ref = Na_element
FEATURE [App::DocumentObjectGroupPython] C_element104  label="C_element : 058"  # scripted group (container) (typed FeaturePython)
  n = 1
  ref = C_element
FEATURE [App::DocumentObjectGroupPython] O_element089  label="O_element : 049"  # scripted group (container) (typed FeaturePython)
  n = 3
  ref = O_element
FEATURE [App::DocumentObjectGroupPython] G4_SODIUM_CARBONATE  # scripted group (container) (typed FeaturePython)
  Dunit = g/cm3
  Dvalue = 2.532
  Group = -> [Na_element014,C_element104,O_element089]
  conduct = 2
  density = 1
  expand = 3
  formula = G4_SODIUM_CARBONATE
  name = G4_SODIUM_CARBONATE
  specific = 4
FEATURE [App::DocumentObjectGroupPython] Na_element015  label="Na_element : 1"  # scripted group (container) (typed FeaturePython)
  n = 1
  ref = Na_element
FEATURE [App::DocumentObjectGroupPython] I_element009  label="I_element : 005"  # scripted group (container) (typed FeaturePython)
  n = 1
  ref = I_element
FEATURE [App::DocumentObjectGroupPython] G4_SODIUM_IODIDE  # scripted group (container) (typed FeaturePython)
  Dunit = g/cm3
  Dvalue = 3.667
  Group = -> [Na_element015,I_element009]
  conduct = 2
  density = 1
  expand = 3
  formula = G4_SODIUM_IODIDE
  name = G4_SODIUM_IODIDE
  specific = 4
FEATURE [App::DocumentObjectGroupPython] Na_element016  label="Na_element : 003"  # scripted group (container) (typed FeaturePython)
  n = 2
  ref = Na_element
FEATURE [App::DocumentObjectGroupPython] O_element090  label="O_element : 050"  # scripted group (container) (typed FeaturePython)
  n = 1
  ref = O_element
FEATURE [App::DocumentObjectGroupPython] G4_SODIUM_MONOXIDE  # scripted group (container) (typed FeaturePython)
  Dunit = g/cm3
  Dvalue = 2.27
  Group = -> [Na_element016,O_element090]
  conduct = 2
  density = 1
  expand = 3
  formula = G4_SODIUM_MONOXIDE
  name = G4_SODIUM_MONOXIDE
  specific = 4
FEATURE [App::DocumentObjectGroupPython] Na_element017  label="Na_element : 004"  # scripted group (container) (typed FeaturePython)
  n = 1
  ref = Na_element
FEATURE [App::DocumentObjectGroupPython] N_element040  label="N_element : 018"  # scripted group (container) (typed FeaturePython)
  n = 1
  ref = N_element
FEATURE [App::DocumentObjectGroupPython] O_element091  label="O_element : 051"  # scripted group (container) (typed FeaturePython)
  n = 3
  ref = O_element
FEATURE [App::DocumentObjectGroupPython] G4_SODIUM_NITRATE  # scripted group (container) (typed FeaturePython)
  Dunit = g/cm3
  Dvalue = 2.261
  Group = -> [Na_element017,N_element040,O_element091]
  conduct = 2
  density = 1
  expand = 3
  formula = G4_SODIUM_NITRATE
  name = G4_SODIUM_NITRATE
  specific = 4
FEATURE [App::DocumentObjectGroupPython] C_element105  label="C_element : 059"  # scripted group (container) (typed FeaturePython)
  n = 14
  ref = C_element
FEATURE [App::DocumentObjectGroupPython] H_element096  label="H_element : 053"  # scripted group (container) (typed FeaturePython)
  n = 12
  ref = H_element
FEATURE [App::DocumentObjectGroupPython] G4_STILBENE  # scripted group (container) (typed FeaturePython)
  Dunit = g/cm3
  Dvalue = 0.9707
  Group = -> [C_element105,H_element096]
  conduct = 2
  density = 1
  expand = 3
  formula = G4_STILBENE
  name = G4_STILBENE
  specific = 4
FEATURE [App::DocumentObjectGroupPython] C_element106  label="C_element : 12"  # scripted group (container) (typed FeaturePython)
  n = 12
  ref = C_element
FEATURE [App::DocumentObjectGroupPython] H_element097  label="H_element : 22"  # scripted group (container) (typed FeaturePython)
  n = 22
  ref = H_element
FEATURE [App::DocumentObjectGroupPython] O_element092  label="O_element : 11"  # scripted group (container) (typed FeaturePython)
  n = 11
  ref = O_element
FEATURE [App::DocumentObjectGroupPython] G4_SUCROSE  # scripted group (container) (typed FeaturePython)
  Dunit = g/cm3
  Dvalue = 1.5805
  Group = -> [C_element106,H_element097,O_element092]
  conduct = 2
  density = 1
  expand = 3
  formula = G4_SUCROSE
  name = G4_SUCROSE
  specific = 4
FEATURE [App::DocumentObjectGroupPython] C_element107  label="C_element : 18"  # scripted group (container) (typed FeaturePython)
  n = 18
  ref = C_element
FEATURE [App::DocumentObjectGroupPython] H_element098  label="H_element : 054"  # scripted group (container) (typed FeaturePython)
  n = 14
  ref = H_element
FEATURE [App::DocumentObjectGroupPython] G4_TERPHENYL  # scripted group (container) (typed FeaturePython)
  Dunit = g/cm3
  Dvalue = 1.24
  Group = -> [C_element107,H_element098]
  conduct = 2
  density = 1
  expand = 3
  formula = G4_TERPHENYL
  name = G4_TERPHENYL
  specific = 4
FEATURE [App::DocumentObjectGroupPython] H_element099  label="H_element : 0.146"  # scripted group (container) (typed FeaturePython)
  n = 0.106
FEATURE [App::DocumentObjectGroupPython] C_element108  label="C_element : 0.883"  # scripted group (container) (typed FeaturePython)
  n = 0.099
FEATURE [App::DocumentObjectGroupPython] N_element041  label="N_element : 0.020"  # scripted group (container) (typed FeaturePython)
  n = 0.02
FEATURE [App::DocumentObjectGroupPython] O_element093  label="O_element : 0.766"  # scripted group (container) (typed FeaturePython)
  n = 0.766
FEATURE [App::DocumentObjectGroupPython] Na_element018  label="Na_element : 0.101"  # scripted group (container) (typed FeaturePython)
  n = 0.002
FEATURE [App::DocumentObjectGroupPython] P_element010  label="P_element : 0.108"  # scripted group (container) (typed FeaturePython)
  n = 0.001
FEATURE [App::DocumentObjectGroupPython] S_element021  label="S_element : 0.022"  # scripted group (container) (typed FeaturePython)
  n = 0.002
FEATURE [App::DocumentObjectGroupPython] Cl_element024  label="Cl_element : 0.002"  # scripted group (container) (typed FeaturePython)
  n = 0.002
FEATURE [App::DocumentObjectGroupPython] K_element011  label="K_element : 0.017"  # scripted group (container) (typed FeaturePython)
  n = 0.002
FEATURE [App::DocumentObjectGroupPython] G4_TESTIS_ICRP  # scripted group (container) (typed FeaturePython)
  Dunit = g/cm3
  Dvalue = 1.04
  Group = -> [H_element099,C_element108,N_element041,O_element093,Na_element018,P_element010,S_element021,Cl_element024,K_element011]
  conduct = 2
  density = 1
  expand = 3
  formula = G4_TESTIS_ICRP
  name = G4_TESTIS_ICRP
  specific = 4
FEATURE [App::DocumentObjectGroupPython] C_element109  label="C_element : 060"  # scripted group (container) (typed FeaturePython)
  n = 2
  ref = C_element
FEATURE [App::DocumentObjectGroupPython] Cl_element025  label="Cl_element : 012"  # scripted group (container) (typed FeaturePython)
  n = 4
  ref = Cl_element
FEATURE [App::DocumentObjectGroupPython] G4_TETRACHLOROETHYLENE  # scripted group (container) (typed FeaturePython)
  Dunit = g/cm3
  Dvalue = 1.625
  Group = -> [C_element109,Cl_element025]
  conduct = 2
  density = 1
  expand = 3
  formula = G4_TETRACHLOROETHYLENE
  name = G4_TETRACHLOROETHYLENE
  specific = 4
FEATURE [App::DocumentObjectGroupPython] Tl_element001  label="Tl_element : 1"  # scripted group (container) (typed FeaturePython)
  n = 1
  ref = Tl_element
FEATURE [App::DocumentObjectGroupPython] Cl_element026  label="Cl_element : 013"  # scripted group (container) (typed FeaturePython)
  n = 1
  ref = Cl_element
FEATURE [App::DocumentObjectGroupPython] G4_THALLIUM_CHLORIDE  # scripted group (container) (typed FeaturePython)
  Dunit = g/cm3
  Dvalue = 7.004
  Group = -> [Tl_element001,Cl_element026]
  conduct = 2
  density = 1
  expand = 3
  formula = G4_THALLIUM_CHLORIDE
  name = G4_THALLIUM_CHLORIDE
  specific = 4
FEATURE [App::DocumentObjectGroupPython] H_element100  label="H_element : 0.147"  # scripted group (container) (typed FeaturePython)
  n = 0.105
FEATURE [App::DocumentObjectGroupPython] C_element110  label="C_element : 0.256"  # scripted group (container) (typed FeaturePython)
  n = 0.256
FEATURE [App::DocumentObjectGroupPython] N_element042  label="N_element : 0.760"  # scripted group (container) (typed FeaturePython)
  n = 0.027
FEATURE [App::DocumentObjectGroupPython] O_element094  label="O_element : 0.602"  # scripted group (container) (typed FeaturePython)
  n = 0.602
FEATURE [App::DocumentObjectGroupPython] Na_element019  label="Na_element : 0.102"  # scripted group (container) (typed FeaturePython)
  n = 0.001
FEATURE [App::DocumentObjectGroupPython] P_element011  label="P_element : 0.109"  # scripted group (container) (typed FeaturePython)
  n = 0.002
FEATURE [App::DocumentObjectGroupPython] S_element022  label="S_element : 0.023"  # scripted group (container) (typed FeaturePython)
  n = 0.003
FEATURE [App::DocumentObjectGroupPython] Cl_element027  label="Cl_element : 0.591"  # scripted group (container) (typed FeaturePython)
  n = 0.002
FEATURE [App::DocumentObjectGroupPython] K_element012  label="K_element : 0.018"  # scripted group (container) (typed FeaturePython)
  n = 0.002
FEATURE [App::DocumentObjectGroupPython] G4_TISSUE_SOFT_ICRP  # scripted group (container) (typed FeaturePython)
  Dunit = g/cm3
  Dvalue = 1.03
  Group = -> [H_element100,C_element110,N_element042,O_element094,Na_element019,P_element011,S_element022,Cl_element027,K_element012]
  conduct = 2
  density = 1
  expand = 3
  formula = G4_TISSUE_SOFT_ICRP
  name = G4_TISSUE_SOFT_ICRP
  specific = 4
FEATURE [App::DocumentObjectGroupPython] H_element101  label="H_element : 0.148"  # scripted group (container) (typed FeaturePython)
  n = 0.101
FEATURE [App::DocumentObjectGroupPython] C_element111  label="C_element : 0.111"  # scripted group (container) (typed FeaturePython)
  n = 0.111
FEATURE [App::DocumentObjectGroupPython] N_element043  label="N_element : 0.026"  # scripted group (container) (typed FeaturePython)
  n = 0.026
FEATURE [App::DocumentObjectGroupPython] O_element095  label="O_element : 0.762"  # scripted group (container) (typed FeaturePython)
  n = 0.762
FEATURE [App::DocumentObjectGroupPython] G4_TISSUE_SOFT_ICRU_4  label="G4_TISSUE_SOFT_ICRU-4"  # scripted group (container) (typed FeaturePython)
  Dunit = g/cm3
  Dvalue = 1
  Group = -> [H_element101,C_element111,N_element043,O_element095]
  conduct = 2
  density = 1
  expand = 3
  formula = G4_TISSUE_SOFT_ICRU-4
  name = G4_TISSUE_SOFT_ICRU-4
  specific = 4
FEATURE [App::DocumentObjectGroupPython] H_element102  label="H_element : 0.149"  # scripted group (container) (typed FeaturePython)
  n = 0.101869
FEATURE [App::DocumentObjectGroupPython] C_element112  label="C_element : 0.456"  # scripted group (container) (typed FeaturePython)
  n = 0.456179
FEATURE [App::DocumentObjectGroupPython] N_element044  label="N_element : 0.761"  # scripted group (container) (typed FeaturePython)
  n = 0.035172
FEATURE [App::DocumentObjectGroupPython] O_element096  label="O_element : 0.407"  # scripted group (container) (typed FeaturePython)
  n = 0.40678
FEATURE [App::DocumentObjectGroupPython] G4_TISSUE_METHANE  label="G4_TISSUE-METHANE"  # scripted group (container) (typed FeaturePython)
  Dunit = g/cm3
  Dvalue = 0.00106409
  Group = -> [H_element102,C_element112,N_element044,O_element096]
  conduct = 2
  density = 1
  expand = 3
  formula = G4_TISSUE-METHANE
  name = G4_TISSUE-METHANE
  specific = 4
FEATURE [App::DocumentObjectGroupPython] H_element103  label="H_element : 0.103"  # scripted group (container) (typed FeaturePython)
  n = 0.102672
FEATURE [App::DocumentObjectGroupPython] C_element113  label="C_element : 0.569"  # scripted group (container) (typed FeaturePython)
  n = 0.56894
FEATURE [App::DocumentObjectGroupPython] N_element045  label="N_element : 0.762"  # scripted group (container) (typed FeaturePython)
  n = 0.035022
FEATURE [App::DocumentObjectGroupPython] O_element097  label="O_element : 0.293"  # scripted group (container) (typed FeaturePython)
  n = 0.293366
FEATURE [App::DocumentObjectGroupPython] G4_TISSUE_PROPANE  label="G4_TISSUE-PROPANE"  # scripted group (container) (typed FeaturePython)
  Dunit = g/cm3
  Dvalue = 0.00182628
  Group = -> [H_element103,C_element113,N_element045,O_element097]
  conduct = 2
  density = 1
  expand = 3
  formula = G4_TISSUE-PROPANE
  name = G4_TISSUE-PROPANE
  specific = 4
FEATURE [App::DocumentObjectGroupPython] Ti_element003  label="Ti_element : 1"  # scripted group (container) (typed FeaturePython)
  n = 1
  ref = Ti_element
FEATURE [App::DocumentObjectGroupPython] O_element098  label="O_element : 052"  # scripted group (container) (typed FeaturePython)
  n = 2
  ref = O_element
FEATURE [App::DocumentObjectGroupPython] G4_TITANIUM_DIOXIDE  # scripted group (container) (typed FeaturePython)
  Dunit = g/cm3
  Dvalue = 4.26
  Group = -> [Ti_element003,O_element098]
  conduct = 2
  density = 1
  expand = 3
  formula = G4_TITANIUM_DIOXIDE
  name = G4_TITANIUM_DIOXIDE
  specific = 4
FEATURE [App::DocumentObjectGroupPython] C_element114  label="C_element : 061"  # scripted group (container) (typed FeaturePython)
  n = 7
  ref = C_element
FEATURE [App::DocumentObjectGroupPython] H_element104  label="H_element : 055"  # scripted group (container) (typed FeaturePython)
  n = 8
  ref = H_element
FEATURE [App::DocumentObjectGroupPython] G4_TOLUENE  # scripted group (container) (typed FeaturePython)
  Dunit = g/cm3
  Dvalue = 0.8669
  Group = -> [C_element114,H_element104]
  conduct = 2
  density = 1
  expand = 3
  formula = G4_TOLUENE
  name = G4_TOLUENE
  specific = 4
FEATURE [App::DocumentObjectGroupPython] C_element115  label="C_element : 062"  # scripted group (container) (typed FeaturePython)
  n = 2
  ref = C_element
FEATURE [App::DocumentObjectGroupPython] H_element105  label="H_element : 056"  # scripted group (container) (typed FeaturePython)
  n = 1
  ref = H_element
FEATURE [App::DocumentObjectGroupPython] Cl_element028  label="Cl_element : 014"  # scripted group (container) (typed FeaturePython)
  n = 3
  ref = Cl_element
FEATURE [App::DocumentObjectGroupPython] G4_TRICHLOROETHYLENE  # scripted group (container) (typed FeaturePython)
  Dunit = g/cm3
  Dvalue = 1.46
  Group = -> [C_element115,H_element105,Cl_element028]
  conduct = 2
  density = 1
  expand = 3
  formula = G4_TRICHLOROETHYLENE
  name = G4_TRICHLOROETHYLENE
  specific = 4
FEATURE [App::DocumentObjectGroupPython] C_element116  label="C_element : 063"  # scripted group (container) (typed FeaturePython)
  n = 6
  ref = C_element
FEATURE [App::DocumentObjectGroupPython] H_element106  label="H_element : 15"  # scripted group (container) (typed FeaturePython)
  n = 15
  ref = H_element
FEATURE [App::DocumentObjectGroupPython] O_element099  label="O_element : 053"  # scripted group (container) (typed FeaturePython)
  n = 4
  ref = O_element
FEATURE [App::DocumentObjectGroupPython] P_element012  label="P_element : 1"  # scripted group (container) (typed FeaturePython)
  n = 1
  ref = P_element
FEATURE [App::DocumentObjectGroupPython] G4_TRIETHYL_PHOSPHATE  # scripted group (container) (typed FeaturePython)
  Dunit = g/cm3
  Dvalue = 1.07
  Group = -> [C_element116,H_element106,O_element099,P_element012]
  conduct = 2
  density = 1
  expand = 3
  formula = G4_TRIETHYL_PHOSPHATE
  name = G4_TRIETHYL_PHOSPHATE
  specific = 4
FEATURE [App::DocumentObjectGroupPython] W_element003  label="W_element : 003"  # scripted group (container) (typed FeaturePython)
  n = 1
  ref = W_element
FEATURE [App::DocumentObjectGroupPython] F_element017  label="F_element : 6"  # scripted group (container) (typed FeaturePython)
  n = 6
  ref = F_element
FEATURE [App::DocumentObjectGroupPython] G4_TUNGSTEN_HEXAFLUORIDE  # scripted group (container) (typed FeaturePython)
  Dunit = g/cm3
  Dvalue = 2.4
  Group = -> [W_element003,F_element017]
  conduct = 2
  density = 1
  expand = 3
  formula = G4_TUNGSTEN_HEXAFLUORIDE
  name = G4_TUNGSTEN_HEXAFLUORIDE
  specific = 4
FEATURE [App::DocumentObjectGroupPython] U_element001  label="U_element : 1"  # scripted group (container) (typed FeaturePython)
  n = 1
  ref = U_element
FEATURE [App::DocumentObjectGroupPython] C_element117  label="C_element : 064"  # scripted group (container) (typed FeaturePython)
  n = 2
  ref = C_element
FEATURE [App::DocumentObjectGroupPython] G4_URANIUM_DICARBIDE  # scripted group (container) (typed FeaturePython)
  Dunit = g/cm3
  Dvalue = 11.28
  Group = -> [U_element001,C_element117]
  conduct = 2
  density = 1
  expand = 3
  formula = G4_URANIUM_DICARBIDE
  name = G4_URANIUM_DICARBIDE
  specific = 4
FEATURE [App::DocumentObjectGroupPython] U_element002  label="U_element : 002"  # scripted group (container) (typed FeaturePython)
  n = 1
  ref = U_element
FEATURE [App::DocumentObjectGroupPython] C_element118  label="C_element : 065"  # scripted group (container) (typed FeaturePython)
  n = 1
  ref = C_element
FEATURE [App::DocumentObjectGroupPython] G4_URANIUM_MONOCARBIDE  # scripted group (container) (typed FeaturePython)
  Dunit = g/cm3
  Dvalue = 13.63
  Group = -> [U_element002,C_element118]
  conduct = 2
  density = 1
  expand = 3
  formula = G4_URANIUM_MONOCARBIDE
  name = G4_URANIUM_MONOCARBIDE
  specific = 4
FEATURE [App::DocumentObjectGroupPython] U_element003  label="U_element : 003"  # scripted group (container) (typed FeaturePython)
  n = 1
  ref = U_element
FEATURE [App::DocumentObjectGroupPython] O_element100  label="O_element : 054"  # scripted group (container) (typed FeaturePython)
  n = 2
  ref = O_element
FEATURE [App::DocumentObjectGroupPython] G4_URANIUM_OXIDE  # scripted group (container) (typed FeaturePython)
  Dunit = g/cm3
  Dvalue = 10.96
  Group = -> [U_element003,O_element100]
  conduct = 2
  density = 1
  expand = 3
  formula = G4_URANIUM_OXIDE
  name = G4_URANIUM_OXIDE
  specific = 4
FEATURE [App::DocumentObjectGroupPython] C_element119  label="C_element : 066"  # scripted group (container) (typed FeaturePython)
  n = 1
  ref = C_element
FEATURE [App::DocumentObjectGroupPython] H_element107  label="H_element : 057"  # scripted group (container) (typed FeaturePython)
  n = 4
  ref = H_element
FEATURE [App::DocumentObjectGroupPython] N_element046  label="N_element : 019"  # scripted group (container) (typed FeaturePython)
  n = 2
  ref = N_element
FEATURE [App::DocumentObjectGroupPython] O_element101  label="O_element : 055"  # scripted group (container) (typed FeaturePython)
  n = 1
  ref = O_element
FEATURE [App::DocumentObjectGroupPython] G4_UREA  # scripted group (container) (typed FeaturePython)
  Dunit = g/cm3
  Dvalue = 1.323
  Group = -> [C_element119,H_element107,N_element046,O_element101]
  conduct = 2
  density = 1
  expand = 3
  formula = G4_UREA
  name = G4_UREA
  specific = 4
FEATURE [App::DocumentObjectGroupPython] C_element120  label="C_element : 067"  # scripted group (container) (typed FeaturePython)
  n = 5
  ref = C_element
FEATURE [App::DocumentObjectGroupPython] H_element108  label="H_element : 058"  # scripted group (container) (typed FeaturePython)
  n = 11
  ref = H_element
FEATURE [App::DocumentObjectGroupPython] N_element047  label="N_element : 020"  # scripted group (container) (typed FeaturePython)
  n = 1
  ref = N_element
FEATURE [App::DocumentObjectGroupPython] O_element102  label="O_element : 056"  # scripted group (container) (typed FeaturePython)
  n = 2
  ref = O_element
FEATURE [App::DocumentObjectGroupPython] G4_VALINE  # scripted group (container) (typed FeaturePython)
  Dunit = g/cm3
  Dvalue = 1.23
  Group = -> [C_element120,H_element108,N_element047,O_element102]
  conduct = 2
  density = 1
  expand = 3
  formula = G4_VALINE
  name = G4_VALINE
  specific = 4
FEATURE [App::DocumentObjectGroupPython] H_element109  label="H_element : 0.009"  # scripted group (container) (typed FeaturePython)
  n = 0.009417
FEATURE [App::DocumentObjectGroupPython] C_element121  label="C_element : 0.281"  # scripted group (container) (typed FeaturePython)
  n = 0.280555
FEATURE [App::DocumentObjectGroupPython] F_element018  label="F_element : 0.710"  # scripted group (container) (typed FeaturePython)
  n = 0.710028
FEATURE [App::DocumentObjectGroupPython] G4_VITON  # scripted group (container) (typed FeaturePython)
  Dunit = g/cm3
  Dvalue = 1.8
  Group = -> [H_element109,C_element121,F_element018]
  conduct = 2
  density = 1
  expand = 3
  formula = G4_VITON
  name = G4_VITON
  specific = 4
FEATURE [App::DocumentObjectGroupPython] H_element110  label="H_element : 059"  # scripted group (container) (typed FeaturePython)
  n = 2
  ref = H_element
FEATURE [App::DocumentObjectGroupPython] O_element103  label="O_element : 057"  # scripted group (container) (typed FeaturePython)
  n = 1
  ref = O_element
FEATURE [App::DocumentObjectGroupPython] G4_WATER  # scripted group (container) (typed FeaturePython)
  Dunit = g/cm3
  Dvalue = 1
  Group = -> [H_element110,O_element103]
  conduct = 2
  density = 1
  expand = 3
  formula = G4_WATER
  name = G4_WATER
  specific = 4
FEATURE [App::DocumentObjectGroupPython] H_element111  label="H_element : 060"  # scripted group (container) (typed FeaturePython)
  n = 2
  ref = H_element
FEATURE [App::DocumentObjectGroupPython] O_element104  label="O_element : 058"  # scripted group (container) (typed FeaturePython)
  n = 1
  ref = O_element
FEATURE [App::DocumentObjectGroupPython] G4_WATER_VAPOR  # scripted group (container) (typed FeaturePython)
  Dunit = g/cm3
  Dvalue = 0.000756182
  Group = -> [H_element111,O_element104]
  conduct = 2
  density = 1
  expand = 3
  formula = G4_WATER_VAPOR
  name = G4_WATER_VAPOR
  specific = 4
FEATURE [App::DocumentObjectGroupPython] C_element122  label="C_element : 068"  # scripted group (container) (typed FeaturePython)
  n = 8
  ref = C_element
FEATURE [App::DocumentObjectGroupPython] H_element112  label="H_element : 061"  # scripted group (container) (typed FeaturePython)
  n = 10
  ref = H_element
FEATURE [App::DocumentObjectGroupPython] G4_XYLENE  # scripted group (container) (typed FeaturePython)
  Dunit = g/cm3
  Dvalue = 0.87
  Group = -> [C_element122,H_element112]
  conduct = 2
  density = 1
  expand = 3
  formula = G4_XYLENE
  name = G4_XYLENE
  specific = 4
FEATURE [App::DocumentObjectGroupPython] C_element123  label="C_element : 069"  # scripted group (container) (typed FeaturePython)
  n = 1
  ref = C_element
FEATURE [App::DocumentObjectGroupPython] G4_GRAPHITE  # scripted group (container) (typed FeaturePython)
  Dunit = g/cm3
  Dvalue = 2.21
  Group = -> [C_element123]
  conduct = 2
  density = 1
  expand = 3
  formula = G4_GRAPHITE
  name = G4_GRAPHITE
  specific = 4
FEATURE [App::DocumentObjectGroupPython] NIST  # scripted group (container) (typed FeaturePython)
  Group = -> [G4_A_150_TISSUE,G4_ACETONE,G4_ACETYLENE,G4_ADENINE,G4_ADIPOSE_TISSUE_ICRP,G4_AIR,G4_ALANINE,G4_ALUMINUM_OXIDE,G4_AMBER,G4_AMMONIA,G4_ANILINE,G4_ANTHRACENE,G4_B_100_BONE,G4_BAKELITE,G4_BARIUM_FLUORIDE,G4_BARIUM_SULFATE,G4_BENZENE,G4_BERYLLIUM_OXIDE,G4_BGO,G4_BLOOD_ICRP,G4_BONE_COMPACT_ICRU,G4_BONE_CORTICAL_ICRP,G4_BORON_CARBIDE,G4_BORON_OXIDE,G4_BRAIN_ICRP,G4_BUTANE,G4_N_BUTYL_ALCOHOL,G4_C_552,+152 more]
FEATURE [App::DocumentObjectGroupPython] H_element113  label="H_element : 062"  # scripted group (container) (typed FeaturePython)
  n = 1
  ref = H_element
FEATURE [App::DocumentObjectGroupPython] G4_H  # scripted group (container) (typed FeaturePython)
  Dunit = g/cm3
  Dvalue = 8.3748e-05
  Group = -> [H_element113]
  conduct = 2
  density = 1
  expand = 3
  formula = H
  name = G4_H
  specific = 4
FEATURE [App::DocumentObjectGroupPython] He_element001  label="He_element : 1"  # scripted group (container) (typed FeaturePython)
  n = 1
  ref = He_element
FEATURE [App::DocumentObjectGroupPython] G4_He  # scripted group (container) (typed FeaturePython)
  Dunit = g/cm3
  Dvalue = 0.000166322
  Group = -> [He_element001]
  conduct = 2
  density = 1
  expand = 3
  formula = He
  name = G4_He
  specific = 4
FEATURE [App::DocumentObjectGroupPython] Li_element008  label="Li_element : 008"  # scripted group (container) (typed FeaturePython)
  n = 1
  ref = Li_element
FEATURE [App::DocumentObjectGroupPython] G4_Li  # scripted group (container) (typed FeaturePython)
  Dunit = g/cm3
  Dvalue = 0.534
  Group = -> [Li_element008]
  conduct = 2
  density = 1
  expand = 3
  formula = Li
  name = G4_Li
  specific = 4
FEATURE [App::DocumentObjectGroupPython] Be_element002  label="Be_element : 002"  # scripted group (container) (typed FeaturePython)
  n = 1
  ref = Be_element
FEATURE [App::DocumentObjectGroupPython] G4_Be  # scripted group (container) (typed FeaturePython)
  Dunit = g/cm3
  Dvalue = 1.848
  Group = -> [Be_element002]
  conduct = 2
  density = 1
  expand = 3
  formula = Be
  name = G4_Be
  specific = 4
FEATURE [App::DocumentObjectGroupPython] B_element007  label="B_element : 007"  # scripted group (container) (typed FeaturePython)
  n = 1
  ref = B_element
FEATURE [App::DocumentObjectGroupPython] G4_B  # scripted group (container) (typed FeaturePython)
  Dunit = g/cm3
  Dvalue = 2.37
  Group = -> [B_element007]
  conduct = 2
  density = 1
  expand = 3
  formula = B
  name = G4_B
  specific = 4
FEATURE [App::DocumentObjectGroupPython] C_element124  label="C_element : 070"  # scripted group (container) (typed FeaturePython)
  n = 1
  ref = C_element
FEATURE [App::DocumentObjectGroupPython] G4_C  # scripted group (container) (typed FeaturePython)
  Dunit = g/cm3
  Dvalue = 2
  Group = -> [C_element124]
  conduct = 2
  density = 1
  expand = 3
  formula = C
  name = G4_C
  specific = 4
FEATURE [App::DocumentObjectGroupPython] N_element048  label="N_element : 021"  # scripted group (container) (typed FeaturePython)
  n = 1
  ref = N_element
FEATURE [App::DocumentObjectGroupPython] G4_N  # scripted group (container) (typed FeaturePython)
  Dunit = g/cm3
  Dvalue = 0.0011652
  Group = -> [N_element048]
  conduct = 2
  density = 1
  expand = 3
  formula = N
  name = G4_N
  specific = 4
FEATURE [App::DocumentObjectGroupPython] O_element105  label="O_element : 059"  # scripted group (container) (typed FeaturePython)
  n = 1
  ref = O_element
FEATURE [App::DocumentObjectGroupPython] G4_O  # scripted group (container) (typed FeaturePython)
  Dunit = g/cm3
  Dvalue = 0.00133151
  Group = -> [O_element105]
  conduct = 2
  density = 1
  expand = 3
  formula = O
  name = G4_O
  specific = 4
FEATURE [App::DocumentObjectGroupPython] F_element019  label="F_element : 008"  # scripted group (container) (typed FeaturePython)
  n = 1
  ref = F_element
FEATURE [App::DocumentObjectGroupPython] G4_F  # scripted group (container) (typed FeaturePython)
  Dunit = g/cm3
  Dvalue = 0.00158029
  Group = -> [F_element019]
  conduct = 2
  density = 1
  expand = 3
  formula = F
  name = G4_F
  specific = 4
FEATURE [App::DocumentObjectGroupPython] Ne_element001  label="Ne_element : 1"  # scripted group (container) (typed FeaturePython)
  n = 1
  ref = Ne_element
FEATURE [App::DocumentObjectGroupPython] G4_Ne  # scripted group (container) (typed FeaturePython)
  Dunit = g/cm3
  Dvalue = 0.000838505
  Group = -> [Ne_element001]
  conduct = 2
  density = 1
  expand = 3
  formula = Ne
  name = G4_Ne
  specific = 4
FEATURE [App::DocumentObjectGroupPython] Na_element020  label="Na_element : 005"  # scripted group (container) (typed FeaturePython)
  n = 1
  ref = Na_element
FEATURE [App::DocumentObjectGroupPython] G4_Na  # scripted group (container) (typed FeaturePython)
  Dunit = g/cm3
  Dvalue = 0.971
  Group = -> [Na_element020]
  conduct = 2
  density = 1
  expand = 3
  formula = Na
  name = G4_Na
  specific = 4
FEATURE [App::DocumentObjectGroupPython] Mg_element011  label="Mg_element : 005"  # scripted group (container) (typed FeaturePython)
  n = 1
  ref = Mg_element
FEATURE [App::DocumentObjectGroupPython] G4_Mg  # scripted group (container) (typed FeaturePython)
  Dunit = g/cm3
  Dvalue = 1.74
  Group = -> [Mg_element011]
  conduct = 2
  density = 1
  expand = 3
  formula = Mg
  name = G4_Mg
  specific = 4
FEATURE [App::DocumentObjectGroupPython] Al_element004  label="Al_element : 1"  # scripted group (container) (typed FeaturePython)
  n = 1
  ref = Al_element
FEATURE [App::DocumentObjectGroupPython] G4_Al  # scripted group (container) (typed FeaturePython)
  Dunit = g/cm3
  Dvalue = 2.699
  Group = -> [Al_element004]
  conduct = 2
  density = 1
  expand = 3
  formula = Al
  name = G4_Al
  specific = 4
FEATURE [App::DocumentObjectGroupPython] Si_element007  label="Si_element : 002"  # scripted group (container) (typed FeaturePython)
  n = 1
  ref = Si_element
FEATURE [App::DocumentObjectGroupPython] G4_Si  # scripted group (container) (typed FeaturePython)
  Dunit = g/cm3
  Dvalue = 2.33
  Group = -> [Si_element007]
  conduct = 2
  density = 1
  expand = 3
  formula = Si
  name = G4_Si
  specific = 4
FEATURE [App::DocumentObjectGroupPython] P_element013  label="P_element : 002"  # scripted group (container) (typed FeaturePython)
  n = 1
  ref = P_element
FEATURE [App::DocumentObjectGroupPython] G4_P  # scripted group (container) (typed FeaturePython)
  Dunit = g/cm3
  Dvalue = 2.2
  Group = -> [P_element013]
  conduct = 2
  density = 1
  expand = 3
  formula = P
  name = G4_P
  specific = 4
FEATURE [App::DocumentObjectGroupPython] S_element023  label="S_element : 007"  # scripted group (container) (typed FeaturePython)
  n = 1
  ref = S_element
FEATURE [App::DocumentObjectGroupPython] G4_S  # scripted group (container) (typed FeaturePython)
  Dunit = g/cm3
  Dvalue = 2
  Group = -> [S_element023]
  conduct = 2
  density = 1
  expand = 3
  formula = S
  name = G4_S
  specific = 4
FEATURE [App::DocumentObjectGroupPython] Cl_element029  label="Cl_element : 015"  # scripted group (container) (typed FeaturePython)
  n = 1
  ref = Cl_element
FEATURE [App::DocumentObjectGroupPython] G4_Cl  # scripted group (container) (typed FeaturePython)
  Dunit = g/cm3
  Dvalue = 0.00299473
  Group = -> [Cl_element029]
  conduct = 2
  density = 1
  expand = 3
  formula = Cl
  name = G4_Cl
  specific = 4
FEATURE [App::DocumentObjectGroupPython] Ar_element002  label="Ar_element : 1"  # scripted group (container) (typed FeaturePython)
  n = 1
  ref = Ar_element
FEATURE [App::DocumentObjectGroupPython] G4_Ar  # scripted group (container) (typed FeaturePython)
  Dunit = g/cm3
  Dvalue = 0.00166201
  Group = -> [Ar_element002]
  conduct = 2
  density = 1
  expand = 3
  formula = Ar
  name = G4_Ar
  specific = 4
FEATURE [App::DocumentObjectGroupPython] K_element013  label="K_element : 003"  # scripted group (container) (typed FeaturePython)
  n = 1
  ref = K_element
FEATURE [App::DocumentObjectGroupPython] G4_K  # scripted group (container) (typed FeaturePython)
  Dunit = g/cm3
  Dvalue = 0.862
  Group = -> [K_element013]
  conduct = 2
  density = 1
  expand = 3
  formula = K
  name = G4_K
  specific = 4
FEATURE [App::DocumentObjectGroupPython] Ca_element014  label="Ca_element : 007"  # scripted group (container) (typed FeaturePython)
  n = 1
  ref = Ca_element
FEATURE [App::DocumentObjectGroupPython] G4_Ca  # scripted group (container) (typed FeaturePython)
  Dunit = g/cm3
  Dvalue = 1.55
  Group = -> [Ca_element014]
  conduct = 2
  density = 1
  expand = 3
  formula = Ca
  name = G4_Ca
  specific = 4
FEATURE [App::DocumentObjectGroupPython] Sc_element001  label="Sc_element : 1"  # scripted group (container) (typed FeaturePython)
  n = 1
  ref = Sc_element
FEATURE [App::DocumentObjectGroupPython] G4_Sc  # scripted group (container) (typed FeaturePython)
  Dunit = g/cm3
  Dvalue = 2.989
  Group = -> [Sc_element001]
  conduct = 2
  density = 1
  expand = 3
  formula = Sc
  name = G4_Sc
  specific = 4
FEATURE [App::DocumentObjectGroupPython] Ti_element004  label="Ti_element : 002"  # scripted group (container) (typed FeaturePython)
  n = 1
  ref = Ti_element
FEATURE [App::DocumentObjectGroupPython] G4_Ti  # scripted group (container) (typed FeaturePython)
  Dunit = g/cm3
  Dvalue = 4.54
  Group = -> [Ti_element004]
  conduct = 2
  density = 1
  expand = 3
  formula = Ti
  name = G4_Ti
  specific = 4
FEATURE [App::DocumentObjectGroupPython] V_element001  label="V_element : 1"  # scripted group (container) (typed FeaturePython)
  n = 1
  ref = V_element
FEATURE [App::DocumentObjectGroupPython] G4_V  # scripted group (container) (typed FeaturePython)
  Dunit = g/cm3
  Dvalue = 6.11
  Group = -> [V_element001]
  conduct = 2
  density = 1
  expand = 3
  formula = V
  name = G4_V
  specific = 4
FEATURE [App::DocumentObjectGroupPython] Cr_element001  label="Cr_element : 1"  # scripted group (container) (typed FeaturePython)
  n = 1
  ref = Cr_element
FEATURE [App::DocumentObjectGroupPython] G4_Cr  # scripted group (container) (typed FeaturePython)
  Dunit = g/cm3
  Dvalue = 7.18
  Group = -> [Cr_element001]
  conduct = 2
  density = 1
  expand = 3
  formula = Cr
  name = G4_Cr
  specific = 4
FEATURE [App::DocumentObjectGroupPython] Mn_element001  label="Mn_element : 1"  # scripted group (container) (typed FeaturePython)
  n = 1
  ref = Mn_element
FEATURE [App::DocumentObjectGroupPython] G4_Mn  # scripted group (container) (typed FeaturePython)
  Dunit = g/cm3
  Dvalue = 7.44
  Group = -> [Mn_element001]
  conduct = 2
  density = 1
  expand = 3
  formula = Mn
  name = G4_Mn
  specific = 4
FEATURE [App::DocumentObjectGroupPython] Fe_element007  label="Fe_element : 004"  # scripted group (container) (typed FeaturePython)
  n = 1
  ref = Fe_element
FEATURE [App::DocumentObjectGroupPython] G4_Fe  # scripted group (container) (typed FeaturePython)
  Dunit = g/cm3
  Dvalue = 7.874
  Group = -> [Fe_element007]
  conduct = 2
  density = 1
  expand = 3
  formula = Fe
  name = G4_Fe
  specific = 4
FEATURE [App::DocumentObjectGroupPython] Co_element001  label="Co_element : 1"  # scripted group (container) (typed FeaturePython)
  n = 1
  ref = Co_element
FEATURE [App::DocumentObjectGroupPython] G4_Co  # scripted group (container) (typed FeaturePython)
  Dunit = g/cm3
  Dvalue = 8.9
  Group = -> [Co_element001]
  conduct = 2
  density = 1
  expand = 3
  formula = Co
  name = G4_Co
  specific = 4
FEATURE [App::DocumentObjectGroupPython] Ni_element001  label="Ni_element : 1"  # scripted group (container) (typed FeaturePython)
  n = 1
  ref = Ni_element
FEATURE [App::DocumentObjectGroupPython] G4_Ni  # scripted group (container) (typed FeaturePython)
  Dunit = g/cm3
  Dvalue = 8.902
  Group = -> [Ni_element001]
  conduct = 2
  density = 1
  expand = 3
  formula = Ni
  name = G4_Ni
  specific = 4
FEATURE [App::DocumentObjectGroupPython] Cu_element001  label="Cu_element : 1"  # scripted group (container) (typed FeaturePython)
  n = 1
  ref = Cu_element
FEATURE [App::DocumentObjectGroupPython] G4_Cu  # scripted group (container) (typed FeaturePython)
  Dunit = g/cm3
  Dvalue = 8.96
  Group = -> [Cu_element001]
  conduct = 2
  density = 1
  expand = 3
  formula = Cu
  name = G4_Cu
  specific = 4
FEATURE [App::DocumentObjectGroupPython] Zn_element001  label="Zn_element : 1"  # scripted group (container) (typed FeaturePython)
  n = 1
  ref = Zn_element
FEATURE [App::DocumentObjectGroupPython] G4_Zn  # scripted group (container) (typed FeaturePython)
  Dunit = g/cm3
  Dvalue = 7.133
  Group = -> [Zn_element001]
  conduct = 2
  density = 1
  expand = 3
  formula = Zn
  name = G4_Zn
  specific = 4
FEATURE [App::DocumentObjectGroupPython] Ga_element002  label="Ga_element : 002"  # scripted group (container) (typed FeaturePython)
  n = 1
  ref = Ga_element
FEATURE [App::DocumentObjectGroupPython] G4_Ga  # scripted group (container) (typed FeaturePython)
  Dunit = g/cm3
  Dvalue = 5.904
  Group = -> [Ga_element002]
  conduct = 2
  density = 1
  expand = 3
  formula = Ga
  name = G4_Ga
  specific = 4
FEATURE [App::DocumentObjectGroupPython] Ge_element002  label="Ge_element : 1"  # scripted group (container) (typed FeaturePython)
  n = 1
  ref = Ge_element
FEATURE [App::DocumentObjectGroupPython] G4_Ge  # scripted group (container) (typed FeaturePython)
  Dunit = g/cm3
  Dvalue = 5.323
  Group = -> [Ge_element002]
  conduct = 2
  density = 1
  expand = 3
  formula = Ge
  name = G4_Ge
  specific = 4
FEATURE [App::DocumentObjectGroupPython] As_element003  label="As_element : 002"  # scripted group (container) (typed FeaturePython)
  n = 1
  ref = As_element
FEATURE [App::DocumentObjectGroupPython] G4_As  # scripted group (container) (typed FeaturePython)
  Dunit = g/cm3
  Dvalue = 5.73
  Group = -> [As_element003]
  conduct = 2
  density = 1
  expand = 3
  formula = As
  name = G4_As
  specific = 4
FEATURE [App::DocumentObjectGroupPython] Se_element001  label="Se_element : 1"  # scripted group (container) (typed FeaturePython)
  n = 1
  ref = Se_element
FEATURE [App::DocumentObjectGroupPython] G4_Se  # scripted group (container) (typed FeaturePython)
  Dunit = g/cm3
  Dvalue = 4.5
  Group = -> [Se_element001]
  conduct = 2
  density = 1
  expand = 3
  formula = Se
  name = G4_Se
  specific = 4
FEATURE [App::DocumentObjectGroupPython] Br_element007  label="Br_element : 004"  # scripted group (container) (typed FeaturePython)
  n = 1
  ref = Br_element
FEATURE [App::DocumentObjectGroupPython] G4_Br  # scripted group (container) (typed FeaturePython)
  Dunit = g/cm3
  Dvalue = 0.0070721
  Group = -> [Br_element007]
  conduct = 2
  density = 1
  expand = 3
  formula = Br
  name = G4_Br
  specific = 4
FEATURE [App::DocumentObjectGroupPython] Kr_element001  label="Kr_element : 1"  # scripted group (container) (typed FeaturePython)
  n = 1
  ref = Kr_element
FEATURE [App::DocumentObjectGroupPython] G4_Kr  # scripted group (container) (typed FeaturePython)
  Dunit = g/cm3
  Dvalue = 0.00347832
  Group = -> [Kr_element001]
  conduct = 2
  density = 1
  expand = 3
  formula = Kr
  name = G4_Kr
  specific = 4
FEATURE [App::DocumentObjectGroupPython] Rb_element001  label="Rb_element : 1"  # scripted group (container) (typed FeaturePython)
  n = 1
  ref = Rb_element
FEATURE [App::DocumentObjectGroupPython] G4_Rb  # scripted group (container) (typed FeaturePython)
  Dunit = g/cm3
  Dvalue = 1.532
  Group = -> [Rb_element001]
  conduct = 2
  density = 1
  expand = 3
  formula = Rb
  name = G4_Rb
  specific = 4
FEATURE [App::DocumentObjectGroupPython] Sr_element001  label="Sr_element : 1"  # scripted group (container) (typed FeaturePython)
  n = 1
  ref = Sr_element
FEATURE [App::DocumentObjectGroupPython] G4_Sr  # scripted group (container) (typed FeaturePython)
  Dunit = g/cm3
  Dvalue = 2.54
  Group = -> [Sr_element001]
  conduct = 2
  density = 1
  expand = 3
  formula = Sr
  name = G4_Sr
  specific = 4
FEATURE [App::DocumentObjectGroupPython] Y_element001  label="Y_element : 1"  # scripted group (container) (typed FeaturePython)
  n = 1
  ref = Y_element
FEATURE [App::DocumentObjectGroupPython] G4_Y  # scripted group (container) (typed FeaturePython)
  Dunit = g/cm3
  Dvalue = 4.469
  Group = -> [Y_element001]
  conduct = 2
  density = 1
  expand = 3
  formula = Y
  name = G4_Y
  specific = 4
FEATURE [App::DocumentObjectGroupPython] Zr_element001  label="Zr_element : 1"  # scripted group (container) (typed FeaturePython)
  n = 1
  ref = Zr_element
FEATURE [App::DocumentObjectGroupPython] G4_Zr  # scripted group (container) (typed FeaturePython)
  Dunit = g/cm3
  Dvalue = 6.506
  Group = -> [Zr_element001]
  conduct = 2
  density = 1
  expand = 3
  formula = Zr
  name = G4_Zr
  specific = 4
FEATURE [App::DocumentObjectGroupPython] Nb_element001  label="Nb_element : 1"  # scripted group (container) (typed FeaturePython)
  n = 1
  ref = Nb_element
FEATURE [App::DocumentObjectGroupPython] G4_Nb  # scripted group (container) (typed FeaturePython)
  Dunit = g/cm3
  Dvalue = 8.57
  Group = -> [Nb_element001]
  conduct = 2
  density = 1
  expand = 3
  formula = Nb
  name = G4_Nb
  specific = 4
FEATURE [App::DocumentObjectGroupPython] Mo_element001  label="Mo_element : 1"  # scripted group (container) (typed FeaturePython)
  n = 1
  ref = Mo_element
FEATURE [App::DocumentObjectGroupPython] G4_Mo  # scripted group (container) (typed FeaturePython)
  Dunit = g/cm3
  Dvalue = 10.22
  Group = -> [Mo_element001]
  conduct = 2
  density = 1
  expand = 3
  formula = Mo
  name = G4_Mo
  specific = 4
FEATURE [App::DocumentObjectGroupPython] Tc_element001  label="Tc_element : 1"  # scripted group (container) (typed FeaturePython)
  n = 1
  ref = Tc_element
FEATURE [App::DocumentObjectGroupPython] G4_Tc  # scripted group (container) (typed FeaturePython)
  Dunit = g/cm3
  Dvalue = 11.5
  Group = -> [Tc_element001]
  conduct = 2
  density = 1
  expand = 3
  formula = Tc
  name = G4_Tc
  specific = 4
FEATURE [App::DocumentObjectGroupPython] Ru_element001  label="Ru_element : 1"  # scripted group (container) (typed FeaturePython)
  n = 1
  ref = Ru_element
FEATURE [App::DocumentObjectGroupPython] G4_Ru  # scripted group (container) (typed FeaturePython)
  Dunit = g/cm3
  Dvalue = 12.41
  Group = -> [Ru_element001]
  conduct = 2
  density = 1
  expand = 3
  formula = Ru
  name = G4_Ru
  specific = 4
FEATURE [App::DocumentObjectGroupPython] Rh_element001  label="Rh_element : 1"  # scripted group (container) (typed FeaturePython)
  n = 1
  ref = Rh_element
FEATURE [App::DocumentObjectGroupPython] G4_Rh  # scripted group (container) (typed FeaturePython)
  Dunit = g/cm3
  Dvalue = 12.41
  Group = -> [Rh_element001]
  conduct = 2
  density = 1
  expand = 3
  formula = Rh
  name = G4_Rh
  specific = 4
FEATURE [App::DocumentObjectGroupPython] Pd_element001  label="Pd_element : 1"  # scripted group (container) (typed FeaturePython)
  n = 1
  ref = Pd_element
FEATURE [App::DocumentObjectGroupPython] G4_Pd  # scripted group (container) (typed FeaturePython)
  Dunit = g/cm3
  Dvalue = 12.02
  Group = -> [Pd_element001]
  conduct = 2
  density = 1
  expand = 3
  formula = Pd
  name = G4_Pd
  specific = 4
FEATURE [App::DocumentObjectGroupPython] Ag_element006  label="Ag_element : 004"  # scripted group (container) (typed FeaturePython)
  n = 1
  ref = Ag_element
FEATURE [App::DocumentObjectGroupPython] G4_Ag  # scripted group (container) (typed FeaturePython)
  Dunit = g/cm3
  Dvalue = 10.5
  Group = -> [Ag_element006]
  conduct = 2
  density = 1
  expand = 3
  formula = Ag
  name = G4_Ag
  specific = 4
FEATURE [App::DocumentObjectGroupPython] Cd_element003  label="Cd_element : 003"  # scripted group (container) (typed FeaturePython)
  n = 1
  ref = Cd_element
FEATURE [App::DocumentObjectGroupPython] G4_Cd  # scripted group (container) (typed FeaturePython)
  Dunit = g/cm3
  Dvalue = 8.65
  Group = -> [Cd_element003]
  conduct = 2
  density = 1
  expand = 3
  formula = Cd
  name = G4_Cd
  specific = 4
FEATURE [App::DocumentObjectGroupPython] In_element001  label="In_element : 1"  # scripted group (container) (typed FeaturePython)
  n = 1
  ref = In_element
FEATURE [App::DocumentObjectGroupPython] G4_In  # scripted group (container) (typed FeaturePython)
  Dunit = g/cm3
  Dvalue = 7.31
  Group = -> [In_element001]
  conduct = 2
  density = 1
  expand = 3
  formula = In
  name = G4_In
  specific = 4
FEATURE [App::DocumentObjectGroupPython] Sn_element001  label="Sn_element : 1"  # scripted group (container) (typed FeaturePython)
  n = 1
  ref = Sn_element
FEATURE [App::DocumentObjectGroupPython] G4_Sn  # scripted group (container) (typed FeaturePython)
  Dunit = g/cm3
  Dvalue = 7.31
  Group = -> [Sn_element001]
  conduct = 2
  density = 1
  expand = 3
  formula = Sn
  name = G4_Sn
  specific = 4
FEATURE [App::DocumentObjectGroupPython] Sb_element001  label="Sb_element : 1"  # scripted group (container) (typed FeaturePython)
  n = 1
  ref = Sb_element
FEATURE [App::DocumentObjectGroupPython] G4_Sb  # scripted group (container) (typed FeaturePython)
  Dunit = g/cm3
  Dvalue = 6.691
  Group = -> [Sb_element001]
  conduct = 2
  density = 1
  expand = 3
  formula = Sb
  name = G4_Sb
  specific = 4
FEATURE [App::DocumentObjectGroupPython] Te_element002  label="Te_element : 002"  # scripted group (container) (typed FeaturePython)
  n = 1
  ref = Te_element
FEATURE [App::DocumentObjectGroupPython] G4_Te  # scripted group (container) (typed FeaturePython)
  Dunit = g/cm3
  Dvalue = 6.24
  Group = -> [Te_element002]
  conduct = 2
  density = 1
  expand = 3
  formula = Te
  name = G4_Te
  specific = 4
FEATURE [App::DocumentObjectGroupPython] I_element010  label="I_element : 006"  # scripted group (container) (typed FeaturePython)
  n = 1
  ref = I_element
FEATURE [App::DocumentObjectGroupPython] G4_I  # scripted group (container) (typed FeaturePython)
  Dunit = g/cm3
  Dvalue = 4.93
  Group = -> [I_element010]
  conduct = 2
  density = 1
  expand = 3
  formula = I
  name = G4_I
  specific = 4
FEATURE [App::DocumentObjectGroupPython] Xe_element001  label="Xe_element : 1"  # scripted group (container) (typed FeaturePython)
  n = 1
  ref = Xe_element
FEATURE [App::DocumentObjectGroupPython] G4_Xe  # scripted group (container) (typed FeaturePython)
  Dunit = g/cm3
  Dvalue = 0.00548536
  Group = -> [Xe_element001]
  conduct = 2
  density = 1
  expand = 3
  formula = Xe
  name = G4_Xe
  specific = 4
FEATURE [App::DocumentObjectGroupPython] Cs_element003  label="Cs_element : 003"  # scripted group (container) (typed FeaturePython)
  n = 1
  ref = Cs_element
FEATURE [App::DocumentObjectGroupPython] G4_Cs  # scripted group (container) (typed FeaturePython)
  Dunit = g/cm3
  Dvalue = 1.873
  Group = -> [Cs_element003]
  conduct = 2
  density = 1
  expand = 3
  formula = Cs
  name = G4_Cs
  specific = 4
FEATURE [App::DocumentObjectGroupPython] Ba_element003  label="Ba_element : 003"  # scripted group (container) (typed FeaturePython)
  n = 1
  ref = Ba_element
FEATURE [App::DocumentObjectGroupPython] G4_Ba  # scripted group (container) (typed FeaturePython)
  Dunit = g/cm3
  Dvalue = 3.5
  Group = -> [Ba_element003]
  conduct = 2
  density = 1
  expand = 3
  formula = Ba
  name = G4_Ba
  specific = 4
FEATURE [App::DocumentObjectGroupPython] La_element003  label="La_element : 003"  # scripted group (container) (typed FeaturePython)
  n = 1
  ref = La_element
FEATURE [App::DocumentObjectGroupPython] G4_La  # scripted group (container) (typed FeaturePython)
  Dunit = g/cm3
  Dvalue = 6.154
  Group = -> [La_element003]
  conduct = 2
  density = 1
  expand = 3
  formula = La
  name = G4_La
  specific = 4
FEATURE [App::DocumentObjectGroupPython] Ce_element002  label="Ce_element : 1"  # scripted group (container) (typed FeaturePython)
  n = 1
  ref = Ce_element
FEATURE [App::DocumentObjectGroupPython] G4_Ce  # scripted group (container) (typed FeaturePython)
  Dunit = g/cm3
  Dvalue = 6.657
  Group = -> [Ce_element002]
  conduct = 2
  density = 1
  expand = 3
  formula = Ce
  name = G4_Ce
  specific = 4
FEATURE [App::DocumentObjectGroupPython] Pr_element001  label="Pr_element : 1"  # scripted group (container) (typed FeaturePython)
  n = 1
  ref = Pr_element
FEATURE [App::DocumentObjectGroupPython] G4_Pr  # scripted group (container) (typed FeaturePython)
  Dunit = g/cm3
  Dvalue = 6.71
  Group = -> [Pr_element001]
  conduct = 2
  density = 1
  expand = 3
  formula = Pr
  name = G4_Pr
  specific = 4
FEATURE [App::DocumentObjectGroupPython] Nd_element001  label="Nd_element : 1"  # scripted group (container) (typed FeaturePython)
  n = 1
  ref = Nd_element
FEATURE [App::DocumentObjectGroupPython] G4_Nd  # scripted group (container) (typed FeaturePython)
  Dunit = g/cm3
  Dvalue = 6.9
  Group = -> [Nd_element001]
  conduct = 2
  density = 1
  expand = 3
  formula = Nd
  name = G4_Nd
  specific = 4
FEATURE [App::DocumentObjectGroupPython] Pm_element001  label="Pm_element : 1"  # scripted group (container) (typed FeaturePython)
  n = 1
  ref = Pm_element
FEATURE [App::DocumentObjectGroupPython] G4_Pm  # scripted group (container) (typed FeaturePython)
  Dunit = g/cm3
  Dvalue = 7.22
  Group = -> [Pm_element001]
  conduct = 2
  density = 1
  expand = 3
  formula = Pm
  name = G4_Pm
  specific = 4
FEATURE [App::DocumentObjectGroupPython] Sm_element001  label="Sm_element : 1"  # scripted group (container) (typed FeaturePython)
  n = 1
  ref = Sm_element
FEATURE [App::DocumentObjectGroupPython] G4_Sm  # scripted group (container) (typed FeaturePython)
  Dunit = g/cm3
  Dvalue = 7.46
  Group = -> [Sm_element001]
  conduct = 2
  density = 1
  expand = 3
  formula = Sm
  name = G4_Sm
  specific = 4
FEATURE [App::DocumentObjectGroupPython] Eu_element001  label="Eu_element : 1"  # scripted group (container) (typed FeaturePython)
  n = 1
  ref = Eu_element
FEATURE [App::DocumentObjectGroupPython] G4_Eu  # scripted group (container) (typed FeaturePython)
  Dunit = g/cm3
  Dvalue = 5.243
  Group = -> [Eu_element001]
  conduct = 2
  density = 1
  expand = 3
  formula = Eu
  name = G4_Eu
  specific = 4
FEATURE [App::DocumentObjectGroupPython] Gd_element002  label="Gd_element : 1"  # scripted group (container) (typed FeaturePython)
  n = 1
  ref = Gd_element
FEATURE [App::DocumentObjectGroupPython] G4_Gd  # scripted group (container) (typed FeaturePython)
  Dunit = g/cm3
  Dvalue = 7.9004
  Group = -> [Gd_element002]
  conduct = 2
  density = 1
  expand = 3
  formula = Gd
  name = G4_Gd
  specific = 4
FEATURE [App::DocumentObjectGroupPython] Tb_element001  label="Tb_element : 1"  # scripted group (container) (typed FeaturePython)
  n = 1
  ref = Tb_element
FEATURE [App::DocumentObjectGroupPython] G4_Tb  # scripted group (container) (typed FeaturePython)
  Dunit = g/cm3
  Dvalue = 8.229
  Group = -> [Tb_element001]
  conduct = 2
  density = 1
  expand = 3
  formula = Tb
  name = G4_Tb
  specific = 4
FEATURE [App::DocumentObjectGroupPython] Dy_element001  label="Dy_element : 1"  # scripted group (container) (typed FeaturePython)
  n = 1
  ref = Dy_element
FEATURE [App::DocumentObjectGroupPython] G4_Dy  # scripted group (container) (typed FeaturePython)
  Dunit = g/cm3
  Dvalue = 8.55
  Group = -> [Dy_element001]
  conduct = 2
  density = 1
  expand = 3
  formula = Dy
  name = G4_Dy
  specific = 4
FEATURE [App::DocumentObjectGroupPython] Ho_element001  label="Ho_element : 1"  # scripted group (container) (typed FeaturePython)
  n = 1
  ref = Ho_element
FEATURE [App::DocumentObjectGroupPython] G4_Ho  # scripted group (container) (typed FeaturePython)
  Dunit = g/cm3
  Dvalue = 8.795
  Group = -> [Ho_element001]
  conduct = 2
  density = 1
  expand = 3
  formula = Ho
  name = G4_Ho
  specific = 4
FEATURE [App::DocumentObjectGroupPython] Er_element001  label="Er_element : 1"  # scripted group (container) (typed FeaturePython)
  n = 1
  ref = Er_element
FEATURE [App::DocumentObjectGroupPython] G4_Er  # scripted group (container) (typed FeaturePython)
  Dunit = g/cm3
  Dvalue = 9.066
  Group = -> [Er_element001]
  conduct = 2
  density = 1
  expand = 3
  formula = Er
  name = G4_Er
  specific = 4
FEATURE [App::DocumentObjectGroupPython] Tm_element001  label="Tm_element : 1"  # scripted group (container) (typed FeaturePython)
  n = 1
  ref = Tm_element
FEATURE [App::DocumentObjectGroupPython] G4_Tm  # scripted group (container) (typed FeaturePython)
  Dunit = g/cm3
  Dvalue = 9.321
  Group = -> [Tm_element001]
  conduct = 2
  density = 1
  expand = 3
  formula = Tm
  name = G4_Tm
  specific = 4
FEATURE [App::DocumentObjectGroupPython] Yb_element001  label="Yb_element : 1"  # scripted group (container) (typed FeaturePython)
  n = 1
  ref = Yb_element
FEATURE [App::DocumentObjectGroupPython] G4_Yb  # scripted group (container) (typed FeaturePython)
  Dunit = g/cm3
  Dvalue = 6.73
  Group = -> [Yb_element001]
  conduct = 2
  density = 1
  expand = 3
  formula = Yb
  name = G4_Yb
  specific = 4
FEATURE [App::DocumentObjectGroupPython] Lu_element001  label="Lu_element : 1"  # scripted group (container) (typed FeaturePython)
  n = 1
  ref = Lu_element
FEATURE [App::DocumentObjectGroupPython] G4_Lu  # scripted group (container) (typed FeaturePython)
  Dunit = g/cm3
  Dvalue = 9.84
  Group = -> [Lu_element001]
  conduct = 2
  density = 1
  expand = 3
  formula = Lu
  name = G4_Lu
  specific = 4
FEATURE [App::DocumentObjectGroupPython] Hf_element001  label="Hf_element : 1"  # scripted group (container) (typed FeaturePython)
  n = 1
  ref = Hf_element
FEATURE [App::DocumentObjectGroupPython] G4_Hf  # scripted group (container) (typed FeaturePython)
  Dunit = g/cm3
  Dvalue = 13.31
  Group = -> [Hf_element001]
  conduct = 2
  density = 1
  expand = 3
  formula = Hf
  name = G4_Hf
  specific = 4
FEATURE [App::DocumentObjectGroupPython] Ta_element001  label="Ta_element : 1"  # scripted group (container) (typed FeaturePython)
  n = 1
  ref = Ta_element
FEATURE [App::DocumentObjectGroupPython] G4_Ta  # scripted group (container) (typed FeaturePython)
  Dunit = g/cm3
  Dvalue = 16.654
  Group = -> [Ta_element001]
  conduct = 2
  density = 1
  expand = 3
  formula = Ta
  name = G4_Ta
  specific = 4
FEATURE [App::DocumentObjectGroupPython] W_element004  label="W_element : 004"  # scripted group (container) (typed FeaturePython)
  n = 1
  ref = W_element
FEATURE [App::DocumentObjectGroupPython] G4_W  # scripted group (container) (typed FeaturePython)
  Dunit = g/cm3
  Dvalue = 19.3
  Group = -> [W_element004]
  conduct = 2
  density = 1
  expand = 3
  formula = W
  name = G4_W
  specific = 4
FEATURE [App::DocumentObjectGroupPython] Re_element001  label="Re_element : 1"  # scripted group (container) (typed FeaturePython)
  n = 1
  ref = Re_element
FEATURE [App::DocumentObjectGroupPython] G4_Re  # scripted group (container) (typed FeaturePython)
  Dunit = g/cm3
  Dvalue = 21.02
  Group = -> [Re_element001]
  conduct = 2
  density = 1
  expand = 3
  formula = Re
  name = G4_Re
  specific = 4
FEATURE [App::DocumentObjectGroupPython] Os_element001  label="Os_element : 1"  # scripted group (container) (typed FeaturePython)
  n = 1
  ref = Os_element
FEATURE [App::DocumentObjectGroupPython] G4_Os  # scripted group (container) (typed FeaturePython)
  Dunit = g/cm3
  Dvalue = 22.57
  Group = -> [Os_element001]
  conduct = 2
  density = 1
  expand = 3
  formula = Os
  name = G4_Os
  specific = 4
FEATURE [App::DocumentObjectGroupPython] Ir_element001  label="Ir_element : 1"  # scripted group (container) (typed FeaturePython)
  n = 1
  ref = Ir_element
FEATURE [App::DocumentObjectGroupPython] G4_Ir  # scripted group (container) (typed FeaturePython)
  Dunit = g/cm3
  Dvalue = 22.42
  Group = -> [Ir_element001]
  conduct = 2
  density = 1
  expand = 3
  formula = Ir
  name = G4_Ir
  specific = 4
FEATURE [App::DocumentObjectGroupPython] Pt_element001  label="Pt_element : 1"  # scripted group (container) (typed FeaturePython)
  n = 1
  ref = Pt_element
FEATURE [App::DocumentObjectGroupPython] G4_Pt  # scripted group (container) (typed FeaturePython)
  Dunit = g/cm3
  Dvalue = 21.45
  Group = -> [Pt_element001]
  conduct = 2
  density = 1
  expand = 3
  formula = Pt
  name = G4_Pt
  specific = 4
FEATURE [App::DocumentObjectGroupPython] Au_element001  label="Au_element : 1"  # scripted group (container) (typed FeaturePython)
  n = 1
  ref = Au_element
FEATURE [App::DocumentObjectGroupPython] G4_Au  # scripted group (container) (typed FeaturePython)
  Dunit = g/cm3
  Dvalue = 19.32
  Group = -> [Au_element001]
  conduct = 2
  density = 1
  expand = 3
  formula = Au
  name = G4_Au
  specific = 4
FEATURE [App::DocumentObjectGroupPython] Hg_element002  label="Hg_element : 002"  # scripted group (container) (typed FeaturePython)
  n = 1
  ref = Hg_element
FEATURE [App::DocumentObjectGroupPython] G4_Hg  # scripted group (container) (typed FeaturePython)
  Dunit = g/cm3
  Dvalue = 13.546
  Group = -> [Hg_element002]
  conduct = 2
  density = 1
  expand = 3
  formula = Hg
  name = G4_Hg
  specific = 4
FEATURE [App::DocumentObjectGroupPython] Tl_element002  label="Tl_element : 002"  # scripted group (container) (typed FeaturePython)
  n = 1
  ref = Tl_element
FEATURE [App::DocumentObjectGroupPython] G4_Tl  # scripted group (container) (typed FeaturePython)
  Dunit = g/cm3
  Dvalue = 11.72
  Group = -> [Tl_element002]
  conduct = 2
  density = 1
  expand = 3
  formula = Tl
  name = G4_Tl
  specific = 4
FEATURE [App::DocumentObjectGroupPython] Pb_element003  label="Pb_element : 1"  # scripted group (container) (typed FeaturePython)
  n = 1
  ref = Pb_element
FEATURE [App::DocumentObjectGroupPython] G4_Pb  # scripted group (container) (typed FeaturePython)
  Dunit = g/cm3
  Dvalue = 11.35
  Group = -> [Pb_element003]
  conduct = 2
  density = 1
  expand = 3
  formula = Pb
  name = G4_Pb
  specific = 4
FEATURE [App::DocumentObjectGroupPython] Bi_element002  label="Bi_element : 1"  # scripted group (container) (typed FeaturePython)
  n = 1
  ref = Bi_element
FEATURE [App::DocumentObjectGroupPython] G4_Bi  # scripted group (container) (typed FeaturePython)
  Dunit = g/cm3
  Dvalue = 9.747
  Group = -> [Bi_element002]
  conduct = 2
  density = 1
  expand = 3
  formula = Bi
  name = G4_Bi
  specific = 4
FEATURE [App::DocumentObjectGroupPython] Po_element001  label="Po_element : 1"  # scripted group (container) (typed FeaturePython)
  n = 1
  ref = Po_element
FEATURE [App::DocumentObjectGroupPython] G4_Po  # scripted group (container) (typed FeaturePython)
  Dunit = g/cm3
  Dvalue = 9.32
  Group = -> [Po_element001]
  conduct = 2
  density = 1
  expand = 3
  formula = Po
  name = G4_Po
  specific = 4
FEATURE [App::DocumentObjectGroupPython] At_element001  label="At_element : 1"  # scripted group (container) (typed FeaturePython)
  n = 1
  ref = At_element
FEATURE [App::DocumentObjectGroupPython] G4_At  # scripted group (container) (typed FeaturePython)
  Dunit = g/cm3
  Dvalue = 9.32
  Group = -> [At_element001]
  conduct = 2
  density = 1
  expand = 3
  formula = At
  name = G4_At
  specific = 4
FEATURE [App::DocumentObjectGroupPython] Rn_element001  label="Rn_element : 1"  # scripted group (container) (typed FeaturePython)
  n = 1
  ref = Rn_element
FEATURE [App::DocumentObjectGroupPython] G4_Rn  # scripted group (container) (typed FeaturePython)
  Dunit = g/cm3
  Dvalue = 0.00900662
  Group = -> [Rn_element001]
  conduct = 2
  density = 1
  expand = 3
  formula = Rn
  name = G4_Rn
  specific = 4
FEATURE [App::DocumentObjectGroupPython] Fr_element001  label="Fr_element : 1"  # scripted group (container) (typed FeaturePython)
  n = 1
  ref = Fr_element
FEATURE [App::DocumentObjectGroupPython] G4_Fr  # scripted group (container) (typed FeaturePython)
  Dunit = g/cm3
  Dvalue = 1
  Group = -> [Fr_element001]
  conduct = 2
  density = 1
  expand = 3
  formula = Fr
  name = G4_Fr
  specific = 4
FEATURE [App::DocumentObjectGroupPython] Ra_element001  label="Ra_element : 1"  # scripted group (container) (typed FeaturePython)
  n = 1
  ref = Ra_element
FEATURE [App::DocumentObjectGroupPython] G4_Ra  # scripted group (container) (typed FeaturePython)
  Dunit = g/cm3
  Dvalue = 5
  Group = -> [Ra_element001]
  conduct = 2
  density = 1
  expand = 3
  formula = Ra
  name = G4_Ra
  specific = 4
FEATURE [App::DocumentObjectGroupPython] Ac_element001  label="Ac_element : 1"  # scripted group (container) (typed FeaturePython)
  n = 1
  ref = Ac_element
FEATURE [App::DocumentObjectGroupPython] G4_Ac  # scripted group (container) (typed FeaturePython)
  Dunit = g/cm3
  Dvalue = 10.07
  Group = -> [Ac_element001]
  conduct = 2
  density = 1
  expand = 3
  formula = Ac
  name = G4_Ac
  specific = 4
FEATURE [App::DocumentObjectGroupPython] Th_element001  label="Th_element : 1"  # scripted group (container) (typed FeaturePython)
  n = 1
  ref = Th_element
FEATURE [App::DocumentObjectGroupPython] G4_Th  # scripted group (container) (typed FeaturePython)
  Dunit = g/cm3
  Dvalue = 11.72
  Group = -> [Th_element001]
  conduct = 2
  density = 1
  expand = 3
  formula = Th
  name = G4_Th
  specific = 4
FEATURE [App::DocumentObjectGroupPython] Pa_element001  label="Pa_element : 1"  # scripted group (container) (typed FeaturePython)
  n = 1
  ref = Pa_element
FEATURE [App::DocumentObjectGroupPython] G4_Pa  # scripted group (container) (typed FeaturePython)
  Dunit = g/cm3
  Dvalue = 15.37
  Group = -> [Pa_element001]
  conduct = 2
  density = 1
  expand = 3
  formula = Pa
  name = G4_Pa
  specific = 4
FEATURE [App::DocumentObjectGroupPython] U_element004  label="U_element : 004"  # scripted group (container) (typed FeaturePython)
  n = 1
  ref = U_element
FEATURE [App::DocumentObjectGroupPython] G4_U  # scripted group (container) (typed FeaturePython)
  Dunit = g/cm3
  Dvalue = 18.95
  Group = -> [U_element004]
  conduct = 2
  density = 1
  expand = 3
  formula = U
  name = G4_U
  specific = 4
FEATURE [App::DocumentObjectGroupPython] Np_element001  label="Np_element : 1"  # scripted group (container) (typed FeaturePython)
  n = 1
  ref = Np_element
FEATURE [App::DocumentObjectGroupPython] G4_Np  # scripted group (container) (typed FeaturePython)
  Dunit = g/cm3
  Dvalue = 20.25
  Group = -> [Np_element001]
  conduct = 2
  density = 1
  expand = 3
  formula = Np
  name = G4_Np
  specific = 4
FEATURE [App::DocumentObjectGroupPython] Pu_element002  label="Pu_element : 002"  # scripted group (container) (typed FeaturePython)
  n = 1
  ref = Pu_element
FEATURE [App::DocumentObjectGroupPython] G4_Pu  # scripted group (container) (typed FeaturePython)
  Dunit = g/cm3
  Dvalue = 19.84
  Group = -> [Pu_element002]
  conduct = 2
  density = 1
  expand = 3
  formula = Pu
  name = G4_Pu
  specific = 4
FEATURE [App::DocumentObjectGroupPython] Am_element001  label="Am_element : 1"  # scripted group (container) (typed FeaturePython)
  n = 1
  ref = Am_element
FEATURE [App::DocumentObjectGroupPython] G4_Am  # scripted group (container) (typed FeaturePython)
  Dunit = g/cm3
  Dvalue = 13.67
  Group = -> [Am_element001]
  conduct = 2
  density = 1
  expand = 3
  formula = Am
  name = G4_Am
  specific = 4
FEATURE [App::DocumentObjectGroupPython] Cm_element001  label="Cm_element : 1"  # scripted group (container) (typed FeaturePython)
  n = 1
  ref = Cm_element
FEATURE [App::DocumentObjectGroupPython] G4_Cm  # scripted group (container) (typed FeaturePython)
  Dunit = g/cm3
  Dvalue = 13.51
  Group = -> [Cm_element001]
  conduct = 2
  density = 1
  expand = 3
  formula = Cm
  name = G4_Cm
  specific = 4
FEATURE [App::DocumentObjectGroupPython] Bk_element001  label="Bk_element : 1"  # scripted group (container) (typed FeaturePython)
  n = 1
  ref = Bk_element
FEATURE [App::DocumentObjectGroupPython] G4_Bk  # scripted group (container) (typed FeaturePython)
  Dunit = g/cm3
  Dvalue = 14
  Group = -> [Bk_element001]
  conduct = 2
  density = 1
  expand = 3
  formula = Bk
  name = G4_Bk
  specific = 4
FEATURE [App::DocumentObjectGroupPython] Cf_element001  label="Cf_element : 1"  # scripted group (container) (typed FeaturePython)
  n = 1
  ref = Cf_element
FEATURE [App::DocumentObjectGroupPython] G4_Cf  # scripted group (container) (typed FeaturePython)
  Dunit = g/cm3
  Dvalue = 10
  Group = -> [Cf_element001]
  conduct = 2
  density = 1
  expand = 3
  formula = Cf
  name = G4_Cf
  specific = 4
FEATURE [App::DocumentObjectGroupPython] Element  # scripted group (container) (typed FeaturePython)
  Group = -> [G4_H,G4_He,G4_Li,G4_Be,G4_B,G4_C,G4_N,G4_O,G4_F,G4_Ne,G4_Na,G4_Mg,G4_Al,G4_Si,G4_P,G4_S,G4_Cl,G4_Ar,G4_K,G4_Ca,G4_Sc,G4_Ti,G4_V,G4_Cr,G4_Mn,G4_Fe,G4_Co,G4_Ni,G4_Cu,G4_Zn,G4_Ga,G4_Ge,G4_As,G4_Se,G4_Br,G4_Kr,G4_Rb,G4_Sr,G4_Y,G4_Zr,G4_Nb,G4_Mo,G4_Tc,G4_Ru,G4_Rh,G4_Pd,G4_Ag,G4_Cd,G4_In,G4_Sn,G4_Sb,G4_Te,G4_I,G4_Xe,G4_Cs,G4_Ba,G4_La,G4_Ce,G4_Pr,G4_Nd,G4_Pm,G4_Sm,G4_Eu,G4_Gd,G4_Tb,G4_Dy,G4_Ho,G4_Er,+30 more]
FEATURE [App::DocumentObjectGroupPython] H_element114  label="H_element : 063"  # scripted group (container) (typed FeaturePython)
  n = 2
  ref = H_element
FEATURE [App::DocumentObjectGroupPython] G4_lH2  # scripted group (container) (typed FeaturePython)
  Dunit = g/cm3
  Dvalue = 0.0708
  Group = -> [H_element114]
  conduct = 2
  density = 1
  expand = 3
  formula = G4_lH2
  name = G4_lH2
  specific = 4
FEATURE [App::DocumentObjectGroupPython] N_element049  label="N_element : 022"  # scripted group (container) (typed FeaturePython)
  n = 2
  ref = N_element
FEATURE [App::DocumentObjectGroupPython] G4_lN2  # scripted group (container) (typed FeaturePython)
  Dunit = g/cm3
  Dvalue = 0.807
  Group = -> [N_element049]
  conduct = 2
  density = 1
  expand = 3
  formula = G4_lN2
  name = G4_lN2
  specific = 4
FEATURE [App::DocumentObjectGroupPython] O_element106  label="O_element : 060"  # scripted group (container) (typed FeaturePython)
  n = 2
  ref = O_element
FEATURE [App::DocumentObjectGroupPython] G4_lO2  # scripted group (container) (typed FeaturePython)
  Dunit = g/cm3
  Dvalue = 1.141
  Group = -> [O_element106]
  conduct = 2
  density = 1
  expand = 3
  formula = G4_lO2
  name = G4_lO2
  specific = 4
FEATURE [App::DocumentObjectGroupPython] Ar  label="Ar : 1"  # scripted group (container) (typed FeaturePython)
  n = 1
  ref = Ar
FEATURE [App::DocumentObjectGroupPython] G4_lAr  # scripted group (container) (typed FeaturePython)
  Dunit = g/cm3
  Dvalue = 1.396
  Group = -> [Ar]
  conduct = 2
  density = 1
  expand = 3
  formula = G4_lAr
  name = G4_lAr
  specific = 4
FEATURE [App::DocumentObjectGroupPython] Br  label="Br : 1"  # scripted group (container) (typed FeaturePython)
  n = 1
  ref = Br
FEATURE [App::DocumentObjectGroupPython] G4_lBr  # scripted group (container) (typed FeaturePython)
  Dunit = g/cm3
  Dvalue = 3.1028
  Group = -> [Br]
  conduct = 2
  density = 1
  expand = 3
  formula = G4_lBr
  name = G4_lBr
  specific = 4
FEATURE [App::DocumentObjectGroupPython] Kr  label="Kr : 1"  # scripted group (container) (typed FeaturePython)
  n = 1
  ref = Kr
FEATURE [App::DocumentObjectGroupPython] G4_lKr  # scripted group (container) (typed FeaturePython)
  Dunit = g/cm3
  Dvalue = 2.418
  Group = -> [Kr]
  conduct = 2
  density = 1
  expand = 3
  formula = G4_lKr
  name = G4_lKr
  specific = 4
FEATURE [App::DocumentObjectGroupPython] Xe  label="Xe : 1"  # scripted group (container) (typed FeaturePython)
  n = 1
  ref = Xe
FEATURE [App::DocumentObjectGroupPython] G4_lXe  # scripted group (container) (typed FeaturePython)
  Dunit = g/cm3
  Dvalue = 2.953
  Group = -> [Xe]
  conduct = 2
  density = 1
  expand = 3
  formula = G4_lXe
  name = G4_lXe
  specific = 4
FEATURE [App::DocumentObjectGroupPython] O_element107  label="O_element : 061"  # scripted group (container) (typed FeaturePython)
  n = 4
  ref = O_element
FEATURE [App::DocumentObjectGroupPython] Pb_element004  label="Pb_element : 002"  # scripted group (container) (typed FeaturePython)
  n = 1
  ref = Pb_element
FEATURE [App::DocumentObjectGroupPython] W_element005  label="W_element : 005"  # scripted group (container) (typed FeaturePython)
  n = 1
  ref = W_element
FEATURE [App::DocumentObjectGroupPython] G4_PbWO4  # scripted group (container) (typed FeaturePython)
  Dunit = g/cm3
  Dvalue = 8.28
  Group = -> [O_element107,Pb_element004,W_element005]
  conduct = 2
  density = 1
  expand = 3
  formula = G4_PbWO4
  name = G4_PbWO4
  specific = 4
FEATURE [App::DocumentObjectGroupPython] alactic  label="alactic : 1"  # scripted group (container) (typed FeaturePython)
  n = 1
  ref = alactic
FEATURE [App::DocumentObjectGroupPython] G4_Galactic  # scripted group (container) (typed FeaturePython)
  Dunit = g/cm3
  Dvalue = 0
  Group = -> [alactic]
  conduct = 2
  density = 1
  expand = 3
  formula = G4_Galactic
  name = G4_Galactic
  specific = 4
FEATURE [App::DocumentObjectGroupPython] RAPHITE_POROUS  label="RAPHITE_POROUS : 1"  # scripted group (container) (typed FeaturePython)
  n = 1
  ref = RAPHITE_POROUS
FEATURE [App::DocumentObjectGroupPython] G4_GRAPHITE_POROUS  # scripted group (container) (typed FeaturePython)
  Dunit = g/cm3
  Dvalue = 1.7
  Group = -> [RAPHITE_POROUS]
  conduct = 2
  density = 1
  expand = 3
  formula = G4_GRAPHITE_POROUS
  name = G4_GRAPHITE_POROUS
  specific = 4
FEATURE [App::DocumentObjectGroupPython] H_element115  label="H_element : 0.150"  # scripted group (container) (typed FeaturePython)
  n = 0.080538
FEATURE [App::DocumentObjectGroupPython] C_element125  label="C_element : 0.600"  # scripted group (container) (typed FeaturePython)
  n = 0.599848
FEATURE [App::DocumentObjectGroupPython] O_element108  label="O_element : 0.320"  # scripted group (container) (typed FeaturePython)
  n = 0.319614
FEATURE [App::DocumentObjectGroupPython] G4_LUCITE  # scripted group (container) (typed FeaturePython)
  Dunit = g/cm3
  Dvalue = 1.19
  Group = -> [H_element115,C_element125,O_element108]
  conduct = 2
  density = 1
  expand = 3
  formula = G4_LUCITE
  name = G4_LUCITE
  specific = 4
FEATURE [App::DocumentObjectGroupPython] Cu_element002  label="Cu_element : 62"  # scripted group (container) (typed FeaturePython)
  n = 62
  ref = Cu_element
FEATURE [App::DocumentObjectGroupPython] Zn_element002  label="Zn_element : 35"  # scripted group (container) (typed FeaturePython)
  n = 35
  ref = Zn_element
FEATURE [App::DocumentObjectGroupPython] Pb_element005  label="Pb_element : 3"  # scripted group (container) (typed FeaturePython)
  n = 3
  ref = Pb_element
FEATURE [App::DocumentObjectGroupPython] G4_BRASS  # scripted group (container) (typed FeaturePython)
  Dunit = g/cm3
  Dvalue = 8.52
  Group = -> [Cu_element002,Zn_element002,Pb_element005]
  conduct = 2
  density = 1
  expand = 3
  formula = G4_BRASS
  name = G4_BRASS
  specific = 4
FEATURE [App::DocumentObjectGroupPython] Cu_element003  label="Cu_element : 89"  # scripted group (container) (typed FeaturePython)
  n = 89
  ref = Cu_element
FEATURE [App::DocumentObjectGroupPython] Zn_element003  label="Zn_element : 9"  # scripted group (container) (typed FeaturePython)
  n = 9
  ref = Zn_element
FEATURE [App::DocumentObjectGroupPython] Pb_element006  label="Pb_element : 2"  # scripted group (container) (typed FeaturePython)
  n = 2
  ref = Pb_element
FEATURE [App::DocumentObjectGroupPython] G4_BRONZE  # scripted group (container) (typed FeaturePython)
  Dunit = g/cm3
  Dvalue = 8.82
  Group = -> [Cu_element003,Zn_element003,Pb_element006]
  conduct = 2
  density = 1
  expand = 3
  formula = G4_BRONZE
  name = G4_BRONZE
  specific = 4
FEATURE [App::DocumentObjectGroupPython] Fe_element008  label="Fe_element : 74"  # scripted group (container) (typed FeaturePython)
  n = 74
  ref = Fe_element
FEATURE [App::DocumentObjectGroupPython] Cr_element002  label="Cr_element : 18"  # scripted group (container) (typed FeaturePython)
  n = 18
  ref = Cr_element
FEATURE [App::DocumentObjectGroupPython] Ni_element002  label="Ni_element : 8"  # scripted group (container) (typed FeaturePython)
  n = 8
  ref = Ni_element
FEATURE [App::DocumentObjectGroupPython] G4_STAINLESS_STEEL  label="G4_STAINLESS-STEEL"  # scripted group (container) (typed FeaturePython)
  Dunit = g/cm3
  Dvalue = 8
  Group = -> [Fe_element008,Cr_element002,Ni_element002]
  conduct = 2
  density = 1
  expand = 3
  formula = G4_STAINLESS-STEEL
  name = G4_STAINLESS-STEEL
  specific = 4
FEATURE [App::DocumentObjectGroupPython] H_element116  label="H_element : 064"  # scripted group (container) (typed FeaturePython)
  n = 18
  ref = H_element
FEATURE [App::DocumentObjectGroupPython] C_element126  label="C_element : 071"  # scripted group (container) (typed FeaturePython)
  n = 12
  ref = C_element
FEATURE [App::DocumentObjectGroupPython] O_element109  label="O_element : 062"  # scripted group (container) (typed FeaturePython)
  n = 7
  ref = O_element
FEATURE [App::DocumentObjectGroupPython] G4_CR39  # scripted group (container) (typed FeaturePython)
  Dunit = g/cm3
  Dvalue = 1.32
  Group = -> [H_element116,C_element126,O_element109]
  conduct = 2
  density = 1
  expand = 3
  formula = G4_CR39
  name = G4_CR39
  specific = 4
FEATURE [App::DocumentObjectGroupPython] H_element117  label="H_element : 38"  # scripted group (container) (typed FeaturePython)
  n = 38
  ref = H_element
FEATURE [App::DocumentObjectGroupPython] C_element127  label="C_element : 072"  # scripted group (container) (typed FeaturePython)
  n = 18
  ref = C_element
FEATURE [App::DocumentObjectGroupPython] O_element110  label="O_element : 063"  # scripted group (container) (typed FeaturePython)
  n = 1
  ref = O_element
FEATURE [App::DocumentObjectGroupPython] G4_OCTADECANOL  # scripted group (container) (typed FeaturePython)
  Dunit = g/cm3
  Dvalue = 0.812
  Group = -> [H_element117,C_element127,O_element110]
  conduct = 2
  density = 1
  expand = 3
  formula = G4_OCTADECANOL
  name = G4_OCTADECANOL
  specific = 4
FEATURE [App::DocumentObjectGroupPython] HEP  # scripted group (container) (typed FeaturePython)
  Group = -> [G4_lH2,G4_lN2,G4_lO2,G4_lAr,G4_lBr,G4_lKr,G4_lXe,G4_PbWO4,G4_Galactic,G4_GRAPHITE_POROUS,G4_LUCITE,G4_BRASS,G4_BRONZE,G4_STAINLESS_STEEL,G4_CR39,G4_OCTADECANOL]
FEATURE [App::DocumentObjectGroupPython] C_element128  label="C_element : 073"  # scripted group (container) (typed FeaturePython)
  n = 14
  ref = C_element
FEATURE [App::DocumentObjectGroupPython] H_element118  label="H_element : 065"  # scripted group (container) (typed FeaturePython)
  n = 10
  ref = H_element
FEATURE [App::DocumentObjectGroupPython] O_element111  label="O_element : 064"  # scripted group (container) (typed FeaturePython)
  n = 2
  ref = O_element
FEATURE [App::DocumentObjectGroupPython] N_element050  label="N_element : 023"  # scripted group (container) (typed FeaturePython)
  n = 2
  ref = N_element
FEATURE [App::DocumentObjectGroupPython] G4_KEVLAR  # scripted group (container) (typed FeaturePython)
  Dunit = g/cm3
  Dvalue = 1.44
  Group = -> [C_element128,H_element118,O_element111,N_element050]
  conduct = 2
  density = 1
  expand = 3
  formula = G4_KEVLAR
  name = G4_KEVLAR
  specific = 4
FEATURE [App::DocumentObjectGroupPython] C_element129  label="C_element : 074"  # scripted group (container) (typed FeaturePython)
  n = 10
  ref = C_element
FEATURE [App::DocumentObjectGroupPython] H_element119  label="H_element : 066"  # scripted group (container) (typed FeaturePython)
  n = 8
  ref = H_element
FEATURE [App::DocumentObjectGroupPython] O_element112  label="O_element : 065"  # scripted group (container) (typed FeaturePython)
  n = 4
  ref = O_element
FEATURE [App::DocumentObjectGroupPython] G4_DACRON  # scripted group (container) (typed FeaturePython)
  Dunit = g/cm3
  Dvalue = 1.4
  Group = -> [C_element129,H_element119,O_element112]
  conduct = 2
  density = 1
  expand = 3
  formula = G4_DACRON
  name = G4_DACRON
  specific = 4
FEATURE [App::DocumentObjectGroupPython] C_element130  label="C_element : 075"  # scripted group (container) (typed FeaturePython)
  n = 4
  ref = C_element
FEATURE [App::DocumentObjectGroupPython] H_element120  label="H_element : 067"  # scripted group (container) (typed FeaturePython)
  n = 5
  ref = H_element
FEATURE [App::DocumentObjectGroupPython] Cl_element030  label="Cl_element : 016"  # scripted group (container) (typed FeaturePython)
  n = 1
  ref = Cl_element
FEATURE [App::DocumentObjectGroupPython] G4_NEOPRENE  # scripted group (container) (typed FeaturePython)
  Dunit = g/cm3
  Dvalue = 1.23
  Group = -> [C_element130,H_element120,Cl_element030]
  conduct = 2
  density = 1
  expand = 3
  formula = G4_NEOPRENE
  name = G4_NEOPRENE
  specific = 4
FEATURE [App::DocumentObjectGroupPython] Space  # scripted group (container) (typed FeaturePython)
  Group = -> [G4_KEVLAR,G4_DACRON,G4_NEOPRENE]
FEATURE [App::DocumentObjectGroupPython] H_element121  label="H_element : 068"  # scripted group (container) (typed FeaturePython)
  n = 5
  ref = H_element
FEATURE [App::DocumentObjectGroupPython] C_element131  label="C_element : 076"  # scripted group (container) (typed FeaturePython)
  n = 4
  ref = C_element
FEATURE [App::DocumentObjectGroupPython] N_element051  label="N_element : 3"  # scripted group (container) (typed FeaturePython)
  n = 3
  ref = N_element
FEATURE [App::DocumentObjectGroupPython] O_element113  label="O_element : 066"  # scripted group (container) (typed FeaturePython)
  n = 1
  ref = O_element
FEATURE [App::DocumentObjectGroupPython] G4_CYTOSINE  # scripted group (container) (typed FeaturePython)
  Dunit = g/cm3
  Dvalue = 1.55
  Group = -> [H_element121,C_element131,N_element051,O_element113]
  conduct = 2
  density = 1
  expand = 3
  formula = G4_CYTOSINE
  name = G4_CYTOSINE
  specific = 4
FEATURE [App::DocumentObjectGroupPython] H_element122  label="H_element : 069"  # scripted group (container) (typed FeaturePython)
  n = 6
  ref = H_element
FEATURE [App::DocumentObjectGroupPython] C_element132  label="C_element : 077"  # scripted group (container) (typed FeaturePython)
  n = 5
  ref = C_element
FEATURE [App::DocumentObjectGroupPython] N_element052  label="N_element : 024"  # scripted group (container) (typed FeaturePython)
  n = 2
  ref = N_element
FEATURE [App::DocumentObjectGroupPython] O_element114  label="O_element : 067"  # scripted group (container) (typed FeaturePython)
  n = 2
  ref = O_element
FEATURE [App::DocumentObjectGroupPython] G4_THYMINE  # scripted group (container) (typed FeaturePython)
  Dunit = g/cm3
  Dvalue = 1.23
  Group = -> [H_element122,C_element132,N_element052,O_element114]
  conduct = 2
  density = 1
  expand = 3
  formula = G4_THYMINE
  name = G4_THYMINE
  specific = 4
FEATURE [App::DocumentObjectGroupPython] H_element123  label="H_element : 070"  # scripted group (container) (typed FeaturePython)
  n = 4
  ref = H_element
FEATURE [App::DocumentObjectGroupPython] C_element133  label="C_element : 078"  # scripted group (container) (typed FeaturePython)
  n = 4
  ref = C_element
FEATURE [App::DocumentObjectGroupPython] N_element053  label="N_element : 025"  # scripted group (container) (typed FeaturePython)
  n = 2
  ref = N_element
FEATURE [App::DocumentObjectGroupPython] O_element115  label="O_element : 068"  # scripted group (container) (typed FeaturePython)
  n = 2
  ref = O_element
FEATURE [App::DocumentObjectGroupPython] G4_URACIL  # scripted group (container) (typed FeaturePython)
  Dunit = g/cm3
  Dvalue = 1.32
  Group = -> [H_element123,C_element133,N_element053,O_element115]
  conduct = 2
  density = 1
  expand = 3
  formula = G4_URACIL
  name = G4_URACIL
  specific = 4
FEATURE [App::DocumentObjectGroupPython] H_element124  label="H_element : 071"  # scripted group (container) (typed FeaturePython)
  n = 4
  ref = H_element
FEATURE [App::DocumentObjectGroupPython] C_element134  label="C_element : 079"  # scripted group (container) (typed FeaturePython)
  n = 5
  ref = C_element
FEATURE [App::DocumentObjectGroupPython] N_element054  label="N_element : 026"  # scripted group (container) (typed FeaturePython)
  n = 5
  ref = N_element
FEATURE [App::DocumentObjectGroupPython] G4_DNA_ADENINE  # scripted group (container) (typed FeaturePython)
  Dunit = g/cm3
  Dvalue = 1
  Group = -> [H_element124,C_element134,N_element054]
  conduct = 2
  density = 1
  expand = 3
  formula = G4_DNA_ADENINE
  name = G4_DNA_ADENINE
  specific = 4
FEATURE [App::DocumentObjectGroupPython] H_element125  label="H_element : 072"  # scripted group (container) (typed FeaturePython)
  n = 4
  ref = H_element
FEATURE [App::DocumentObjectGroupPython] C_element135  label="C_element : 080"  # scripted group (container) (typed FeaturePython)
  n = 5
  ref = C_element
FEATURE [App::DocumentObjectGroupPython] N_element055  label="N_element : 027"  # scripted group (container) (typed FeaturePython)
  n = 5
  ref = N_element
FEATURE [App::DocumentObjectGroupPython] O_element116  label="O_element : 069"  # scripted group (container) (typed FeaturePython)
  n = 1
  ref = O_element
FEATURE [App::DocumentObjectGroupPython] G4_DNA_GUANINE  # scripted group (container) (typed FeaturePython)
  Dunit = g/cm3
  Dvalue = 1
  Group = -> [H_element125,C_element135,N_element055,O_element116]
  conduct = 2
  density = 1
  expand = 3
  formula = G4_DNA_GUANINE
  name = G4_DNA_GUANINE
  specific = 4
FEATURE [App::DocumentObjectGroupPython] H_element126  label="H_element : 073"  # scripted group (container) (typed FeaturePython)
  n = 4
  ref = H_element
FEATURE [App::DocumentObjectGroupPython] C_element136  label="C_element : 081"  # scripted group (container) (typed FeaturePython)
  n = 4
  ref = C_element
FEATURE [App::DocumentObjectGroupPython] N_element056  label="N_element : 028"  # scripted group (container) (typed FeaturePython)
  n = 3
  ref = N_element
FEATURE [App::DocumentObjectGroupPython] O_element117  label="O_element : 070"  # scripted group (container) (typed FeaturePython)
  n = 1
  ref = O_element
FEATURE [App::DocumentObjectGroupPython] G4_DNA_CYTOSINE  # scripted group (container) (typed FeaturePython)
  Dunit = g/cm3
  Dvalue = 1
  Group = -> [H_element126,C_element136,N_element056,O_element117]
  conduct = 2
  density = 1
  expand = 3
  formula = G4_DNA_CYTOSINE
  name = G4_DNA_CYTOSINE
  specific = 4
FEATURE [App::DocumentObjectGroupPython] H_element127  label="H_element : 074"  # scripted group (container) (typed FeaturePython)
  n = 5
  ref = H_element
FEATURE [App::DocumentObjectGroupPython] C_element137  label="C_element : 082"  # scripted group (container) (typed FeaturePython)
  n = 5
  ref = C_element
FEATURE [App::DocumentObjectGroupPython] N_element057  label="N_element : 029"  # scripted group (container) (typed FeaturePython)
  n = 2
  ref = N_element
FEATURE [App::DocumentObjectGroupPython] O_element118  label="O_element : 071"  # scripted group (container) (typed FeaturePython)
  n = 2
  ref = O_element
FEATURE [App::DocumentObjectGroupPython] G4_DNA_THYMINE  # scripted group (container) (typed FeaturePython)
  Dunit = g/cm3
  Dvalue = 1
  Group = -> [H_element127,C_element137,N_element057,O_element118]
  conduct = 2
  density = 1
  expand = 3
  formula = G4_DNA_THYMINE
  name = G4_DNA_THYMINE
  specific = 4
FEATURE [App::DocumentObjectGroupPython] H_element128  label="H_element : 075"  # scripted group (container) (typed FeaturePython)
  n = 3
  ref = H_element
FEATURE [App::DocumentObjectGroupPython] C_element138  label="C_element : 083"  # scripted group (container) (typed FeaturePython)
  n = 4
  ref = C_element
FEATURE [App::DocumentObjectGroupPython] N_element058  label="N_element : 030"  # scripted group (container) (typed FeaturePython)
  n = 2
  ref = N_element
FEATURE [App::DocumentObjectGroupPython] O_element119  label="O_element : 072"  # scripted group (container) (typed FeaturePython)
  n = 2
  ref = O_element
FEATURE [App::DocumentObjectGroupPython] G4_DNA_URACIL  # scripted group (container) (typed FeaturePython)
  Dunit = g/cm3
  Dvalue = 1
  Group = -> [H_element128,C_element138,N_element058,O_element119]
  conduct = 2
  density = 1
  expand = 3
  formula = G4_DNA_URACIL
  name = G4_DNA_URACIL
  specific = 4
FEATURE [App::DocumentObjectGroupPython] H_element129  label="H_element : 076"  # scripted group (container) (typed FeaturePython)
  n = 10
  ref = H_element
FEATURE [App::DocumentObjectGroupPython] C_element139  label="C_element : 084"  # scripted group (container) (typed FeaturePython)
  n = 10
  ref = C_element
FEATURE [App::DocumentObjectGroupPython] N_element059  label="N_element : 031"  # scripted group (container) (typed FeaturePython)
  n = 5
  ref = N_element
FEATURE [App::DocumentObjectGroupPython] O_element120  label="O_element : 073"  # scripted group (container) (typed FeaturePython)
  n = 4
  ref = O_element
FEATURE [App::DocumentObjectGroupPython] G4_DNA_ADENOSINE  # scripted group (container) (typed FeaturePython)
  Dunit = g/cm3
  Dvalue = 1
  Group = -> [H_element129,C_element139,N_element059,O_element120]
  conduct = 2
  density = 1
  expand = 3
  formula = G4_DNA_ADENOSINE
  name = G4_DNA_ADENOSINE
  specific = 4
FEATURE [App::DocumentObjectGroupPython] H_element130  label="H_element : 077"  # scripted group (container) (typed FeaturePython)
  n = 10
  ref = H_element
FEATURE [App::DocumentObjectGroupPython] C_element140  label="C_element : 085"  # scripted group (container) (typed FeaturePython)
  n = 10
  ref = C_element
FEATURE [App::DocumentObjectGroupPython] N_element060  label="N_element : 032"  # scripted group (container) (typed FeaturePython)
  n = 5
  ref = N_element
FEATURE [App::DocumentObjectGroupPython] O_element121  label="O_element : 074"  # scripted group (container) (typed FeaturePython)
  n = 5
  ref = O_element
FEATURE [App::DocumentObjectGroupPython] G4_DNA_GUANOSINE  # scripted group (container) (typed FeaturePython)
  Dunit = g/cm3
  Dvalue = 1
  Group = -> [H_element130,C_element140,N_element060,O_element121]
  conduct = 2
  density = 1
  expand = 3
  formula = G4_DNA_GUANOSINE
  name = G4_DNA_GUANOSINE
  specific = 4
FEATURE [App::DocumentObjectGroupPython] H_element131  label="H_element : 078"  # scripted group (container) (typed FeaturePython)
  n = 10
  ref = H_element
FEATURE [App::DocumentObjectGroupPython] C_element141  label="C_element : 086"  # scripted group (container) (typed FeaturePython)
  n = 9
  ref = C_element
FEATURE [App::DocumentObjectGroupPython] N_element061  label="N_element : 033"  # scripted group (container) (typed FeaturePython)
  n = 3
  ref = N_element
FEATURE [App::DocumentObjectGroupPython] O_element122  label="O_element : 075"  # scripted group (container) (typed FeaturePython)
  n = 5
  ref = O_element
FEATURE [App::DocumentObjectGroupPython] G4_DNA_CYTIDINE  # scripted group (container) (typed FeaturePython)
  Dunit = g/cm3
  Dvalue = 1
  Group = -> [H_element131,C_element141,N_element061,O_element122]
  conduct = 2
  density = 1
  expand = 3
  formula = G4_DNA_CYTIDINE
  name = G4_DNA_CYTIDINE
  specific = 4
FEATURE [App::DocumentObjectGroupPython] H_element132  label="H_element : 079"  # scripted group (container) (typed FeaturePython)
  n = 9
  ref = H_element
FEATURE [App::DocumentObjectGroupPython] C_element142  label="C_element : 087"  # scripted group (container) (typed FeaturePython)
  n = 9
  ref = C_element
FEATURE [App::DocumentObjectGroupPython] N_element062  label="N_element : 034"  # scripted group (container) (typed FeaturePython)
  n = 2
  ref = N_element
FEATURE [App::DocumentObjectGroupPython] O_element123  label="O_element : 076"  # scripted group (container) (typed FeaturePython)
  n = 6
  ref = O_element
FEATURE [App::DocumentObjectGroupPython] G4_DNA_URIDINE  # scripted group (container) (typed FeaturePython)
  Dunit = g/cm3
  Dvalue = 1
  Group = -> [H_element132,C_element142,N_element062,O_element123]
  conduct = 2
  density = 1
  expand = 3
  formula = G4_DNA_URIDINE
  name = G4_DNA_URIDINE
  specific = 4
FEATURE [App::DocumentObjectGroupPython] H_element133  label="H_element : 080"  # scripted group (container) (typed FeaturePython)
  n = 11
  ref = H_element
FEATURE [App::DocumentObjectGroupPython] C_element143  label="C_element : 088"  # scripted group (container) (typed FeaturePython)
  n = 10
  ref = C_element
FEATURE [App::DocumentObjectGroupPython] N_element063  label="N_element : 035"  # scripted group (container) (typed FeaturePython)
  n = 2
  ref = N_element
FEATURE [App::DocumentObjectGroupPython] O_element124  label="O_element : 077"  # scripted group (container) (typed FeaturePython)
  n = 6
  ref = O_element
FEATURE [App::DocumentObjectGroupPython] G4_DNA_METHYLURIDINE  # scripted group (container) (typed FeaturePython)
  Dunit = g/cm3
  Dvalue = 1
  Group = -> [H_element133,C_element143,N_element063,O_element124]
  conduct = 2
  density = 1
  expand = 3
  formula = G4_DNA_METHYLURIDINE
  name = G4_DNA_METHYLURIDINE
  specific = 4
FEATURE [App::DocumentObjectGroupPython] P_element014  label="P_element : 003"  # scripted group (container) (typed FeaturePython)
  n = 1
  ref = P_element
FEATURE [App::DocumentObjectGroupPython] O_element125  label="O_element : 078"  # scripted group (container) (typed FeaturePython)
  n = 3
  ref = O_element
FEATURE [App::DocumentObjectGroupPython] G4_DNA_MONOPHOSPHATE  # scripted group (container) (typed FeaturePython)
  Dunit = g/cm3
  Dvalue = 1
  Group = -> [P_element014,O_element125]
  conduct = 2
  density = 1
  expand = 3
  formula = G4_DNA_MONOPHOSPHATE
  name = G4_DNA_MONOPHOSPHATE
  specific = 4
FEATURE [App::DocumentObjectGroupPython] H_element134  label="H_element : 081"  # scripted group (container) (typed FeaturePython)
  n = 10
  ref = H_element
FEATURE [App::DocumentObjectGroupPython] C_element144  label="C_element : 089"  # scripted group (container) (typed FeaturePython)
  n = 10
  ref = C_element
FEATURE [App::DocumentObjectGroupPython] N_element064  label="N_element : 036"  # scripted group (container) (typed FeaturePython)
  n = 5
  ref = N_element
FEATURE [App::DocumentObjectGroupPython] O_element126  label="O_element : 079"  # scripted group (container) (typed FeaturePython)
  n = 7
  ref = O_element
FEATURE [App::DocumentObjectGroupPython] P_element015  label="P_element : 004"  # scripted group (container) (typed FeaturePython)
  n = 1
  ref = P_element
FEATURE [App::DocumentObjectGroupPython] G4_DNA_A  # scripted group (container) (typed FeaturePython)
  Dunit = g/cm3
  Dvalue = 1
  Group = -> [H_element134,C_element144,N_element064,O_element126,P_element015]
  conduct = 2
  density = 1
  expand = 3
  formula = G4_DNA_A
  name = G4_DNA_A
  specific = 4
FEATURE [App::DocumentObjectGroupPython] H_element135  label="H_element : 082"  # scripted group (container) (typed FeaturePython)
  n = 10
  ref = H_element
FEATURE [App::DocumentObjectGroupPython] C_element145  label="C_element : 090"  # scripted group (container) (typed FeaturePython)
  n = 10
  ref = C_element
FEATURE [App::DocumentObjectGroupPython] N_element065  label="N_element : 037"  # scripted group (container) (typed FeaturePython)
  n = 5
  ref = N_element
FEATURE [App::DocumentObjectGroupPython] O_element127  label="O_element : 8"  # scripted group (container) (typed FeaturePython)
  n = 8
  ref = O_element
FEATURE [App::DocumentObjectGroupPython] P_element016  label="P_element : 005"  # scripted group (container) (typed FeaturePython)
  n = 1
  ref = P_element
FEATURE [App::DocumentObjectGroupPython] G4_DNA_G  # scripted group (container) (typed FeaturePython)
  Dunit = g/cm3
  Dvalue = 1
  Group = -> [H_element135,C_element145,N_element065,O_element127,P_element016]
  conduct = 2
  density = 1
  expand = 3
  formula = G4_DNA_G
  name = G4_DNA_G
  specific = 4
FEATURE [App::DocumentObjectGroupPython] H_element136  label="H_element : 083"  # scripted group (container) (typed FeaturePython)
  n = 10
  ref = H_element
FEATURE [App::DocumentObjectGroupPython] C_element146  label="C_element : 091"  # scripted group (container) (typed FeaturePython)
  n = 9
  ref = C_element
FEATURE [App::DocumentObjectGroupPython] N_element066  label="N_element : 038"  # scripted group (container) (typed FeaturePython)
  n = 3
  ref = N_element
FEATURE [App::DocumentObjectGroupPython] O_element128  label="O_element : 080"  # scripted group (container) (typed FeaturePython)
  n = 8
  ref = O_element
FEATURE [App::DocumentObjectGroupPython] P_element017  label="P_element : 006"  # scripted group (container) (typed FeaturePython)
  n = 1
  ref = P_element
FEATURE [App::DocumentObjectGroupPython] G4_DNA_C  # scripted group (container) (typed FeaturePython)
  Dunit = g/cm3
  Dvalue = 1
  Group = -> [H_element136,C_element146,N_element066,O_element128,P_element017]
  conduct = 2
  density = 1
  expand = 3
  formula = G4_DNA_C
  name = G4_DNA_C
  specific = 4
FEATURE [App::DocumentObjectGroupPython] H_element137  label="H_element : 084"  # scripted group (container) (typed FeaturePython)
  n = 9
  ref = H_element
FEATURE [App::DocumentObjectGroupPython] C_element147  label="C_element : 092"  # scripted group (container) (typed FeaturePython)
  n = 9
  ref = C_element
FEATURE [App::DocumentObjectGroupPython] N_element067  label="N_element : 039"  # scripted group (container) (typed FeaturePython)
  n = 2
  ref = N_element
FEATURE [App::DocumentObjectGroupPython] O_element129  label="O_element : 9"  # scripted group (container) (typed FeaturePython)
  n = 9
  ref = O_element
FEATURE [App::DocumentObjectGroupPython] P_element018  label="P_element : 007"  # scripted group (container) (typed FeaturePython)
  n = 1
  ref = P_element
FEATURE [App::DocumentObjectGroupPython] G4_DNA_U  # scripted group (container) (typed FeaturePython)
  Dunit = g/cm3
  Dvalue = 1
  Group = -> [H_element137,C_element147,N_element067,O_element129,P_element018]
  conduct = 2
  density = 1
  expand = 3
  formula = G4_DNA_U
  name = G4_DNA_U
  specific = 4
FEATURE [App::DocumentObjectGroupPython] H_element138  label="H_element : 085"  # scripted group (container) (typed FeaturePython)
  n = 11
  ref = H_element
FEATURE [App::DocumentObjectGroupPython] C_element148  label="C_element : 093"  # scripted group (container) (typed FeaturePython)
  n = 10
  ref = C_element
FEATURE [App::DocumentObjectGroupPython] N_element068  label="N_element : 040"  # scripted group (container) (typed FeaturePython)
  n = 2
  ref = N_element
FEATURE [App::DocumentObjectGroupPython] O_element130  label="O_element : 081"  # scripted group (container) (typed FeaturePython)
  n = 9
  ref = O_element
FEATURE [App::DocumentObjectGroupPython] P_element019  label="P_element : 008"  # scripted group (container) (typed FeaturePython)
  n = 1
  ref = P_element
FEATURE [App::DocumentObjectGroupPython] G4_DNA_MU  # scripted group (container) (typed FeaturePython)
  Dunit = g/cm3
  Dvalue = 1
  Group = -> [H_element138,C_element148,N_element068,O_element130,P_element019]
  conduct = 2
  density = 1
  expand = 3
  formula = G4_DNA_MU
  name = G4_DNA_MU
  specific = 4
FEATURE [App::DocumentObjectGroupPython] BioChemical  # scripted group (container) (typed FeaturePython)
  Group = -> [G4_CYTOSINE,G4_THYMINE,G4_URACIL,G4_DNA_ADENINE,G4_DNA_GUANINE,G4_DNA_CYTOSINE,G4_DNA_THYMINE,G4_DNA_URACIL,G4_DNA_ADENOSINE,G4_DNA_GUANOSINE,G4_DNA_CYTIDINE,G4_DNA_URIDINE,G4_DNA_METHYLURIDINE,G4_DNA_MONOPHOSPHATE,G4_DNA_A,G4_DNA_G,G4_DNA_C,G4_DNA_U,G4_DNA_MU]
FEATURE [App::DocumentObjectGroupPython] G4Materials  # scripted group (container) (typed FeaturePython)
  Group = -> [NIST,Element,HEP,Space,BioChemical]
  version = 1
FEATURE [App::DocumentObjectGroupPython] Geant4  # scripted group (container) (typed FeaturePython)
  Group = -> [G4Isotopes,G4Elements,G4Materials]
FEATURE [App::DocumentObjectGroupPython] Materials  # scripted group (container) (typed FeaturePython)
  Group = -> [Geant4]
FEATURE [Part::FeaturePython] GDMLBox_WorldBox  # WARN: FeaturePython — macro-defined, semantics opaque (R4)
  lunit = 2
  material = 7
  x = 400
  y = 400
  z = 400
FEATURE [Part::FeaturePython] GDMLBox_Box  # WARN: FeaturePython — macro-defined, semantics opaque (R4)
  lunit = 2
  material = 0
  x = 10
  y = 10
  z = 10
FEATURE [Part::FeaturePython] GDMLTube_Tube  # WARN: FeaturePython — macro-defined, semantics opaque (R4)
  aunit = 1
  deltaphi = 360
  lunit = 2
  material = 0
  rmax = 3
  rmin = 0
  startphi = 0
  z = 20
FEATURE [Part::Cut] Cut
  Base = -> GDMLBox_Box
  Placement = pos=(15,0,0) rot=(0,0,1;0rad)
  Tool = -> GDMLTube_Tube
  material = 5
FEATURE [Part::FeaturePython] Array  # Draft array (typed FeaturePython)
  Angle = 360
  ArrayType = 1
  Axis = (0,0,1)
  Base = -> Cut
  Center = (0,0,0)
  Count = 5
  Fuse = false
  IntervalAxis = (0,0,0)
  IntervalX = (50,0,0)
  IntervalY = (0,50,0)
  IntervalZ = (0,0,50)
  NumberCircles = 3
  NumberPolar = 5
  NumberX = 2
  NumberY = 2
  NumberZ = 1
  RadialDistance = 50
  Symmetry = 1
  TangentialDistance = 25
FEATURE [Part::FeaturePython] Array001  # Draft array (typed FeaturePython)
  Angle = 360
  ArrayType = 0
  Axis = (0,0,1)
  Base = -> Array
  Center = (0,0,0)
  Count = 4
  Fuse = false
  IntervalAxis = (0,0,0)
  IntervalX = (100,0,0)
  IntervalY = (0,100,0)
  IntervalZ = (0,0,100)
  NumberCircles = 3
  NumberPolar = 5
  NumberX = 2
  NumberY = 2
  NumberZ = 1
  RadialDistance = 50
  Symmetry = 1
  TangentialDistance = 25
  material = 193
FEATURE [App::Part] Bool_Cut  label="Arrays_of_solids"
  Group = -> [GDMLBox_Box,GDMLTube_Tube,Cut,Array,Array001]
  Origin = -> Origin003
FEATURE [App::Part] worldVOL
  Group = -> [GDMLBox_WorldBox,Bool_Cut]
  Origin = -> Origin
